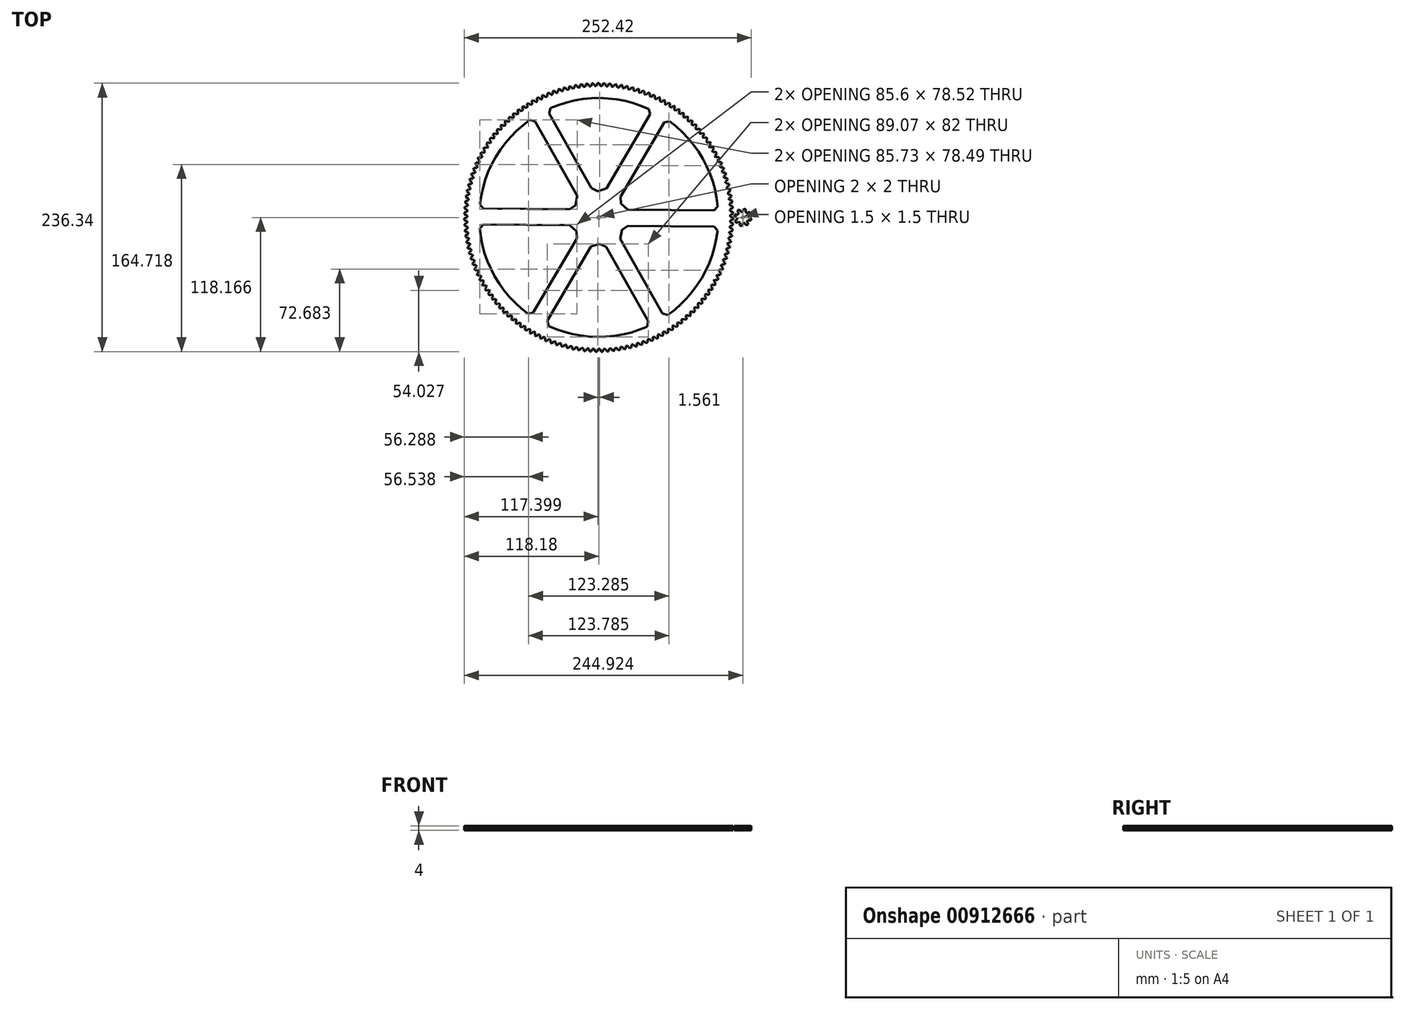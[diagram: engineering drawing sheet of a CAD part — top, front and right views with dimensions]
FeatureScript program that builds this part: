
annotation { "Feature Type Name" : "Feature", "Feature Type Description" : "" }
export const myFeature = defineFeature(function(context is Context, id is Id, definition is map)
    precondition{}
    {
        {
            var Q0;
            Q0=qCreatedBy(makeId("Top.planeOp"),FACE);
            var sketch = newSketch(context, id + "F0", { "sketchPlane" : qUnion([Q0])});
            skLineSegment(sketch, "E0", {"start": v(107.75, 0.66) * mm, "end": v(108.35, 0.46) * mm});
            skLineSegment(sketch, "E1", {"start": v(108.35, 0.46) * mm, "end": v(109.55, 0.02) * mm});
            skLineSegment(sketch, "E2", {"start": v(109.55, 0.02) * mm, "end": v(110.15, -0.2) * mm});
            skLineSegment(sketch, "E3", {"start": v(110.15, -0.2) * mm, "end": v(110.13, -1.82) * mm});
            skLineSegment(sketch, "E4", {"start": v(110.13, -1.82) * mm, "end": v(109.53, -2.04) * mm});
            skLineSegment(sketch, "E5", {"start": v(109.53, -2.04) * mm, "end": v(108.32, -2.46) * mm});
            skLineSegment(sketch, "E6", {"start": v(108.32, -2.46) * mm, "end": v(107.72, -2.65) * mm});
            skLineSegment(sketch, "E7", {"start": v(107.72, -2.65) * mm, "end": v(107.67, -4.29) * mm});
            skLineSegment(sketch, "E8", {"start": v(107.67, -4.29) * mm, "end": v(108.26, -4.52) * mm});
            skLineSegment(sketch, "E9", {"start": v(108.26, -4.52) * mm, "end": v(109.44, -5) * mm});
            skLineSegment(sketch, "E10", {"start": v(109.44, -5) * mm, "end": v(110.03, -5.26) * mm});
            skLineSegment(sketch, "E11", {"start": v(110.03, -5.26) * mm, "end": v(109.95, -6.87) * mm});
            skLineSegment(sketch, "E12", {"start": v(109.95, -6.87) * mm, "end": v(109.34, -7.06) * mm});
            skLineSegment(sketch, "E13", {"start": v(109.34, -7.06) * mm, "end": v(108.11, -7.42) * mm});
            skLineSegment(sketch, "E14", {"start": v(108.11, -7.42) * mm, "end": v(107.5, -7.59) * mm});
            skLineSegment(sketch, "E15", {"start": v(107.5, -7.59) * mm, "end": v(107.38, -9.23) * mm});
            skLineSegment(sketch, "E16", {"start": v(107.38, -9.23) * mm, "end": v(107.96, -9.48) * mm});
            skLineSegment(sketch, "E17", {"start": v(107.96, -9.48) * mm, "end": v(109.12, -10.02) * mm});
            skLineSegment(sketch, "E18", {"start": v(109.12, -10.02) * mm, "end": v(109.7, -10.3) * mm});
            skLineSegment(sketch, "E19", {"start": v(109.7, -10.3) * mm, "end": v(109.55, -11.9) * mm});
            skLineSegment(sketch, "E20", {"start": v(109.55, -11.9) * mm, "end": v(108.93, -12.07) * mm});
            skLineSegment(sketch, "E21", {"start": v(108.93, -12.07) * mm, "end": v(107.69, -12.38) * mm});
            skLineSegment(sketch, "E22", {"start": v(107.69, -12.38) * mm, "end": v(107.07, -12.52) * mm});
            skLineSegment(sketch, "E23", {"start": v(107.07, -12.52) * mm, "end": v(106.88, -14.15) * mm});
            skLineSegment(sketch, "E24", {"start": v(106.88, -14.15) * mm, "end": v(107.45, -14.43) * mm});
            skLineSegment(sketch, "E25", {"start": v(107.45, -14.43) * mm, "end": v(108.59, -15.01) * mm});
            skLineSegment(sketch, "E26", {"start": v(108.59, -15.01) * mm, "end": v(109.15, -15.32) * mm});
            skLineSegment(sketch, "E27", {"start": v(109.15, -15.32) * mm, "end": v(108.93, -16.91) * mm});
            skLineSegment(sketch, "E28", {"start": v(108.93, -16.91) * mm, "end": v(108.3, -17.06) * mm});
            skLineSegment(sketch, "E29", {"start": v(108.3, -17.06) * mm, "end": v(107.05, -17.31) * mm});
            skLineSegment(sketch, "E30", {"start": v(107.05, -17.31) * mm, "end": v(106.43, -17.43) * mm});
            skLineSegment(sketch, "E31", {"start": v(106.43, -17.43) * mm, "end": v(106.17, -19.05) * mm});
            skLineSegment(sketch, "E32", {"start": v(106.17, -19.05) * mm, "end": v(106.73, -19.35) * mm});
            skLineSegment(sketch, "E33", {"start": v(106.73, -19.35) * mm, "end": v(107.84, -19.98) * mm});
            skLineSegment(sketch, "E34", {"start": v(107.84, -19.98) * mm, "end": v(108.4, -20.31) * mm});
            skLineSegment(sketch, "E35", {"start": v(108.4, -20.31) * mm, "end": v(108.1, -21.9) * mm});
            skLineSegment(sketch, "E36", {"start": v(108.1, -21.9) * mm, "end": v(107.47, -22.01) * mm});
            skLineSegment(sketch, "E37", {"start": v(107.47, -22.01) * mm, "end": v(106.2, -22.22) * mm});
            skLineSegment(sketch, "E38", {"start": v(106.2, -22.22) * mm, "end": v(105.58, -22.3) * mm});
            skLineSegment(sketch, "E39", {"start": v(105.58, -22.3) * mm, "end": v(105.25, -23.91) * mm});
            skLineSegment(sketch, "E40", {"start": v(105.25, -23.91) * mm, "end": v(105.8, -24.24) * mm});
            skLineSegment(sketch, "E41", {"start": v(105.8, -24.24) * mm, "end": v(106.88, -24.91) * mm});
            skLineSegment(sketch, "E42", {"start": v(106.88, -24.91) * mm, "end": v(107.42, -25.27) * mm});
            skLineSegment(sketch, "E43", {"start": v(107.42, -25.27) * mm, "end": v(107.06, -26.84) * mm});
            skLineSegment(sketch, "E44", {"start": v(107.06, -26.84) * mm, "end": v(106.42, -26.93) * mm});
            skLineSegment(sketch, "E45", {"start": v(106.42, -26.93) * mm, "end": v(105.16, -27.08) * mm});
            skLineSegment(sketch, "E46", {"start": v(105.16, -27.08) * mm, "end": v(104.53, -27.13) * mm});
            skLineSegment(sketch, "E47", {"start": v(104.53, -27.13) * mm, "end": v(104.13, -28.73) * mm});
            skLineSegment(sketch, "E48", {"start": v(104.13, -28.73) * mm, "end": v(104.66, -29.08) * mm});
            skLineSegment(sketch, "E49", {"start": v(104.66, -29.08) * mm, "end": v(105.71, -29.8) * mm});
            skLineSegment(sketch, "E50", {"start": v(105.71, -29.8) * mm, "end": v(106.23, -30.18) * mm});
            skLineSegment(sketch, "E51", {"start": v(106.23, -30.18) * mm, "end": v(105.8, -31.73) * mm});
            skLineSegment(sketch, "E52", {"start": v(105.8, -31.73) * mm, "end": v(105.17, -31.8) * mm});
            skLineSegment(sketch, "E53", {"start": v(105.17, -31.8) * mm, "end": v(103.9, -31.89) * mm});
            skLineSegment(sketch, "E54", {"start": v(103.9, -31.89) * mm, "end": v(103.26, -31.92) * mm});
            skLineSegment(sketch, "E55", {"start": v(103.26, -31.92) * mm, "end": v(102.8, -33.5) * mm});
            skLineSegment(sketch, "E56", {"start": v(102.8, -33.5) * mm, "end": v(103.31, -33.87) * mm});
            skLineSegment(sketch, "E57", {"start": v(103.31, -33.87) * mm, "end": v(104.33, -34.63) * mm});
            skLineSegment(sketch, "E58", {"start": v(104.33, -34.63) * mm, "end": v(104.84, -35.03) * mm});
            skLineSegment(sketch, "E59", {"start": v(104.84, -35.03) * mm, "end": v(104.35, -36.57) * mm});
            skLineSegment(sketch, "E60", {"start": v(104.35, -36.57) * mm, "end": v(103.7, -36.6) * mm});
            skLineSegment(sketch, "E61", {"start": v(103.7, -36.6) * mm, "end": v(102.43, -36.64) * mm});
            skLineSegment(sketch, "E62", {"start": v(102.43, -36.64) * mm, "end": v(101.8, -36.65) * mm});
            skLineSegment(sketch, "E63", {"start": v(101.8, -36.65) * mm, "end": v(101.27, -38.2) * mm});
            skLineSegment(sketch, "E64", {"start": v(101.27, -38.2) * mm, "end": v(101.77, -38.6) * mm});
            skLineSegment(sketch, "E65", {"start": v(101.77, -38.6) * mm, "end": v(102.75, -39.4) * mm});
            skLineSegment(sketch, "E66", {"start": v(102.75, -39.4) * mm, "end": v(103.24, -39.82) * mm});
            skLineSegment(sketch, "E67", {"start": v(103.24, -39.82) * mm, "end": v(102.68, -41.34) * mm});
            skLineSegment(sketch, "E68", {"start": v(102.68, -41.34) * mm, "end": v(102.04, -41.34) * mm});
            skLineSegment(sketch, "E69", {"start": v(102.04, -41.34) * mm, "end": v(100.77, -41.33) * mm});
            skLineSegment(sketch, "E70", {"start": v(100.77, -41.33) * mm, "end": v(100.13, -41.3) * mm});
            skLineSegment(sketch, "E71", {"start": v(100.13, -41.3) * mm, "end": v(99.53, -42.84) * mm});
            skLineSegment(sketch, "E72", {"start": v(99.53, -42.84) * mm, "end": v(100.02, -43.25) * mm});
            skLineSegment(sketch, "E73", {"start": v(100.02, -43.25) * mm, "end": v(100.97, -44.1) * mm});
            skLineSegment(sketch, "E74", {"start": v(100.97, -44.1) * mm, "end": v(101.43, -44.54) * mm});
            skLineSegment(sketch, "E75", {"start": v(101.43, -44.54) * mm, "end": v(100.82, -46.03) * mm});
            skLineSegment(sketch, "E76", {"start": v(100.82, -46.03) * mm, "end": v(100.17, -46) * mm});
            skLineSegment(sketch, "E77", {"start": v(100.17, -46) * mm, "end": v(98.9, -45.94) * mm});
            skLineSegment(sketch, "E78", {"start": v(98.9, -45.94) * mm, "end": v(98.27, -45.89) * mm});
            skLineSegment(sketch, "E79", {"start": v(98.27, -45.89) * mm, "end": v(97.6, -47.4) * mm});
            skLineSegment(sketch, "E80", {"start": v(97.6, -47.4) * mm, "end": v(98.07, -47.83) * mm});
            skLineSegment(sketch, "E81", {"start": v(98.07, -47.83) * mm, "end": v(98.98, -48.72) * mm});
            skLineSegment(sketch, "E82", {"start": v(98.98, -48.72) * mm, "end": v(99.43, -49.18) * mm});
            skLineSegment(sketch, "E83", {"start": v(99.43, -49.18) * mm, "end": v(98.75, -50.64) * mm});
            skLineSegment(sketch, "E84", {"start": v(98.75, -50.64) * mm, "end": v(98.1, -50.6) * mm});
            skLineSegment(sketch, "E85", {"start": v(98.1, -50.6) * mm, "end": v(96.84, -50.47) * mm});
            skLineSegment(sketch, "E86", {"start": v(96.84, -50.47) * mm, "end": v(96.21, -50.39) * mm});
            skLineSegment(sketch, "E87", {"start": v(96.21, -50.39) * mm, "end": v(95.48, -51.87) * mm});
            skLineSegment(sketch, "E88", {"start": v(95.48, -51.87) * mm, "end": v(95.93, -52.32) * mm});
            skLineSegment(sketch, "E89", {"start": v(95.93, -52.32) * mm, "end": v(96.8, -53.25) * mm});
            skLineSegment(sketch, "E90", {"start": v(96.8, -53.25) * mm, "end": v(97.23, -53.73) * mm});
            skLineSegment(sketch, "E91", {"start": v(97.23, -53.73) * mm, "end": v(96.5, -55.16) * mm});
            skLineSegment(sketch, "E92", {"start": v(96.5, -55.16) * mm, "end": v(95.85, -55.08) * mm});
            skLineSegment(sketch, "E93", {"start": v(95.85, -55.08) * mm, "end": v(94.59, -54.9) * mm});
            skLineSegment(sketch, "E94", {"start": v(94.59, -54.9) * mm, "end": v(93.96, -54.8) * mm});
            skLineSegment(sketch, "E95", {"start": v(93.96, -54.8) * mm, "end": v(93.17, -56.24) * mm});
            skLineSegment(sketch, "E96", {"start": v(93.17, -56.24) * mm, "end": v(93.6, -56.71) * mm});
            skLineSegment(sketch, "E97", {"start": v(93.6, -56.71) * mm, "end": v(94.43, -57.68) * mm});
            skLineSegment(sketch, "E98", {"start": v(94.43, -57.68) * mm, "end": v(94.84, -58.17) * mm});
            skLineSegment(sketch, "E99", {"start": v(94.84, -58.17) * mm, "end": v(94.04, -59.57) * mm});
            skLineSegment(sketch, "E100", {"start": v(94.04, -59.57) * mm, "end": v(93.4, -59.47) * mm});
            skLineSegment(sketch, "E101", {"start": v(93.4, -59.47) * mm, "end": v(92.15, -59.24) * mm});
            skLineSegment(sketch, "E102", {"start": v(92.15, -59.24) * mm, "end": v(91.53, -59.1) * mm});
            skLineSegment(sketch, "E103", {"start": v(91.53, -59.1) * mm, "end": v(90.68, -60.51) * mm});
            skLineSegment(sketch, "E104", {"start": v(90.68, -60.51) * mm, "end": v(91.08, -61) * mm});
            skLineSegment(sketch, "E105", {"start": v(91.08, -61) * mm, "end": v(91.87, -62) * mm});
            skLineSegment(sketch, "E106", {"start": v(91.87, -62) * mm, "end": v(92.26, -62.52) * mm});
            skLineSegment(sketch, "E107", {"start": v(92.26, -62.52) * mm, "end": v(91.4, -63.88) * mm});
            skLineSegment(sketch, "E108", {"start": v(91.4, -63.88) * mm, "end": v(90.77, -63.75) * mm});
            skLineSegment(sketch, "E109", {"start": v(90.77, -63.75) * mm, "end": v(89.53, -63.46) * mm});
            skLineSegment(sketch, "E110", {"start": v(89.53, -63.46) * mm, "end": v(88.91, -63.3) * mm});
            skLineSegment(sketch, "E111", {"start": v(88.91, -63.3) * mm, "end": v(88, -64.68) * mm});
            skLineSegment(sketch, "E112", {"start": v(88, -64.68) * mm, "end": v(88.39, -65.18) * mm});
            skLineSegment(sketch, "E113", {"start": v(88.39, -65.18) * mm, "end": v(89.13, -66.22) * mm});
            skLineSegment(sketch, "E114", {"start": v(89.13, -66.22) * mm, "end": v(89.5, -66.75) * mm});
            skLineSegment(sketch, "E115", {"start": v(89.5, -66.75) * mm, "end": v(88.58, -68.07) * mm});
            skLineSegment(sketch, "E116", {"start": v(88.58, -68.07) * mm, "end": v(87.96, -67.91) * mm});
            skLineSegment(sketch, "E117", {"start": v(87.96, -67.91) * mm, "end": v(86.72, -67.57) * mm});
            skLineSegment(sketch, "E118", {"start": v(86.72, -67.57) * mm, "end": v(86.12, -67.4) * mm});
            skLineSegment(sketch, "E119", {"start": v(86.12, -67.4) * mm, "end": v(85.15, -68.72) * mm});
            skLineSegment(sketch, "E120", {"start": v(85.15, -68.72) * mm, "end": v(85.51, -69.24) * mm});
            skLineSegment(sketch, "E121", {"start": v(85.51, -69.24) * mm, "end": v(86.22, -70.3) * mm});
            skLineSegment(sketch, "E122", {"start": v(86.22, -70.3) * mm, "end": v(86.56, -70.85) * mm});
            skLineSegment(sketch, "E123", {"start": v(86.56, -70.85) * mm, "end": v(85.58, -72.13) * mm});
            skLineSegment(sketch, "E124", {"start": v(85.58, -72.13) * mm, "end": v(84.97, -71.95) * mm});
            skLineSegment(sketch, "E125", {"start": v(84.97, -71.95) * mm, "end": v(83.75, -71.56) * mm});
            skLineSegment(sketch, "E126", {"start": v(83.75, -71.56) * mm, "end": v(83.15, -71.35) * mm});
            skLineSegment(sketch, "E127", {"start": v(83.15, -71.35) * mm, "end": v(82.13, -72.64) * mm});
            skLineSegment(sketch, "E128", {"start": v(82.13, -72.64) * mm, "end": v(82.47, -73.17) * mm});
            skLineSegment(sketch, "E129", {"start": v(82.47, -73.17) * mm, "end": v(83.13, -74.27) * mm});
            skLineSegment(sketch, "E130", {"start": v(83.13, -74.27) * mm, "end": v(83.44, -74.83) * mm});
            skLineSegment(sketch, "E131", {"start": v(83.44, -74.83) * mm, "end": v(82.42, -76.07) * mm});
            skLineSegment(sketch, "E132", {"start": v(82.42, -76.07) * mm, "end": v(81.8, -75.86) * mm});
            skLineSegment(sketch, "E133", {"start": v(81.8, -75.86) * mm, "end": v(80.6, -75.42) * mm});
            skLineSegment(sketch, "E134", {"start": v(80.6, -75.42) * mm, "end": v(80.02, -75.18) * mm});
            skLineSegment(sketch, "E135", {"start": v(80.02, -75.18) * mm, "end": v(78.94, -76.43) * mm});
            skLineSegment(sketch, "E136", {"start": v(78.94, -76.43) * mm, "end": v(79.26, -76.98) * mm});
            skLineSegment(sketch, "E137", {"start": v(79.26, -76.98) * mm, "end": v(79.87, -78.1) * mm});
            skLineSegment(sketch, "E138", {"start": v(79.87, -78.1) * mm, "end": v(80.16, -78.67) * mm});
            skLineSegment(sketch, "E139", {"start": v(80.16, -78.67) * mm, "end": v(79.08, -79.86) * mm});
            skLineSegment(sketch, "E140", {"start": v(79.08, -79.86) * mm, "end": v(78.48, -79.63) * mm});
            skLineSegment(sketch, "E141", {"start": v(78.48, -79.63) * mm, "end": v(77.3, -79.14) * mm});
            skLineSegment(sketch, "E142", {"start": v(77.3, -79.14) * mm, "end": v(76.73, -78.88) * mm});
            skLineSegment(sketch, "E143", {"start": v(76.73, -78.88) * mm, "end": v(75.6, -80.07) * mm});
            skLineSegment(sketch, "E144", {"start": v(75.6, -80.07) * mm, "end": v(75.9, -80.63) * mm});
            skLineSegment(sketch, "E145", {"start": v(75.9, -80.63) * mm, "end": v(76.45, -81.78) * mm});
            skLineSegment(sketch, "E146", {"start": v(76.45, -81.78) * mm, "end": v(76.72, -82.37) * mm});
            skLineSegment(sketch, "E147", {"start": v(76.72, -82.37) * mm, "end": v(75.6, -83.51) * mm});
            skLineSegment(sketch, "E148", {"start": v(75.6, -83.51) * mm, "end": v(75, -83.25) * mm});
            skLineSegment(sketch, "E149", {"start": v(75, -83.25) * mm, "end": v(73.85, -82.7) * mm});
            skLineSegment(sketch, "E150", {"start": v(73.85, -82.7) * mm, "end": v(73.28, -82.43) * mm});
            skLineSegment(sketch, "E151", {"start": v(73.28, -82.43) * mm, "end": v(72.1, -83.57) * mm});
            skLineSegment(sketch, "E152", {"start": v(72.1, -83.57) * mm, "end": v(72.37, -84.15) * mm});
            skLineSegment(sketch, "E153", {"start": v(72.37, -84.15) * mm, "end": v(72.88, -85.32) * mm});
            skLineSegment(sketch, "E154", {"start": v(72.88, -85.32) * mm, "end": v(73.12, -85.91) * mm});
            skLineSegment(sketch, "E155", {"start": v(73.12, -85.91) * mm, "end": v(71.95, -87) * mm});
            skLineSegment(sketch, "E156", {"start": v(71.95, -87) * mm, "end": v(71.37, -86.72) * mm});
            skLineSegment(sketch, "E157", {"start": v(71.37, -86.72) * mm, "end": v(70.24, -86.13) * mm});
            skLineSegment(sketch, "E158", {"start": v(70.24, -86.13) * mm, "end": v(69.68, -85.83) * mm});
            skLineSegment(sketch, "E159", {"start": v(69.68, -85.83) * mm, "end": v(68.46, -86.92) * mm});
            skLineSegment(sketch, "E160", {"start": v(68.46, -86.92) * mm, "end": v(68.7, -87.5) * mm});
            skLineSegment(sketch, "E161", {"start": v(68.7, -87.5) * mm, "end": v(69.16, -88.7) * mm});
            skLineSegment(sketch, "E162", {"start": v(69.16, -88.7) * mm, "end": v(69.38, -89.3) * mm});
            skLineSegment(sketch, "E163", {"start": v(69.38, -89.3) * mm, "end": v(68.16, -90.35) * mm});
            skLineSegment(sketch, "E164", {"start": v(68.16, -90.35) * mm, "end": v(67.6, -90.04) * mm});
            skLineSegment(sketch, "E165", {"start": v(67.6, -90.04) * mm, "end": v(66.49, -89.4) * mm});
            skLineSegment(sketch, "E166", {"start": v(66.49, -89.4) * mm, "end": v(65.95, -89.07) * mm});
            skLineSegment(sketch, "E167", {"start": v(65.95, -89.07) * mm, "end": v(64.67, -90.1) * mm});
            skLineSegment(sketch, "E168", {"start": v(64.67, -90.1) * mm, "end": v(64.9, -90.7) * mm});
            skLineSegment(sketch, "E169", {"start": v(64.9, -90.7) * mm, "end": v(65.3, -91.91) * mm});
            skLineSegment(sketch, "E170", {"start": v(65.3, -91.91) * mm, "end": v(65.5, -92.53) * mm});
            skLineSegment(sketch, "E171", {"start": v(65.5, -92.53) * mm, "end": v(64.23, -93.52) * mm});
            skLineSegment(sketch, "E172", {"start": v(64.23, -93.52) * mm, "end": v(63.67, -93.19) * mm});
            skLineSegment(sketch, "E173", {"start": v(63.67, -93.19) * mm, "end": v(62.6, -92.5) * mm});
            skLineSegment(sketch, "E174", {"start": v(62.6, -92.5) * mm, "end": v(62.07, -92.15) * mm});
            skLineSegment(sketch, "E175", {"start": v(62.07, -92.15) * mm, "end": v(60.76, -93.13) * mm});
            skLineSegment(sketch, "E176", {"start": v(60.76, -93.13) * mm, "end": v(60.95, -93.74) * mm});
            skLineSegment(sketch, "E177", {"start": v(60.95, -93.74) * mm, "end": v(61.3, -94.96) * mm});
            skLineSegment(sketch, "E178", {"start": v(61.3, -94.96) * mm, "end": v(61.47, -95.58) * mm});
            skLineSegment(sketch, "E179", {"start": v(61.47, -95.58) * mm, "end": v(60.16, -96.52) * mm});
            skLineSegment(sketch, "E180", {"start": v(60.16, -96.52) * mm, "end": v(59.63, -96.17) * mm});
            skLineSegment(sketch, "E181", {"start": v(59.63, -96.17) * mm, "end": v(58.58, -95.43) * mm});
            skLineSegment(sketch, "E182", {"start": v(58.58, -95.43) * mm, "end": v(58.07, -95.06) * mm});
            skLineSegment(sketch, "E183", {"start": v(58.07, -95.06) * mm, "end": v(56.72, -95.99) * mm});
            skLineSegment(sketch, "E184", {"start": v(56.72, -95.99) * mm, "end": v(56.88, -96.6) * mm});
            skLineSegment(sketch, "E185", {"start": v(56.88, -96.6) * mm, "end": v(57.19, -97.84) * mm});
            skLineSegment(sketch, "E186", {"start": v(57.19, -97.84) * mm, "end": v(57.32, -98.47) * mm});
            skLineSegment(sketch, "E187", {"start": v(57.32, -98.47) * mm, "end": v(55.98, -99.35) * mm});
            skLineSegment(sketch, "E188", {"start": v(55.98, -99.35) * mm, "end": v(55.46, -98.97) * mm});
            skLineSegment(sketch, "E189", {"start": v(55.46, -98.97) * mm, "end": v(54.44, -98.2) * mm});
            skLineSegment(sketch, "E190", {"start": v(54.44, -98.2) * mm, "end": v(53.95, -97.8) * mm});
            skLineSegment(sketch, "E191", {"start": v(53.95, -97.8) * mm, "end": v(52.55, -98.67) * mm});
            skLineSegment(sketch, "E192", {"start": v(52.55, -98.67) * mm, "end": v(52.7, -99.28) * mm});
            skLineSegment(sketch, "E193", {"start": v(52.7, -99.28) * mm, "end": v(52.95, -100.54) * mm});
            skLineSegment(sketch, "E194", {"start": v(52.95, -100.54) * mm, "end": v(53.06, -101.17) * mm});
            skLineSegment(sketch, "E195", {"start": v(53.06, -101.17) * mm, "end": v(51.67, -102) * mm});
            skLineSegment(sketch, "E196", {"start": v(51.67, -102) * mm, "end": v(51.17, -101.6) * mm});
            skLineSegment(sketch, "E197", {"start": v(51.17, -101.6) * mm, "end": v(50.2, -100.77) * mm});
            skLineSegment(sketch, "E198", {"start": v(50.2, -100.77) * mm, "end": v(49.71, -100.36) * mm});
            skLineSegment(sketch, "E199", {"start": v(49.71, -100.36) * mm, "end": v(48.28, -101.17) * mm});
            skLineSegment(sketch, "E200", {"start": v(48.28, -101.17) * mm, "end": v(48.4, -101.79) * mm});
            skLineSegment(sketch, "E201", {"start": v(48.4, -101.79) * mm, "end": v(48.6, -103.05) * mm});
            skLineSegment(sketch, "E202", {"start": v(48.6, -103.05) * mm, "end": v(48.68, -103.69) * mm});
            skLineSegment(sketch, "E203", {"start": v(48.68, -103.69) * mm, "end": v(47.26, -104.45) * mm});
            skLineSegment(sketch, "E204", {"start": v(47.26, -104.45) * mm, "end": v(46.78, -104.03) * mm});
            skLineSegment(sketch, "E205", {"start": v(46.78, -104.03) * mm, "end": v(45.83, -103.17) * mm});
            skLineSegment(sketch, "E206", {"start": v(45.83, -103.17) * mm, "end": v(45.37, -102.73) * mm});
            skLineSegment(sketch, "E207", {"start": v(45.37, -102.73) * mm, "end": v(43.9, -103.48) * mm});
            skLineSegment(sketch, "E208", {"start": v(43.9, -103.48) * mm, "end": v(44, -104.1) * mm});
            skLineSegment(sketch, "E209", {"start": v(44, -104.1) * mm, "end": v(44.14, -105.38) * mm});
            skLineSegment(sketch, "E210", {"start": v(44.14, -105.38) * mm, "end": v(44.2, -106.02) * mm});
            skLineSegment(sketch, "E211", {"start": v(44.2, -106.02) * mm, "end": v(42.75, -106.72) * mm});
            skLineSegment(sketch, "E212", {"start": v(42.75, -106.72) * mm, "end": v(42.28, -106.28) * mm});
            skLineSegment(sketch, "E213", {"start": v(42.28, -106.28) * mm, "end": v(41.37, -105.38) * mm});
            skLineSegment(sketch, "E214", {"start": v(41.37, -105.38) * mm, "end": v(40.94, -104.92) * mm});
            skLineSegment(sketch, "E215", {"start": v(40.94, -104.92) * mm, "end": v(39.44, -105.6) * mm});
            skLineSegment(sketch, "E216", {"start": v(39.44, -105.6) * mm, "end": v(39.5, -106.23) * mm});
            skLineSegment(sketch, "E217", {"start": v(39.5, -106.23) * mm, "end": v(39.59, -107.5) * mm});
            skLineSegment(sketch, "E218", {"start": v(39.59, -107.5) * mm, "end": v(39.62, -108.15) * mm});
            skLineSegment(sketch, "E219", {"start": v(39.62, -108.15) * mm, "end": v(38.14, -108.79) * mm});
            skLineSegment(sketch, "E220", {"start": v(38.14, -108.79) * mm, "end": v(37.7, -108.33) * mm});
            skLineSegment(sketch, "E221", {"start": v(37.7, -108.33) * mm, "end": v(36.83, -107.4) * mm});
            skLineSegment(sketch, "E222", {"start": v(36.83, -107.4) * mm, "end": v(36.4, -106.92) * mm});
            skLineSegment(sketch, "E223", {"start": v(36.4, -106.92) * mm, "end": v(34.88, -107.54) * mm});
            skLineSegment(sketch, "E224", {"start": v(34.88, -107.54) * mm, "end": v(34.92, -108.17) * mm});
            skLineSegment(sketch, "E225", {"start": v(34.92, -108.17) * mm, "end": v(34.95, -109.44) * mm});
            skLineSegment(sketch, "E226", {"start": v(34.95, -109.44) * mm, "end": v(34.95, -110.09) * mm});
            skLineSegment(sketch, "E227", {"start": v(34.95, -110.09) * mm, "end": v(33.45, -110.66) * mm});
            skLineSegment(sketch, "E228", {"start": v(33.45, -110.66) * mm, "end": v(33.02, -110.18) * mm});
            skLineSegment(sketch, "E229", {"start": v(33.02, -110.18) * mm, "end": v(32.2, -109.2) * mm});
            skLineSegment(sketch, "E230", {"start": v(32.2, -109.2) * mm, "end": v(31.8, -108.72) * mm});
            skLineSegment(sketch, "E231", {"start": v(31.8, -108.72) * mm, "end": v(30.25, -109.27) * mm});
            skLineSegment(sketch, "E232", {"start": v(30.25, -109.27) * mm, "end": v(30.26, -109.9) * mm});
            skLineSegment(sketch, "E233", {"start": v(30.26, -109.9) * mm, "end": v(30.24, -111.18) * mm});
            skLineSegment(sketch, "E234", {"start": v(30.24, -111.18) * mm, "end": v(30.21, -111.82) * mm});
            skLineSegment(sketch, "E235", {"start": v(30.21, -111.82) * mm, "end": v(28.68, -112.33) * mm});
            skLineSegment(sketch, "E236", {"start": v(28.68, -112.33) * mm, "end": v(28.28, -111.84) * mm});
            skLineSegment(sketch, "E237", {"start": v(28.28, -111.84) * mm, "end": v(27.5, -110.83) * mm});
            skLineSegment(sketch, "E238", {"start": v(27.5, -110.83) * mm, "end": v(27.12, -110.32) * mm});
            skLineSegment(sketch, "E239", {"start": v(27.12, -110.32) * mm, "end": v(25.55, -110.8) * mm});
            skLineSegment(sketch, "E240", {"start": v(25.55, -110.8) * mm, "end": v(25.53, -111.44) * mm});
            skLineSegment(sketch, "E241", {"start": v(25.53, -111.44) * mm, "end": v(25.45, -112.71) * mm});
            skLineSegment(sketch, "E242", {"start": v(25.45, -112.71) * mm, "end": v(25.4, -113.36) * mm});
            skLineSegment(sketch, "E243", {"start": v(25.4, -113.36) * mm, "end": v(23.85, -113.8) * mm});
            skLineSegment(sketch, "E244", {"start": v(23.85, -113.8) * mm, "end": v(23.47, -113.29) * mm});
            skLineSegment(sketch, "E245", {"start": v(23.47, -113.29) * mm, "end": v(22.73, -112.25) * mm});
            skLineSegment(sketch, "E246", {"start": v(22.73, -112.25) * mm, "end": v(22.37, -111.72) * mm});
            skLineSegment(sketch, "E247", {"start": v(22.37, -111.72) * mm, "end": v(20.78, -112.14) * mm});
            skLineSegment(sketch, "E248", {"start": v(20.78, -112.14) * mm, "end": v(20.73, -112.77) * mm});
            skLineSegment(sketch, "E249", {"start": v(20.73, -112.77) * mm, "end": v(20.6, -114.04) * mm});
            skLineSegment(sketch, "E250", {"start": v(20.6, -114.04) * mm, "end": v(20.52, -114.68) * mm});
            skLineSegment(sketch, "E251", {"start": v(20.52, -114.68) * mm, "end": v(18.96, -115.06) * mm});
            skLineSegment(sketch, "E252", {"start": v(18.96, -115.06) * mm, "end": v(18.6, -114.53) * mm});
            skLineSegment(sketch, "E253", {"start": v(18.6, -114.53) * mm, "end": v(17.9, -113.46) * mm});
            skLineSegment(sketch, "E254", {"start": v(17.9, -113.46) * mm, "end": v(17.57, -112.92) * mm});
            skLineSegment(sketch, "E255", {"start": v(17.57, -112.92) * mm, "end": v(15.96, -113.27) * mm});
            skLineSegment(sketch, "E256", {"start": v(15.96, -113.27) * mm, "end": v(15.89, -113.9) * mm});
            skLineSegment(sketch, "E257", {"start": v(15.89, -113.9) * mm, "end": v(15.7, -115.16) * mm});
            skLineSegment(sketch, "E258", {"start": v(15.7, -115.16) * mm, "end": v(15.6, -115.8) * mm});
            skLineSegment(sketch, "E259", {"start": v(15.6, -115.8) * mm, "end": v(14.02, -116.1) * mm});
            skLineSegment(sketch, "E260", {"start": v(14.02, -116.1) * mm, "end": v(13.68, -115.56) * mm});
            skLineSegment(sketch, "E261", {"start": v(13.68, -115.56) * mm, "end": v(13.03, -114.46) * mm});
            skLineSegment(sketch, "E262", {"start": v(13.03, -114.46) * mm, "end": v(12.72, -113.9) * mm});
            skLineSegment(sketch, "E263", {"start": v(12.72, -113.9) * mm, "end": v(11.1, -114.2) * mm});
            skLineSegment(sketch, "E264", {"start": v(11.1, -114.2) * mm, "end": v(11, -114.82) * mm});
            skLineSegment(sketch, "E265", {"start": v(11, -114.82) * mm, "end": v(10.76, -116.07) * mm});
            skLineSegment(sketch, "E266", {"start": v(10.76, -116.07) * mm, "end": v(10.63, -116.7) * mm});
            skLineSegment(sketch, "E267", {"start": v(10.63, -116.7) * mm, "end": v(9.04, -116.94) * mm});
            skLineSegment(sketch, "E268", {"start": v(9.04, -116.94) * mm, "end": v(8.72, -116.38) * mm});
            skLineSegment(sketch, "E269", {"start": v(8.72, -116.38) * mm, "end": v(8.12, -115.26) * mm});
            skLineSegment(sketch, "E270", {"start": v(8.12, -115.26) * mm, "end": v(7.84, -114.7) * mm});
            skLineSegment(sketch, "E271", {"start": v(7.84, -114.7) * mm, "end": v(6.2, -114.9) * mm});
            skLineSegment(sketch, "E272", {"start": v(6.2, -114.9) * mm, "end": v(6.08, -115.52) * mm});
            skLineSegment(sketch, "E273", {"start": v(6.08, -115.52) * mm, "end": v(5.79, -116.77) * mm});
            skLineSegment(sketch, "E274", {"start": v(5.79, -116.77) * mm, "end": v(5.63, -117.4) * mm});
            skLineSegment(sketch, "E275", {"start": v(5.63, -117.4) * mm, "end": v(4.02, -117.57) * mm});
            skLineSegment(sketch, "E276", {"start": v(4.02, -117.57) * mm, "end": v(3.73, -117) * mm});
            skLineSegment(sketch, "E277", {"start": v(3.73, -117) * mm, "end": v(3.18, -115.84) * mm});
            skLineSegment(sketch, "E278", {"start": v(3.18, -115.84) * mm, "end": v(2.92, -115.26) * mm});
            skLineSegment(sketch, "E279", {"start": v(2.92, -115.26) * mm, "end": v(1.28, -115.4) * mm});
            skLineSegment(sketch, "E280", {"start": v(1.28, -115.4) * mm, "end": v(1.13, -116.02) * mm});
            skLineSegment(sketch, "E281", {"start": v(1.13, -116.02) * mm, "end": v(0.78, -117.25) * mm});
            skLineSegment(sketch, "E282", {"start": v(0.78, -117.25) * mm, "end": v(0.6, -117.87) * mm});
            skLineSegment(sketch, "E283", {"start": v(0.6, -117.87) * mm, "end": v(-1, -117.97) * mm});
            skLineSegment(sketch, "E284", {"start": v(-1, -117.97) * mm, "end": v(-1.28, -117.39) * mm});
            skLineSegment(sketch, "E285", {"start": v(-1.28, -117.39) * mm, "end": v(-1.78, -116.22) * mm});
            skLineSegment(sketch, "E286", {"start": v(-1.78, -116.22) * mm, "end": v(-2.01, -115.63) * mm});
            skLineSegment(sketch, "E287", {"start": v(-2.01, -115.63) * mm, "end": v(-3.66, -115.7) * mm});
            skLineSegment(sketch, "E288", {"start": v(-3.66, -115.7) * mm, "end": v(-3.84, -116.3) * mm});
            skLineSegment(sketch, "E289", {"start": v(-3.84, -116.3) * mm, "end": v(-4.23, -117.52) * mm});
            skLineSegment(sketch, "E290", {"start": v(-4.23, -117.52) * mm, "end": v(-4.45, -118.13) * mm});
            skLineSegment(sketch, "E291", {"start": v(-4.45, -118.13) * mm, "end": v(-6.06, -118.17) * mm});
            skLineSegment(sketch, "E292", {"start": v(-6.06, -118.17) * mm, "end": v(-6.3, -117.57) * mm});
            skLineSegment(sketch, "E293", {"start": v(-6.3, -117.57) * mm, "end": v(-6.75, -116.38) * mm});
            skLineSegment(sketch, "E294", {"start": v(-6.75, -116.38) * mm, "end": v(-6.96, -115.78) * mm});
            skLineSegment(sketch, "E295", {"start": v(-6.96, -115.78) * mm, "end": v(-8.6, -115.78) * mm});
            skLineSegment(sketch, "E296", {"start": v(-8.6, -115.78) * mm, "end": v(-8.81, -116.38) * mm});
            skLineSegment(sketch, "E297", {"start": v(-8.81, -116.38) * mm, "end": v(-9.26, -117.58) * mm});
            skLineSegment(sketch, "E298", {"start": v(-9.26, -117.58) * mm, "end": v(-9.5, -118.17) * mm});
            skLineSegment(sketch, "E299", {"start": v(-9.5, -118.17) * mm, "end": v(-11.1, -118.14) * mm});
            skLineSegment(sketch, "E300", {"start": v(-11.1, -118.14) * mm, "end": v(-11.32, -117.54) * mm});
            skLineSegment(sketch, "E301", {"start": v(-11.32, -117.54) * mm, "end": v(-11.72, -116.32) * mm});
            skLineSegment(sketch, "E302", {"start": v(-11.72, -116.32) * mm, "end": v(-11.9, -115.72) * mm});
            skLineSegment(sketch, "E303", {"start": v(-11.9, -115.72) * mm, "end": v(-13.55, -115.65) * mm});
            skLineSegment(sketch, "E304", {"start": v(-13.55, -115.65) * mm, "end": v(-13.78, -116.24) * mm});
            skLineSegment(sketch, "E305", {"start": v(-13.78, -116.24) * mm, "end": v(-14.28, -117.42) * mm});
            skLineSegment(sketch, "E306", {"start": v(-14.28, -117.42) * mm, "end": v(-14.55, -118) * mm});
            skLineSegment(sketch, "E307", {"start": v(-14.55, -118) * mm, "end": v(-16.15, -117.9) * mm});
            skLineSegment(sketch, "E308", {"start": v(-16.15, -117.9) * mm, "end": v(-16.34, -117.29) * mm});
            skLineSegment(sketch, "E309", {"start": v(-16.34, -117.29) * mm, "end": v(-16.7, -116.06) * mm});
            skLineSegment(sketch, "E310", {"start": v(-16.7, -116.06) * mm, "end": v(-16.85, -115.45) * mm});
            skLineSegment(sketch, "E311", {"start": v(-16.85, -115.45) * mm, "end": v(-18.49, -115.3) * mm});
            skLineSegment(sketch, "E312", {"start": v(-18.49, -115.3) * mm, "end": v(-18.75, -115.89) * mm});
            skLineSegment(sketch, "E313", {"start": v(-18.75, -115.89) * mm, "end": v(-19.3, -117.04) * mm});
            skLineSegment(sketch, "E314", {"start": v(-19.3, -117.04) * mm, "end": v(-19.58, -117.62) * mm});
            skLineSegment(sketch, "E315", {"start": v(-19.58, -117.62) * mm, "end": v(-21.18, -117.45) * mm});
            skLineSegment(sketch, "E316", {"start": v(-21.18, -117.45) * mm, "end": v(-21.35, -116.83) * mm});
            skLineSegment(sketch, "E317", {"start": v(-21.35, -116.83) * mm, "end": v(-21.64, -115.58) * mm});
            skLineSegment(sketch, "E318", {"start": v(-21.64, -115.58) * mm, "end": v(-21.77, -114.96) * mm});
            skLineSegment(sketch, "E319", {"start": v(-21.77, -114.96) * mm, "end": v(-23.4, -114.76) * mm});
            skLineSegment(sketch, "E320", {"start": v(-23.4, -114.76) * mm, "end": v(-23.69, -115.32) * mm});
            skLineSegment(sketch, "E321", {"start": v(-23.69, -115.32) * mm, "end": v(-24.28, -116.45) * mm});
            skLineSegment(sketch, "E322", {"start": v(-24.28, -116.45) * mm, "end": v(-24.6, -117.02) * mm});
            skLineSegment(sketch, "E323", {"start": v(-24.6, -117.02) * mm, "end": v(-26.19, -116.78) * mm});
            skLineSegment(sketch, "E324", {"start": v(-26.19, -116.78) * mm, "end": v(-26.33, -116.15) * mm});
            skLineSegment(sketch, "E325", {"start": v(-26.33, -116.15) * mm, "end": v(-26.57, -114.9) * mm});
            skLineSegment(sketch, "E326", {"start": v(-26.57, -114.9) * mm, "end": v(-26.67, -114.27) * mm});
            skLineSegment(sketch, "E327", {"start": v(-26.67, -114.27) * mm, "end": v(-28.3, -114) * mm});
            skLineSegment(sketch, "E328", {"start": v(-28.3, -114) * mm, "end": v(-28.6, -114.55) * mm});
            skLineSegment(sketch, "E329", {"start": v(-28.6, -114.55) * mm, "end": v(-29.24, -115.65) * mm});
            skLineSegment(sketch, "E330", {"start": v(-29.24, -115.65) * mm, "end": v(-29.58, -116.2) * mm});
            skLineSegment(sketch, "E331", {"start": v(-29.58, -116.2) * mm, "end": v(-31.16, -115.9) * mm});
            skLineSegment(sketch, "E332", {"start": v(-31.16, -115.9) * mm, "end": v(-31.27, -115.26) * mm});
            skLineSegment(sketch, "E333", {"start": v(-31.27, -115.26) * mm, "end": v(-31.46, -114) * mm});
            skLineSegment(sketch, "E334", {"start": v(-31.46, -114) * mm, "end": v(-31.54, -113.37) * mm});
            skLineSegment(sketch, "E335", {"start": v(-31.54, -113.37) * mm, "end": v(-33.15, -113.03) * mm});
            skLineSegment(sketch, "E336", {"start": v(-33.15, -113.03) * mm, "end": v(-33.48, -113.57) * mm});
            skLineSegment(sketch, "E337", {"start": v(-33.48, -113.57) * mm, "end": v(-34.17, -114.64) * mm});
            skLineSegment(sketch, "E338", {"start": v(-34.17, -114.64) * mm, "end": v(-34.53, -115.17) * mm});
            skLineSegment(sketch, "E339", {"start": v(-34.53, -115.17) * mm, "end": v(-36.1, -114.8) * mm});
            skLineSegment(sketch, "E340", {"start": v(-36.1, -114.8) * mm, "end": v(-36.18, -114.16) * mm});
            skLineSegment(sketch, "E341", {"start": v(-36.18, -114.16) * mm, "end": v(-36.31, -112.9) * mm});
            skLineSegment(sketch, "E342", {"start": v(-36.31, -112.9) * mm, "end": v(-36.36, -112.26) * mm});
            skLineSegment(sketch, "E343", {"start": v(-36.36, -112.26) * mm, "end": v(-37.95, -111.85) * mm});
            skLineSegment(sketch, "E344", {"start": v(-37.95, -111.85) * mm, "end": v(-38.3, -112.38) * mm});
            skLineSegment(sketch, "E345", {"start": v(-38.3, -112.38) * mm, "end": v(-39.04, -113.42) * mm});
            skLineSegment(sketch, "E346", {"start": v(-39.04, -113.42) * mm, "end": v(-39.42, -113.94) * mm});
            skLineSegment(sketch, "E347", {"start": v(-39.42, -113.94) * mm, "end": v(-40.97, -113.5) * mm});
            skLineSegment(sketch, "E348", {"start": v(-40.97, -113.5) * mm, "end": v(-41.03, -112.86) * mm});
            skLineSegment(sketch, "E349", {"start": v(-41.03, -112.86) * mm, "end": v(-41.1, -111.58) * mm});
            skLineSegment(sketch, "E350", {"start": v(-41.1, -111.58) * mm, "end": v(-41.13, -110.95) * mm});
            skLineSegment(sketch, "E351", {"start": v(-41.13, -110.95) * mm, "end": v(-42.7, -110.47) * mm});
            skLineSegment(sketch, "E352", {"start": v(-42.7, -110.47) * mm, "end": v(-43.08, -110.98) * mm});
            skLineSegment(sketch, "E353", {"start": v(-43.08, -110.98) * mm, "end": v(-43.86, -112) * mm});
            skLineSegment(sketch, "E354", {"start": v(-43.86, -112) * mm, "end": v(-44.26, -112.5) * mm});
            skLineSegment(sketch, "E355", {"start": v(-44.26, -112.5) * mm, "end": v(-45.8, -111.99) * mm});
            skLineSegment(sketch, "E356", {"start": v(-45.8, -111.99) * mm, "end": v(-45.82, -111.34) * mm});
            skLineSegment(sketch, "E357", {"start": v(-45.82, -111.34) * mm, "end": v(-45.85, -110.07) * mm});
            skLineSegment(sketch, "E358", {"start": v(-45.85, -110.07) * mm, "end": v(-45.84, -109.43) * mm});
            skLineSegment(sketch, "E359", {"start": v(-45.84, -109.43) * mm, "end": v(-47.4, -108.89) * mm});
            skLineSegment(sketch, "E360", {"start": v(-47.4, -108.89) * mm, "end": v(-47.79, -109.38) * mm});
            skLineSegment(sketch, "E361", {"start": v(-47.79, -109.38) * mm, "end": v(-48.61, -110.36) * mm});
            skLineSegment(sketch, "E362", {"start": v(-48.61, -110.36) * mm, "end": v(-49.04, -110.84) * mm});
            skLineSegment(sketch, "E363", {"start": v(-49.04, -110.84) * mm, "end": v(-50.54, -110.27) * mm});
            skLineSegment(sketch, "E364", {"start": v(-50.54, -110.27) * mm, "end": v(-50.54, -109.63) * mm});
            skLineSegment(sketch, "E365", {"start": v(-50.54, -109.63) * mm, "end": v(-50.51, -108.35) * mm});
            skLineSegment(sketch, "E366", {"start": v(-50.51, -108.35) * mm, "end": v(-50.48, -107.72) * mm});
            skLineSegment(sketch, "E367", {"start": v(-50.48, -107.72) * mm, "end": v(-52.01, -107.1) * mm});
            skLineSegment(sketch, "E368", {"start": v(-52.01, -107.1) * mm, "end": v(-52.43, -107.58) * mm});
            skLineSegment(sketch, "E369", {"start": v(-52.43, -107.58) * mm, "end": v(-53.29, -108.52) * mm});
            skLineSegment(sketch, "E370", {"start": v(-53.29, -108.52) * mm, "end": v(-53.74, -108.99) * mm});
            skLineSegment(sketch, "E371", {"start": v(-53.74, -108.99) * mm, "end": v(-55.22, -108.35) * mm});
            skLineSegment(sketch, "E372", {"start": v(-55.22, -108.35) * mm, "end": v(-55.19, -107.71) * mm});
            skLineSegment(sketch, "E373", {"start": v(-55.19, -107.71) * mm, "end": v(-55.1, -106.44) * mm});
            skLineSegment(sketch, "E374", {"start": v(-55.1, -106.44) * mm, "end": v(-55.05, -105.8) * mm});
            skLineSegment(sketch, "E375", {"start": v(-55.05, -105.8) * mm, "end": v(-56.55, -105.13) * mm});
            skLineSegment(sketch, "E376", {"start": v(-56.55, -105.13) * mm, "end": v(-56.98, -105.59) * mm});
            skLineSegment(sketch, "E377", {"start": v(-56.98, -105.59) * mm, "end": v(-57.89, -106.49) * mm});
            skLineSegment(sketch, "E378", {"start": v(-57.89, -106.49) * mm, "end": v(-58.35, -106.93) * mm});
            skLineSegment(sketch, "E379", {"start": v(-58.35, -106.93) * mm, "end": v(-59.8, -106.24) * mm});
            skLineSegment(sketch, "E380", {"start": v(-59.8, -106.24) * mm, "end": v(-59.75, -105.6) * mm});
            skLineSegment(sketch, "E381", {"start": v(-59.75, -105.6) * mm, "end": v(-59.61, -104.33) * mm});
            skLineSegment(sketch, "E382", {"start": v(-59.61, -104.33) * mm, "end": v(-59.53, -103.7) * mm});
            skLineSegment(sketch, "E383", {"start": v(-59.53, -103.7) * mm, "end": v(-61, -102.96) * mm});
            skLineSegment(sketch, "E384", {"start": v(-61, -102.96) * mm, "end": v(-61.45, -103.4) * mm});
            skLineSegment(sketch, "E385", {"start": v(-61.45, -103.4) * mm, "end": v(-62.39, -104.26) * mm});
            skLineSegment(sketch, "E386", {"start": v(-62.39, -104.26) * mm, "end": v(-62.87, -104.69) * mm});
            skLineSegment(sketch, "E387", {"start": v(-62.87, -104.69) * mm, "end": v(-64.3, -103.93) * mm});
            skLineSegment(sketch, "E388", {"start": v(-64.3, -103.93) * mm, "end": v(-64.21, -103.3) * mm});
            skLineSegment(sketch, "E389", {"start": v(-64.21, -103.3) * mm, "end": v(-64.02, -102.03) * mm});
            skLineSegment(sketch, "E390", {"start": v(-64.02, -102.03) * mm, "end": v(-63.91, -101.4) * mm});
            skLineSegment(sketch, "E391", {"start": v(-63.91, -101.4) * mm, "end": v(-65.35, -100.6) * mm});
            skLineSegment(sketch, "E392", {"start": v(-65.35, -100.6) * mm, "end": v(-65.82, -101.02) * mm});
            skLineSegment(sketch, "E393", {"start": v(-65.82, -101.02) * mm, "end": v(-66.8, -101.84) * mm});
            skLineSegment(sketch, "E394", {"start": v(-66.8, -101.84) * mm, "end": v(-67.3, -102.25) * mm});
            skLineSegment(sketch, "E395", {"start": v(-67.3, -102.25) * mm, "end": v(-68.68, -101.43) * mm});
            skLineSegment(sketch, "E396", {"start": v(-68.68, -101.43) * mm, "end": v(-68.58, -100.8) * mm});
            skLineSegment(sketch, "E397", {"start": v(-68.58, -100.8) * mm, "end": v(-68.33, -99.54) * mm});
            skLineSegment(sketch, "E398", {"start": v(-68.33, -99.54) * mm, "end": v(-68.2, -98.92) * mm});
            skLineSegment(sketch, "E399", {"start": v(-68.2, -98.92) * mm, "end": v(-69.6, -98.06) * mm});
            skLineSegment(sketch, "E400", {"start": v(-69.6, -98.06) * mm, "end": v(-70.08, -98.46) * mm});
            skLineSegment(sketch, "E401", {"start": v(-70.08, -98.46) * mm, "end": v(-71.1, -99.24) * mm});
            skLineSegment(sketch, "E402", {"start": v(-71.1, -99.24) * mm, "end": v(-71.61, -99.62) * mm});
            skLineSegment(sketch, "E403", {"start": v(-71.61, -99.62) * mm, "end": v(-72.96, -98.75) * mm});
            skLineSegment(sketch, "E404", {"start": v(-72.96, -98.75) * mm, "end": v(-72.83, -98.12) * mm});
            skLineSegment(sketch, "E405", {"start": v(-72.83, -98.12) * mm, "end": v(-72.53, -96.88) * mm});
            skLineSegment(sketch, "E406", {"start": v(-72.53, -96.88) * mm, "end": v(-72.36, -96.26) * mm});
            skLineSegment(sketch, "E407", {"start": v(-72.36, -96.26) * mm, "end": v(-73.73, -95.34) * mm});
            skLineSegment(sketch, "E408", {"start": v(-73.73, -95.34) * mm, "end": v(-74.23, -95.72) * mm});
            skLineSegment(sketch, "E409", {"start": v(-74.23, -95.72) * mm, "end": v(-75.28, -96.45) * mm});
            skLineSegment(sketch, "E410", {"start": v(-75.28, -96.45) * mm, "end": v(-75.8, -96.81) * mm});
            skLineSegment(sketch, "E411", {"start": v(-75.8, -96.81) * mm, "end": v(-77.12, -95.88) * mm});
            skLineSegment(sketch, "E412", {"start": v(-77.12, -95.88) * mm, "end": v(-76.96, -95.26) * mm});
            skLineSegment(sketch, "E413", {"start": v(-76.96, -95.26) * mm, "end": v(-76.6, -94.03) * mm});
            skLineSegment(sketch, "E414", {"start": v(-76.6, -94.03) * mm, "end": v(-76.42, -93.43) * mm});
            skLineSegment(sketch, "E415", {"start": v(-76.42, -93.43) * mm, "end": v(-77.74, -92.45) * mm});
            skLineSegment(sketch, "E416", {"start": v(-77.74, -92.45) * mm, "end": v(-78.26, -92.8) * mm});
            skLineSegment(sketch, "E417", {"start": v(-78.26, -92.8) * mm, "end": v(-79.34, -93.5) * mm});
            skLineSegment(sketch, "E418", {"start": v(-79.34, -93.5) * mm, "end": v(-79.88, -93.83) * mm});
            skLineSegment(sketch, "E419", {"start": v(-79.88, -93.83) * mm, "end": v(-81.16, -92.84) * mm});
            skLineSegment(sketch, "E420", {"start": v(-81.16, -92.84) * mm, "end": v(-80.97, -92.23) * mm});
            skLineSegment(sketch, "E421", {"start": v(-80.97, -92.23) * mm, "end": v(-80.56, -91.02) * mm});
            skLineSegment(sketch, "E422", {"start": v(-80.56, -91.02) * mm, "end": v(-80.35, -90.42) * mm});
            skLineSegment(sketch, "E423", {"start": v(-80.35, -90.42) * mm, "end": v(-81.63, -89.38) * mm});
            skLineSegment(sketch, "E424", {"start": v(-81.63, -89.38) * mm, "end": v(-82.16, -89.72) * mm});
            skLineSegment(sketch, "E425", {"start": v(-82.16, -89.72) * mm, "end": v(-83.27, -90.36) * mm});
            skLineSegment(sketch, "E426", {"start": v(-83.27, -90.36) * mm, "end": v(-83.83, -90.67) * mm});
            skLineSegment(sketch, "E427", {"start": v(-83.83, -90.67) * mm, "end": v(-85.06, -89.63) * mm});
            skLineSegment(sketch, "E428", {"start": v(-85.06, -89.63) * mm, "end": v(-84.84, -89.03) * mm});
            skLineSegment(sketch, "E429", {"start": v(-84.84, -89.03) * mm, "end": v(-84.39, -87.83) * mm});
            skLineSegment(sketch, "E430", {"start": v(-84.39, -87.83) * mm, "end": v(-84.15, -87.25) * mm});
            skLineSegment(sketch, "E431", {"start": v(-84.15, -87.25) * mm, "end": v(-85.38, -86.16) * mm});
            skLineSegment(sketch, "E432", {"start": v(-85.38, -86.16) * mm, "end": v(-85.93, -86.47) * mm});
            skLineSegment(sketch, "E433", {"start": v(-85.93, -86.47) * mm, "end": v(-87.06, -87.06) * mm});
            skLineSegment(sketch, "E434", {"start": v(-87.06, -87.06) * mm, "end": v(-87.63, -87.35) * mm});
            skLineSegment(sketch, "E435", {"start": v(-87.63, -87.35) * mm, "end": v(-88.82, -86.26) * mm});
            skLineSegment(sketch, "E436", {"start": v(-88.82, -86.26) * mm, "end": v(-88.57, -85.66) * mm});
            skLineSegment(sketch, "E437", {"start": v(-88.57, -85.66) * mm, "end": v(-88.07, -84.49) * mm});
            skLineSegment(sketch, "E438", {"start": v(-88.07, -84.49) * mm, "end": v(-87.8, -83.91) * mm});
            skLineSegment(sketch, "E439", {"start": v(-87.8, -83.91) * mm, "end": v(-88.99, -82.77) * mm});
            skLineSegment(sketch, "E440", {"start": v(-88.99, -82.77) * mm, "end": v(-89.55, -83.06) * mm});
            skLineSegment(sketch, "E441", {"start": v(-89.55, -83.06) * mm, "end": v(-90.7, -83.6) * mm});
            skLineSegment(sketch, "E442", {"start": v(-90.7, -83.6) * mm, "end": v(-91.3, -83.87) * mm});
            skLineSegment(sketch, "E443", {"start": v(-91.3, -83.87) * mm, "end": v(-92.43, -82.73) * mm});
            skLineSegment(sketch, "E444", {"start": v(-92.43, -82.73) * mm, "end": v(-92.16, -82.14) * mm});
            skLineSegment(sketch, "E445", {"start": v(-92.16, -82.14) * mm, "end": v(-91.6, -81) * mm});
            skLineSegment(sketch, "E446", {"start": v(-91.6, -81) * mm, "end": v(-91.32, -80.43) * mm});
            skLineSegment(sketch, "E447", {"start": v(-91.32, -80.43) * mm, "end": v(-92.45, -79.24) * mm});
            skLineSegment(sketch, "E448", {"start": v(-92.45, -79.24) * mm, "end": v(-93.03, -79.5) * mm});
            skLineSegment(sketch, "E449", {"start": v(-93.03, -79.5) * mm, "end": v(-94.2, -80) * mm});
            skLineSegment(sketch, "E450", {"start": v(-94.2, -80) * mm, "end": v(-94.8, -80.24) * mm});
            skLineSegment(sketch, "E451", {"start": v(-94.8, -80.24) * mm, "end": v(-95.89, -79.05) * mm});
            skLineSegment(sketch, "E452", {"start": v(-95.89, -79.05) * mm, "end": v(-95.6, -78.47) * mm});
            skLineSegment(sketch, "E453", {"start": v(-95.6, -78.47) * mm, "end": v(-95, -77.35) * mm});
            skLineSegment(sketch, "E454", {"start": v(-95, -77.35) * mm, "end": v(-94.68, -76.8) * mm});
            skLineSegment(sketch, "E455", {"start": v(-94.68, -76.8) * mm, "end": v(-95.76, -75.56) * mm});
            skLineSegment(sketch, "E456", {"start": v(-95.76, -75.56) * mm, "end": v(-96.35, -75.8) * mm});
            skLineSegment(sketch, "E457", {"start": v(-96.35, -75.8) * mm, "end": v(-97.54, -76.24) * mm});
            skLineSegment(sketch, "E458", {"start": v(-97.54, -76.24) * mm, "end": v(-98.15, -76.45) * mm});
            skLineSegment(sketch, "E459", {"start": v(-98.15, -76.45) * mm, "end": v(-99.18, -75.22) * mm});
            skLineSegment(sketch, "E460", {"start": v(-99.18, -75.22) * mm, "end": v(-98.87, -74.66) * mm});
            skLineSegment(sketch, "E461", {"start": v(-98.87, -74.66) * mm, "end": v(-98.22, -73.56) * mm});
            skLineSegment(sketch, "E462", {"start": v(-98.22, -73.56) * mm, "end": v(-97.88, -73.02) * mm});
            skLineSegment(sketch, "E463", {"start": v(-97.88, -73.02) * mm, "end": v(-98.9, -71.74) * mm});
            skLineSegment(sketch, "E464", {"start": v(-98.9, -71.74) * mm, "end": v(-99.5, -71.95) * mm});
            skLineSegment(sketch, "E465", {"start": v(-99.5, -71.95) * mm, "end": v(-100.72, -72.35) * mm});
            skLineSegment(sketch, "E466", {"start": v(-100.72, -72.35) * mm, "end": v(-101.33, -72.53) * mm});
            skLineSegment(sketch, "E467", {"start": v(-101.33, -72.53) * mm, "end": v(-102.31, -71.26) * mm});
            skLineSegment(sketch, "E468", {"start": v(-102.31, -71.26) * mm, "end": v(-101.97, -70.7) * mm});
            skLineSegment(sketch, "E469", {"start": v(-101.97, -70.7) * mm, "end": v(-101.28, -69.64) * mm});
            skLineSegment(sketch, "E470", {"start": v(-101.28, -69.64) * mm, "end": v(-100.92, -69.12) * mm});
            skLineSegment(sketch, "E471", {"start": v(-100.92, -69.12) * mm, "end": v(-101.89, -67.8) * mm});
            skLineSegment(sketch, "E472", {"start": v(-101.89, -67.8) * mm, "end": v(-102.5, -67.98) * mm});
            skLineSegment(sketch, "E473", {"start": v(-102.5, -67.98) * mm, "end": v(-103.72, -68.32) * mm});
            skLineSegment(sketch, "E474", {"start": v(-103.72, -68.32) * mm, "end": v(-104.35, -68.48) * mm});
            skLineSegment(sketch, "E475", {"start": v(-104.35, -68.48) * mm, "end": v(-105.27, -67.16) * mm});
            skLineSegment(sketch, "E476", {"start": v(-105.27, -67.16) * mm, "end": v(-104.9, -66.63) * mm});
            skLineSegment(sketch, "E477", {"start": v(-104.9, -66.63) * mm, "end": v(-104.17, -65.6) * mm});
            skLineSegment(sketch, "E478", {"start": v(-104.17, -65.6) * mm, "end": v(-103.79, -65.09) * mm});
            skLineSegment(sketch, "E479", {"start": v(-103.79, -65.09) * mm, "end": v(-104.7, -63.72) * mm});
            skLineSegment(sketch, "E480", {"start": v(-104.7, -63.72) * mm, "end": v(-105.31, -63.88) * mm});
            skLineSegment(sketch, "E481", {"start": v(-105.31, -63.88) * mm, "end": v(-106.56, -64.17) * mm});
            skLineSegment(sketch, "E482", {"start": v(-106.56, -64.17) * mm, "end": v(-107.19, -64.3) * mm});
            skLineSegment(sketch, "E483", {"start": v(-107.19, -64.3) * mm, "end": v(-108.05, -62.95) * mm});
            skLineSegment(sketch, "E484", {"start": v(-108.05, -62.95) * mm, "end": v(-107.67, -62.43) * mm});
            skLineSegment(sketch, "E485", {"start": v(-107.67, -62.43) * mm, "end": v(-106.88, -61.42) * mm});
            skLineSegment(sketch, "E486", {"start": v(-106.88, -61.42) * mm, "end": v(-106.48, -60.94) * mm});
            skLineSegment(sketch, "E487", {"start": v(-106.48, -60.94) * mm, "end": v(-107.33, -59.53) * mm});
            skLineSegment(sketch, "E488", {"start": v(-107.33, -59.53) * mm, "end": v(-107.95, -59.66) * mm});
            skLineSegment(sketch, "E489", {"start": v(-107.95, -59.66) * mm, "end": v(-109.2, -59.9) * mm});
            skLineSegment(sketch, "E490", {"start": v(-109.2, -59.9) * mm, "end": v(-109.84, -60) * mm});
            skLineSegment(sketch, "E491", {"start": v(-109.84, -60) * mm, "end": v(-110.65, -58.61) * mm});
            skLineSegment(sketch, "E492", {"start": v(-110.65, -58.61) * mm, "end": v(-110.24, -58.12) * mm});
            skLineSegment(sketch, "E493", {"start": v(-110.24, -58.12) * mm, "end": v(-109.42, -57.14) * mm});
            skLineSegment(sketch, "E494", {"start": v(-109.42, -57.14) * mm, "end": v(-109, -56.67) * mm});
            skLineSegment(sketch, "E495", {"start": v(-109, -56.67) * mm, "end": v(-109.79, -55.23) * mm});
            skLineSegment(sketch, "E496", {"start": v(-109.79, -55.23) * mm, "end": v(-110.41, -55.34) * mm});
            skLineSegment(sketch, "E497", {"start": v(-110.41, -55.34) * mm, "end": v(-111.67, -55.52) * mm});
            skLineSegment(sketch, "E498", {"start": v(-111.67, -55.52) * mm, "end": v(-112.31, -55.6) * mm});
            skLineSegment(sketch, "E499", {"start": v(-112.31, -55.6) * mm, "end": v(-113.06, -54.18) * mm});
            skLineSegment(sketch, "E500", {"start": v(-113.06, -54.18) * mm, "end": v(-112.63, -53.7) * mm});
            skLineSegment(sketch, "E501", {"start": v(-112.63, -53.7) * mm, "end": v(-111.76, -52.76) * mm});
            skLineSegment(sketch, "E502", {"start": v(-111.76, -52.76) * mm, "end": v(-111.32, -52.3) * mm});
            skLineSegment(sketch, "E503", {"start": v(-111.32, -52.3) * mm, "end": v(-112.05, -50.83) * mm});
            skLineSegment(sketch, "E504", {"start": v(-112.05, -50.83) * mm, "end": v(-112.68, -50.91) * mm});
            skLineSegment(sketch, "E505", {"start": v(-112.68, -50.91) * mm, "end": v(-113.95, -51.04) * mm});
            skLineSegment(sketch, "E506", {"start": v(-113.95, -51.04) * mm, "end": v(-114.6, -51.1) * mm});
            skLineSegment(sketch, "E507", {"start": v(-114.6, -51.1) * mm, "end": v(-115.28, -49.64) * mm});
            skLineSegment(sketch, "E508", {"start": v(-115.28, -49.64) * mm, "end": v(-114.83, -49.18) * mm});
            skLineSegment(sketch, "E509", {"start": v(-114.83, -49.18) * mm, "end": v(-113.92, -48.28) * mm});
            skLineSegment(sketch, "E510", {"start": v(-113.92, -48.28) * mm, "end": v(-113.46, -47.85) * mm});
            skLineSegment(sketch, "E511", {"start": v(-113.46, -47.85) * mm, "end": v(-114.13, -46.34) * mm});
            skLineSegment(sketch, "E512", {"start": v(-114.13, -46.34) * mm, "end": v(-114.76, -46.4) * mm});
            skLineSegment(sketch, "E513", {"start": v(-114.76, -46.4) * mm, "end": v(-116.04, -46.47) * mm});
            skLineSegment(sketch, "E514", {"start": v(-116.04, -46.47) * mm, "end": v(-116.68, -46.5) * mm});
            skLineSegment(sketch, "E515", {"start": v(-116.68, -46.5) * mm, "end": v(-117.3, -45) * mm});
            skLineSegment(sketch, "E516", {"start": v(-117.3, -45) * mm, "end": v(-116.84, -44.57) * mm});
            skLineSegment(sketch, "E517", {"start": v(-116.84, -44.57) * mm, "end": v(-115.9, -43.71) * mm});
            skLineSegment(sketch, "E518", {"start": v(-115.9, -43.71) * mm, "end": v(-115.41, -43.3) * mm});
            skLineSegment(sketch, "E519", {"start": v(-115.41, -43.3) * mm, "end": v(-116.01, -41.77) * mm});
            skLineSegment(sketch, "E520", {"start": v(-116.01, -41.77) * mm, "end": v(-116.65, -41.8) * mm});
            skLineSegment(sketch, "E521", {"start": v(-116.65, -41.8) * mm, "end": v(-117.92, -41.81) * mm});
            skLineSegment(sketch, "E522", {"start": v(-117.92, -41.81) * mm, "end": v(-118.57, -41.8) * mm});
            skLineSegment(sketch, "E523", {"start": v(-118.57, -41.8) * mm, "end": v(-119.13, -40.3) * mm});
            skLineSegment(sketch, "E524", {"start": v(-119.13, -40.3) * mm, "end": v(-118.64, -39.88) * mm});
            skLineSegment(sketch, "E525", {"start": v(-118.64, -39.88) * mm, "end": v(-117.66, -39.06) * mm});
            skLineSegment(sketch, "E526", {"start": v(-117.66, -39.06) * mm, "end": v(-117.16, -38.67) * mm});
            skLineSegment(sketch, "E527", {"start": v(-117.16, -38.67) * mm, "end": v(-117.7, -37.11) * mm});
            skLineSegment(sketch, "E528", {"start": v(-117.7, -37.11) * mm, "end": v(-118.33, -37.11) * mm});
            skLineSegment(sketch, "E529", {"start": v(-118.33, -37.11) * mm, "end": v(-119.6, -37.08) * mm});
            skLineSegment(sketch, "E530", {"start": v(-119.6, -37.08) * mm, "end": v(-120.25, -37.05) * mm});
            skLineSegment(sketch, "E531", {"start": v(-120.25, -37.05) * mm, "end": v(-120.75, -35.52) * mm});
            skLineSegment(sketch, "E532", {"start": v(-120.75, -35.52) * mm, "end": v(-120.24, -35.11) * mm});
            skLineSegment(sketch, "E533", {"start": v(-120.24, -35.11) * mm, "end": v(-119.23, -34.34) * mm});
            skLineSegment(sketch, "E534", {"start": v(-119.23, -34.34) * mm, "end": v(-118.71, -33.97) * mm});
            skLineSegment(sketch, "E535", {"start": v(-118.71, -33.97) * mm, "end": v(-119.19, -32.4) * mm});
            skLineSegment(sketch, "E536", {"start": v(-119.19, -32.4) * mm, "end": v(-119.82, -32.37) * mm});
            skLineSegment(sketch, "E537", {"start": v(-119.82, -32.37) * mm, "end": v(-121.1, -32.28) * mm});
            skLineSegment(sketch, "E538", {"start": v(-121.1, -32.28) * mm, "end": v(-121.73, -32.22) * mm});
            skLineSegment(sketch, "E539", {"start": v(-121.73, -32.22) * mm, "end": v(-122.16, -30.67) * mm});
            skLineSegment(sketch, "E540", {"start": v(-122.16, -30.67) * mm, "end": v(-121.64, -30.29) * mm});
            skLineSegment(sketch, "E541", {"start": v(-121.64, -30.29) * mm, "end": v(-120.6, -29.56) * mm});
            skLineSegment(sketch, "E542", {"start": v(-120.6, -29.56) * mm, "end": v(-120.06, -29.21) * mm});
            skLineSegment(sketch, "E543", {"start": v(-120.06, -29.21) * mm, "end": v(-120.47, -27.62) * mm});
            skLineSegment(sketch, "E544", {"start": v(-120.47, -27.62) * mm, "end": v(-121.1, -27.56) * mm});
            skLineSegment(sketch, "E545", {"start": v(-121.1, -27.56) * mm, "end": v(-122.37, -27.42) * mm});
            skLineSegment(sketch, "E546", {"start": v(-122.37, -27.42) * mm, "end": v(-123, -27.33) * mm});
            skLineSegment(sketch, "E547", {"start": v(-123, -27.33) * mm, "end": v(-123.37, -25.76) * mm});
            skLineSegment(sketch, "E548", {"start": v(-123.37, -25.76) * mm, "end": v(-122.83, -25.4) * mm});
            skLineSegment(sketch, "E549", {"start": v(-122.83, -25.4) * mm, "end": v(-121.75, -24.72) * mm});
            skLineSegment(sketch, "E550", {"start": v(-121.75, -24.72) * mm, "end": v(-121.21, -24.4) * mm});
            skLineSegment(sketch, "E551", {"start": v(-121.21, -24.4) * mm, "end": v(-121.55, -22.79) * mm});
            skLineSegment(sketch, "E552", {"start": v(-121.55, -22.79) * mm, "end": v(-122.17, -22.7) * mm});
            skLineSegment(sketch, "E553", {"start": v(-122.17, -22.7) * mm, "end": v(-123.43, -22.5) * mm});
            skLineSegment(sketch, "E554", {"start": v(-123.43, -22.5) * mm, "end": v(-124.07, -22.4) * mm});
            skLineSegment(sketch, "E555", {"start": v(-124.07, -22.4) * mm, "end": v(-124.36, -20.81) * mm});
            skLineSegment(sketch, "E556", {"start": v(-124.36, -20.81) * mm, "end": v(-123.81, -20.48) * mm});
            skLineSegment(sketch, "E557", {"start": v(-123.81, -20.48) * mm, "end": v(-122.7, -19.84) * mm});
            skLineSegment(sketch, "E558", {"start": v(-122.7, -19.84) * mm, "end": v(-122.15, -19.54) * mm});
            skLineSegment(sketch, "E559", {"start": v(-122.15, -19.54) * mm, "end": v(-122.42, -17.91) * mm});
            skLineSegment(sketch, "E560", {"start": v(-122.42, -17.91) * mm, "end": v(-123.04, -17.8) * mm});
            skLineSegment(sketch, "E561", {"start": v(-123.04, -17.8) * mm, "end": v(-124.3, -17.56) * mm});
            skLineSegment(sketch, "E562", {"start": v(-124.3, -17.56) * mm, "end": v(-124.92, -17.41) * mm});
            skLineSegment(sketch, "E563", {"start": v(-124.92, -17.41) * mm, "end": v(-125.15, -15.82) * mm});
            skLineSegment(sketch, "E564", {"start": v(-125.15, -15.82) * mm, "end": v(-124.58, -15.51) * mm});
            skLineSegment(sketch, "E565", {"start": v(-124.58, -15.51) * mm, "end": v(-123.45, -14.92) * mm});
            skLineSegment(sketch, "E566", {"start": v(-123.45, -14.92) * mm, "end": v(-122.88, -14.64) * mm});
            skLineSegment(sketch, "E567", {"start": v(-122.88, -14.64) * mm, "end": v(-123.08, -13.01) * mm});
            skLineSegment(sketch, "E568", {"start": v(-123.08, -13.01) * mm, "end": v(-123.7, -12.88) * mm});
            skLineSegment(sketch, "E569", {"start": v(-123.7, -12.88) * mm, "end": v(-124.93, -12.57) * mm});
            skLineSegment(sketch, "E570", {"start": v(-124.93, -12.57) * mm, "end": v(-125.56, -12.4) * mm});
            skLineSegment(sketch, "E571", {"start": v(-125.56, -12.4) * mm, "end": v(-125.71, -10.8) * mm});
            skLineSegment(sketch, "E572", {"start": v(-125.71, -10.8) * mm, "end": v(-125.14, -10.52) * mm});
            skLineSegment(sketch, "E573", {"start": v(-125.14, -10.52) * mm, "end": v(-123.98, -9.98) * mm});
            skLineSegment(sketch, "E574", {"start": v(-123.98, -9.98) * mm, "end": v(-123.4, -9.72) * mm});
            skLineSegment(sketch, "E575", {"start": v(-123.4, -9.72) * mm, "end": v(-123.53, -8.08) * mm});
            skLineSegment(sketch, "E576", {"start": v(-123.53, -8.08) * mm, "end": v(-124.14, -7.92) * mm});
            skLineSegment(sketch, "E577", {"start": v(-124.14, -7.92) * mm, "end": v(-125.37, -7.56) * mm});
            skLineSegment(sketch, "E578", {"start": v(-125.37, -7.56) * mm, "end": v(-125.98, -7.37) * mm});
            skLineSegment(sketch, "E579", {"start": v(-125.98, -7.37) * mm, "end": v(-126.07, -5.76) * mm});
            skLineSegment(sketch, "E580", {"start": v(-126.07, -5.76) * mm, "end": v(-125.48, -5.5) * mm});
            skLineSegment(sketch, "E581", {"start": v(-125.48, -5.5) * mm, "end": v(-124.3, -5.01) * mm});
            skLineSegment(sketch, "E582", {"start": v(-124.3, -5.01) * mm, "end": v(-123.71, -4.78) * mm});
            skLineSegment(sketch, "E583", {"start": v(-123.71, -4.78) * mm, "end": v(-123.77, -3.14) * mm});
            skLineSegment(sketch, "E584", {"start": v(-123.77, -3.14) * mm, "end": v(-124.37, -2.95) * mm});
            skLineSegment(sketch, "E585", {"start": v(-124.37, -2.95) * mm, "end": v(-125.58, -2.54) * mm});
            skLineSegment(sketch, "E586", {"start": v(-125.58, -2.54) * mm, "end": v(-126.19, -2.32) * mm});
            skLineSegment(sketch, "E587", {"start": v(-126.19, -2.32) * mm, "end": v(-126.2, -0.71) * mm});
            skLineSegment(sketch, "E588", {"start": v(-126.2, -0.71) * mm, "end": v(-125.6, -0.48) * mm});
            skLineSegment(sketch, "E589", {"start": v(-125.6, -0.48) * mm, "end": v(-124.4, -0.04) * mm});
            skLineSegment(sketch, "E590", {"start": v(-124.4, -0.04) * mm, "end": v(-123.8, 0.16) * mm});
            skLineSegment(sketch, "E591", {"start": v(-123.8, 0.16) * mm, "end": v(-123.8, 1.8) * mm});
            skLineSegment(sketch, "E592", {"start": v(-123.8, 1.8) * mm, "end": v(-124.4, 2.02) * mm});
            skLineSegment(sketch, "E593", {"start": v(-124.4, 2.02) * mm, "end": v(-125.58, 2.48) * mm});
            skLineSegment(sketch, "E594", {"start": v(-125.58, 2.48) * mm, "end": v(-126.18, 2.73) * mm});
            skLineSegment(sketch, "E595", {"start": v(-126.18, 2.73) * mm, "end": v(-126.13, 4.34) * mm});
            skLineSegment(sketch, "E596", {"start": v(-126.13, 4.34) * mm, "end": v(-125.52, 4.55) * mm});
            skLineSegment(sketch, "E597", {"start": v(-125.52, 4.55) * mm, "end": v(-124.3, 4.93) * mm});
            skLineSegment(sketch, "E598", {"start": v(-124.3, 4.93) * mm, "end": v(-123.7, 5.11) * mm});
            skLineSegment(sketch, "E599", {"start": v(-123.7, 5.11) * mm, "end": v(-123.61, 6.75) * mm});
            skLineSegment(sketch, "E600", {"start": v(-123.61, 6.75) * mm, "end": v(-124.2, 7) * mm});
            skLineSegment(sketch, "E601", {"start": v(-124.2, 7) * mm, "end": v(-125.37, 7.5) * mm});
            skLineSegment(sketch, "E602", {"start": v(-125.37, 7.5) * mm, "end": v(-125.95, 7.77) * mm});
            skLineSegment(sketch, "E603", {"start": v(-125.95, 7.77) * mm, "end": v(-125.84, 9.38) * mm});
            skLineSegment(sketch, "E604", {"start": v(-125.84, 9.38) * mm, "end": v(-125.22, 9.56) * mm});
            skLineSegment(sketch, "E605", {"start": v(-125.22, 9.56) * mm, "end": v(-123.99, 9.9) * mm});
            skLineSegment(sketch, "E606", {"start": v(-123.99, 9.9) * mm, "end": v(-123.37, 10.05) * mm});
            skLineSegment(sketch, "E607", {"start": v(-123.37, 10.05) * mm, "end": v(-123.22, 11.69) * mm});
            skLineSegment(sketch, "E608", {"start": v(-123.22, 11.69) * mm, "end": v(-123.8, 11.95) * mm});
            skLineSegment(sketch, "E609", {"start": v(-123.8, 11.95) * mm, "end": v(-124.94, 12.5) * mm});
            skLineSegment(sketch, "E610", {"start": v(-124.94, 12.5) * mm, "end": v(-125.51, 12.8) * mm});
            skLineSegment(sketch, "E611", {"start": v(-125.51, 12.8) * mm, "end": v(-125.33, 14.4) * mm});
            skLineSegment(sketch, "E612", {"start": v(-125.33, 14.4) * mm, "end": v(-124.7, 14.56) * mm});
            skLineSegment(sketch, "E613", {"start": v(-124.7, 14.56) * mm, "end": v(-123.46, 14.84) * mm});
            skLineSegment(sketch, "E614", {"start": v(-123.46, 14.84) * mm, "end": v(-122.84, 14.97) * mm});
            skLineSegment(sketch, "E615", {"start": v(-122.84, 14.97) * mm, "end": v(-122.61, 16.6) * mm});
            skLineSegment(sketch, "E616", {"start": v(-122.61, 16.6) * mm, "end": v(-123.18, 16.88) * mm});
            skLineSegment(sketch, "E617", {"start": v(-123.18, 16.88) * mm, "end": v(-124.3, 17.5) * mm});
            skLineSegment(sketch, "E618", {"start": v(-124.3, 17.5) * mm, "end": v(-124.86, 17.81) * mm});
            skLineSegment(sketch, "E619", {"start": v(-124.86, 17.81) * mm, "end": v(-124.6, 19.4) * mm});
            skLineSegment(sketch, "E620", {"start": v(-124.6, 19.4) * mm, "end": v(-123.97, 19.53) * mm});
            skLineSegment(sketch, "E621", {"start": v(-123.97, 19.53) * mm, "end": v(-122.72, 19.76) * mm});
            skLineSegment(sketch, "E622", {"start": v(-122.72, 19.76) * mm, "end": v(-122.1, 19.86) * mm});
            skLineSegment(sketch, "E623", {"start": v(-122.1, 19.86) * mm, "end": v(-121.8, 21.48) * mm});
            skLineSegment(sketch, "E624", {"start": v(-121.8, 21.48) * mm, "end": v(-122.35, 21.79) * mm});
            skLineSegment(sketch, "E625", {"start": v(-122.35, 21.79) * mm, "end": v(-123.45, 22.45) * mm});
            skLineSegment(sketch, "E626", {"start": v(-123.45, 22.45) * mm, "end": v(-123.99, 22.79) * mm});
            skLineSegment(sketch, "E627", {"start": v(-123.99, 22.79) * mm, "end": v(-123.67, 24.37) * mm});
            skLineSegment(sketch, "E628", {"start": v(-123.67, 24.37) * mm, "end": v(-123.03, 24.47) * mm});
            skLineSegment(sketch, "E629", {"start": v(-123.03, 24.47) * mm, "end": v(-121.77, 24.64) * mm});
            skLineSegment(sketch, "E630", {"start": v(-121.77, 24.64) * mm, "end": v(-121.14, 24.72) * mm});
            skLineSegment(sketch, "E631", {"start": v(-121.14, 24.72) * mm, "end": v(-120.78, 26.32) * mm});
            skLineSegment(sketch, "E632", {"start": v(-120.78, 26.32) * mm, "end": v(-121.31, 26.65) * mm});
            skLineSegment(sketch, "E633", {"start": v(-121.31, 26.65) * mm, "end": v(-122.38, 27.36) * mm});
            skLineSegment(sketch, "E634", {"start": v(-122.38, 27.36) * mm, "end": v(-122.9, 27.72) * mm});
            skLineSegment(sketch, "E635", {"start": v(-122.9, 27.72) * mm, "end": v(-122.52, 29.29) * mm});
            skLineSegment(sketch, "E636", {"start": v(-122.52, 29.29) * mm, "end": v(-121.88, 29.36) * mm});
            skLineSegment(sketch, "E637", {"start": v(-121.88, 29.36) * mm, "end": v(-120.61, 29.48) * mm});
            skLineSegment(sketch, "E638", {"start": v(-120.61, 29.48) * mm, "end": v(-119.98, 29.53) * mm});
            skLineSegment(sketch, "E639", {"start": v(-119.98, 29.53) * mm, "end": v(-119.55, 31.11) * mm});
            skLineSegment(sketch, "E640", {"start": v(-119.55, 31.11) * mm, "end": v(-120.07, 31.47) * mm});
            skLineSegment(sketch, "E641", {"start": v(-120.07, 31.47) * mm, "end": v(-121.1, 32.22) * mm});
            skLineSegment(sketch, "E642", {"start": v(-121.1, 32.22) * mm, "end": v(-121.62, 32.6) * mm});
            skLineSegment(sketch, "E643", {"start": v(-121.62, 32.6) * mm, "end": v(-121.17, 34.15) * mm});
            skLineSegment(sketch, "E644", {"start": v(-121.17, 34.15) * mm, "end": v(-120.52, 34.2) * mm});
            skLineSegment(sketch, "E645", {"start": v(-120.52, 34.2) * mm, "end": v(-119.25, 34.27) * mm});
            skLineSegment(sketch, "E646", {"start": v(-119.25, 34.27) * mm, "end": v(-118.62, 34.28) * mm});
            skLineSegment(sketch, "E647", {"start": v(-118.62, 34.28) * mm, "end": v(-118.12, 35.85) * mm});
            skLineSegment(sketch, "E648", {"start": v(-118.12, 35.85) * mm, "end": v(-118.62, 36.23) * mm});
            skLineSegment(sketch, "E649", {"start": v(-118.62, 36.23) * mm, "end": v(-119.63, 37.02) * mm});
            skLineSegment(sketch, "E650", {"start": v(-119.63, 37.02) * mm, "end": v(-120.12, 37.43) * mm});
            skLineSegment(sketch, "E651", {"start": v(-120.12, 37.43) * mm, "end": v(-119.6, 38.95) * mm});
            skLineSegment(sketch, "E652", {"start": v(-119.6, 38.95) * mm, "end": v(-118.96, 38.97) * mm});
            skLineSegment(sketch, "E653", {"start": v(-118.96, 38.97) * mm, "end": v(-117.68, 38.99) * mm});
            skLineSegment(sketch, "E654", {"start": v(-117.68, 38.99) * mm, "end": v(-117.05, 38.98) * mm});
            skLineSegment(sketch, "E655", {"start": v(-117.05, 38.98) * mm, "end": v(-116.49, 40.52) * mm});
            skLineSegment(sketch, "E656", {"start": v(-116.49, 40.52) * mm, "end": v(-116.98, 40.92) * mm});
            skLineSegment(sketch, "E657", {"start": v(-116.98, 40.92) * mm, "end": v(-117.94, 41.75) * mm});
            skLineSegment(sketch, "E658", {"start": v(-117.94, 41.75) * mm, "end": v(-118.42, 42.19) * mm});
            skLineSegment(sketch, "E659", {"start": v(-118.42, 42.19) * mm, "end": v(-117.84, 43.69) * mm});
            skLineSegment(sketch, "E660", {"start": v(-117.84, 43.69) * mm, "end": v(-117.2, 43.68) * mm});
            skLineSegment(sketch, "E661", {"start": v(-117.2, 43.68) * mm, "end": v(-115.92, 43.64) * mm});
            skLineSegment(sketch, "E662", {"start": v(-115.92, 43.64) * mm, "end": v(-115.28, 43.6) * mm});
            skLineSegment(sketch, "E663", {"start": v(-115.28, 43.6) * mm, "end": v(-114.65, 45.12) * mm});
            skLineSegment(sketch, "E664", {"start": v(-114.65, 45.12) * mm, "end": v(-115.13, 45.54) * mm});
            skLineSegment(sketch, "E665", {"start": v(-115.13, 45.54) * mm, "end": v(-116.06, 46.41) * mm});
            skLineSegment(sketch, "E666", {"start": v(-116.06, 46.41) * mm, "end": v(-116.52, 46.86) * mm});
            skLineSegment(sketch, "E667", {"start": v(-116.52, 46.86) * mm, "end": v(-115.87, 48.34) * mm});
            skLineSegment(sketch, "E668", {"start": v(-115.87, 48.34) * mm, "end": v(-115.23, 48.3) * mm});
            skLineSegment(sketch, "E669", {"start": v(-115.23, 48.3) * mm, "end": v(-113.95, 48.2) * mm});
            skLineSegment(sketch, "E670", {"start": v(-113.95, 48.2) * mm, "end": v(-113.32, 48.14) * mm});
            skLineSegment(sketch, "E671", {"start": v(-113.32, 48.14) * mm, "end": v(-112.63, 49.63) * mm});
            skLineSegment(sketch, "E672", {"start": v(-112.63, 49.63) * mm, "end": v(-113.08, 50.07) * mm});
            skLineSegment(sketch, "E673", {"start": v(-113.08, 50.07) * mm, "end": v(-113.98, 50.99) * mm});
            skLineSegment(sketch, "E674", {"start": v(-113.98, 50.99) * mm, "end": v(-114.42, 51.46) * mm});
            skLineSegment(sketch, "E675", {"start": v(-114.42, 51.46) * mm, "end": v(-113.7, 52.9) * mm});
            skLineSegment(sketch, "E676", {"start": v(-113.7, 52.9) * mm, "end": v(-113.06, 52.84) * mm});
            skLineSegment(sketch, "E677", {"start": v(-113.06, 52.84) * mm, "end": v(-111.8, 52.69) * mm});
            skLineSegment(sketch, "E678", {"start": v(-111.8, 52.69) * mm, "end": v(-111.17, 52.6) * mm});
            skLineSegment(sketch, "E679", {"start": v(-111.17, 52.6) * mm, "end": v(-110.41, 54.06) * mm});
            skLineSegment(sketch, "E680", {"start": v(-110.41, 54.06) * mm, "end": v(-110.85, 54.52) * mm});
            skLineSegment(sketch, "E681", {"start": v(-110.85, 54.52) * mm, "end": v(-111.7, 55.47) * mm});
            skLineSegment(sketch, "E682", {"start": v(-111.7, 55.47) * mm, "end": v(-112.12, 55.96) * mm});
            skLineSegment(sketch, "E683", {"start": v(-112.12, 55.96) * mm, "end": v(-111.35, 57.37) * mm});
            skLineSegment(sketch, "E684", {"start": v(-111.35, 57.37) * mm, "end": v(-110.71, 57.28) * mm});
            skLineSegment(sketch, "E685", {"start": v(-110.71, 57.28) * mm, "end": v(-109.45, 57.07) * mm});
            skLineSegment(sketch, "E686", {"start": v(-109.45, 57.07) * mm, "end": v(-108.83, 56.96) * mm});
            skLineSegment(sketch, "E687", {"start": v(-108.83, 56.96) * mm, "end": v(-108, 58.38) * mm});
            skLineSegment(sketch, "E688", {"start": v(-108, 58.38) * mm, "end": v(-108.42, 58.86) * mm});
            skLineSegment(sketch, "E689", {"start": v(-108.42, 58.86) * mm, "end": v(-109.24, 59.85) * mm});
            skLineSegment(sketch, "E690", {"start": v(-109.24, 59.85) * mm, "end": v(-109.63, 60.35) * mm});
            skLineSegment(sketch, "E691", {"start": v(-109.63, 60.35) * mm, "end": v(-108.8, 61.73) * mm});
            skLineSegment(sketch, "E692", {"start": v(-108.8, 61.73) * mm, "end": v(-108.17, 61.61) * mm});
            skLineSegment(sketch, "E693", {"start": v(-108.17, 61.61) * mm, "end": v(-106.92, 61.36) * mm});
            skLineSegment(sketch, "E694", {"start": v(-106.92, 61.36) * mm, "end": v(-106.3, 61.21) * mm});
            skLineSegment(sketch, "E695", {"start": v(-106.3, 61.21) * mm, "end": v(-105.42, 62.6) * mm});
            skLineSegment(sketch, "E696", {"start": v(-105.42, 62.6) * mm, "end": v(-105.82, 63.1) * mm});
            skLineSegment(sketch, "E697", {"start": v(-105.82, 63.1) * mm, "end": v(-106.59, 64.12) * mm});
            skLineSegment(sketch, "E698", {"start": v(-106.59, 64.12) * mm, "end": v(-106.96, 64.64) * mm});
            skLineSegment(sketch, "E699", {"start": v(-106.96, 64.64) * mm, "end": v(-106.07, 65.98) * mm});
            skLineSegment(sketch, "E700", {"start": v(-106.07, 65.98) * mm, "end": v(-105.44, 65.84) * mm});
            skLineSegment(sketch, "E701", {"start": v(-105.44, 65.84) * mm, "end": v(-104.2, 65.53) * mm});
            skLineSegment(sketch, "E702", {"start": v(-104.2, 65.53) * mm, "end": v(-103.6, 65.36) * mm});
            skLineSegment(sketch, "E703", {"start": v(-103.6, 65.36) * mm, "end": v(-102.66, 66.7) * mm});
            skLineSegment(sketch, "E704", {"start": v(-102.66, 66.7) * mm, "end": v(-103.03, 67.22) * mm});
            skLineSegment(sketch, "E705", {"start": v(-103.03, 67.22) * mm, "end": v(-103.76, 68.27) * mm});
            skLineSegment(sketch, "E706", {"start": v(-103.76, 68.27) * mm, "end": v(-104.1, 68.8) * mm});
            skLineSegment(sketch, "E707", {"start": v(-104.1, 68.8) * mm, "end": v(-103.16, 70.1) * mm});
            skLineSegment(sketch, "E708", {"start": v(-103.16, 70.1) * mm, "end": v(-102.54, 69.94) * mm});
            skLineSegment(sketch, "E709", {"start": v(-102.54, 69.94) * mm, "end": v(-101.32, 69.57) * mm});
            skLineSegment(sketch, "E710", {"start": v(-101.32, 69.57) * mm, "end": v(-100.72, 69.38) * mm});
            skLineSegment(sketch, "E711", {"start": v(-100.72, 69.38) * mm, "end": v(-99.72, 70.69) * mm});
            skLineSegment(sketch, "E712", {"start": v(-99.72, 70.69) * mm, "end": v(-100.07, 71.22) * mm});
            skLineSegment(sketch, "E713", {"start": v(-100.07, 71.22) * mm, "end": v(-100.75, 72.3) * mm});
            skLineSegment(sketch, "E714", {"start": v(-100.75, 72.3) * mm, "end": v(-101.08, 72.85) * mm});
            skLineSegment(sketch, "E715", {"start": v(-101.08, 72.85) * mm, "end": v(-100.08, 74.11) * mm});
            skLineSegment(sketch, "E716", {"start": v(-100.08, 74.11) * mm, "end": v(-99.47, 73.91) * mm});
            skLineSegment(sketch, "E717", {"start": v(-99.47, 73.91) * mm, "end": v(-98.26, 73.5) * mm});
            skLineSegment(sketch, "E718", {"start": v(-98.26, 73.5) * mm, "end": v(-97.67, 73.28) * mm});
            skLineSegment(sketch, "E719", {"start": v(-97.67, 73.28) * mm, "end": v(-96.62, 74.54) * mm});
            skLineSegment(sketch, "E720", {"start": v(-96.62, 74.54) * mm, "end": v(-96.94, 75.08) * mm});
            skLineSegment(sketch, "E721", {"start": v(-96.94, 75.08) * mm, "end": v(-97.58, 76.2) * mm});
            skLineSegment(sketch, "E722", {"start": v(-97.58, 76.2) * mm, "end": v(-97.88, 76.76) * mm});
            skLineSegment(sketch, "E723", {"start": v(-97.88, 76.76) * mm, "end": v(-96.83, 77.98) * mm});
            skLineSegment(sketch, "E724", {"start": v(-96.83, 77.98) * mm, "end": v(-96.23, 77.75) * mm});
            skLineSegment(sketch, "E725", {"start": v(-96.23, 77.75) * mm, "end": v(-95.04, 77.29) * mm});
            skLineSegment(sketch, "E726", {"start": v(-95.04, 77.29) * mm, "end": v(-94.45, 77.04) * mm});
            skLineSegment(sketch, "E727", {"start": v(-94.45, 77.04) * mm, "end": v(-93.35, 78.26) * mm});
            skLineSegment(sketch, "E728", {"start": v(-93.35, 78.26) * mm, "end": v(-93.66, 78.81) * mm});
            skLineSegment(sketch, "E729", {"start": v(-93.66, 78.81) * mm, "end": v(-94.24, 79.95) * mm});
            skLineSegment(sketch, "E730", {"start": v(-94.24, 79.95) * mm, "end": v(-94.52, 80.53) * mm});
            skLineSegment(sketch, "E731", {"start": v(-94.52, 80.53) * mm, "end": v(-93.42, 81.7) * mm});
            skLineSegment(sketch, "E732", {"start": v(-93.42, 81.7) * mm, "end": v(-92.82, 81.45) * mm});
            skLineSegment(sketch, "E733", {"start": v(-92.82, 81.45) * mm, "end": v(-91.66, 80.93) * mm});
            skLineSegment(sketch, "E734", {"start": v(-91.66, 80.93) * mm, "end": v(-91.08, 80.66) * mm});
            skLineSegment(sketch, "E735", {"start": v(-91.08, 80.66) * mm, "end": v(-89.93, 81.83) * mm});
            skLineSegment(sketch, "E736", {"start": v(-89.93, 81.83) * mm, "end": v(-90.2, 82.4) * mm});
            skLineSegment(sketch, "E737", {"start": v(-90.2, 82.4) * mm, "end": v(-90.74, 83.56) * mm});
            skLineSegment(sketch, "E738", {"start": v(-90.74, 83.56) * mm, "end": v(-91, 84.15) * mm});
            skLineSegment(sketch, "E739", {"start": v(-91, 84.15) * mm, "end": v(-89.85, 85.27) * mm});
            skLineSegment(sketch, "E740", {"start": v(-89.85, 85.27) * mm, "end": v(-89.26, 85) * mm});
            skLineSegment(sketch, "E741", {"start": v(-89.26, 85) * mm, "end": v(-88.12, 84.43) * mm});
            skLineSegment(sketch, "E742", {"start": v(-88.12, 84.43) * mm, "end": v(-87.56, 84.14) * mm});
            skLineSegment(sketch, "E743", {"start": v(-87.56, 84.14) * mm, "end": v(-86.36, 85.26) * mm});
            skLineSegment(sketch, "E744", {"start": v(-86.36, 85.26) * mm, "end": v(-86.61, 85.84) * mm});
            skLineSegment(sketch, "E745", {"start": v(-86.61, 85.84) * mm, "end": v(-87.1, 87.02) * mm});
            skLineSegment(sketch, "E746", {"start": v(-87.1, 87.02) * mm, "end": v(-87.33, 87.62) * mm});
            skLineSegment(sketch, "E747", {"start": v(-87.33, 87.62) * mm, "end": v(-86.13, 88.7) * mm});
            skLineSegment(sketch, "E748", {"start": v(-86.13, 88.7) * mm, "end": v(-85.56, 88.4) * mm});
            skLineSegment(sketch, "E749", {"start": v(-85.56, 88.4) * mm, "end": v(-84.44, 87.78) * mm});
            skLineSegment(sketch, "E750", {"start": v(-84.44, 87.78) * mm, "end": v(-83.9, 87.46) * mm});
            skLineSegment(sketch, "E751", {"start": v(-83.9, 87.46) * mm, "end": v(-82.64, 88.53) * mm});
            skLineSegment(sketch, "E752", {"start": v(-82.64, 88.53) * mm, "end": v(-82.87, 89.12) * mm});
            skLineSegment(sketch, "E753", {"start": v(-82.87, 89.12) * mm, "end": v(-83.3, 90.32) * mm});
            skLineSegment(sketch, "E754", {"start": v(-83.3, 90.32) * mm, "end": v(-83.51, 90.93) * mm});
            skLineSegment(sketch, "E755", {"start": v(-83.51, 90.93) * mm, "end": v(-82.27, 91.95) * mm});
            skLineSegment(sketch, "E756", {"start": v(-82.27, 91.95) * mm, "end": v(-81.7, 91.63) * mm});
            skLineSegment(sketch, "E757", {"start": v(-81.7, 91.63) * mm, "end": v(-80.62, 90.96) * mm});
            skLineSegment(sketch, "E758", {"start": v(-80.62, 90.96) * mm, "end": v(-80.09, 90.62) * mm});
            skLineSegment(sketch, "E759", {"start": v(-80.09, 90.62) * mm, "end": v(-78.8, 91.63) * mm});
            skLineSegment(sketch, "E760", {"start": v(-78.8, 91.63) * mm, "end": v(-79, 92.23) * mm});
            skLineSegment(sketch, "E761", {"start": v(-79, 92.23) * mm, "end": v(-79.38, 93.45) * mm});
            skLineSegment(sketch, "E762", {"start": v(-79.38, 93.45) * mm, "end": v(-79.56, 94.07) * mm});
            skLineSegment(sketch, "E763", {"start": v(-79.56, 94.07) * mm, "end": v(-78.27, 95.04) * mm});
            skLineSegment(sketch, "E764", {"start": v(-78.27, 95.04) * mm, "end": v(-77.73, 94.7) * mm});
            skLineSegment(sketch, "E765", {"start": v(-77.73, 94.7) * mm, "end": v(-76.67, 93.98) * mm});
            skLineSegment(sketch, "E766", {"start": v(-76.67, 93.98) * mm, "end": v(-76.15, 93.62) * mm});
            skLineSegment(sketch, "E767", {"start": v(-76.15, 93.62) * mm, "end": v(-74.81, 94.57) * mm});
            skLineSegment(sketch, "E768", {"start": v(-74.81, 94.57) * mm, "end": v(-75, 95.18) * mm});
            skLineSegment(sketch, "E769", {"start": v(-75, 95.18) * mm, "end": v(-75.32, 96.41) * mm});
            skLineSegment(sketch, "E770", {"start": v(-75.32, 96.41) * mm, "end": v(-75.47, 97.04) * mm});
            skLineSegment(sketch, "E771", {"start": v(-75.47, 97.04) * mm, "end": v(-74.14, 97.95) * mm});
            skLineSegment(sketch, "E772", {"start": v(-74.14, 97.95) * mm, "end": v(-73.62, 97.58) * mm});
            skLineSegment(sketch, "E773", {"start": v(-73.62, 97.58) * mm, "end": v(-72.59, 96.83) * mm});
            skLineSegment(sketch, "E774", {"start": v(-72.59, 96.83) * mm, "end": v(-72.09, 96.44) * mm});
            skLineSegment(sketch, "E775", {"start": v(-72.09, 96.44) * mm, "end": v(-70.7, 97.34) * mm});
            skLineSegment(sketch, "E776", {"start": v(-70.7, 97.34) * mm, "end": v(-70.86, 97.96) * mm});
            skLineSegment(sketch, "E777", {"start": v(-70.86, 97.96) * mm, "end": v(-71.14, 99.2) * mm});
            skLineSegment(sketch, "E778", {"start": v(-71.14, 99.2) * mm, "end": v(-71.27, 99.83) * mm});
            skLineSegment(sketch, "E779", {"start": v(-71.27, 99.83) * mm, "end": v(-69.9, 100.69) * mm});
            skLineSegment(sketch, "E780", {"start": v(-69.9, 100.69) * mm, "end": v(-69.39, 100.3) * mm});
            skLineSegment(sketch, "E781", {"start": v(-69.39, 100.3) * mm, "end": v(-68.4, 99.5) * mm});
            skLineSegment(sketch, "E782", {"start": v(-68.4, 99.5) * mm, "end": v(-67.9, 99.1) * mm});
            skLineSegment(sketch, "E783", {"start": v(-67.9, 99.1) * mm, "end": v(-66.5, 99.93) * mm});
            skLineSegment(sketch, "E784", {"start": v(-66.5, 99.93) * mm, "end": v(-66.62, 100.55) * mm});
            skLineSegment(sketch, "E785", {"start": v(-66.62, 100.55) * mm, "end": v(-66.84, 101.8) * mm});
            skLineSegment(sketch, "E786", {"start": v(-66.84, 101.8) * mm, "end": v(-66.94, 102.44) * mm});
            skLineSegment(sketch, "E787", {"start": v(-66.94, 102.44) * mm, "end": v(-65.54, 103.24) * mm});
            skLineSegment(sketch, "E788", {"start": v(-65.54, 103.24) * mm, "end": v(-65.05, 102.83) * mm});
            skLineSegment(sketch, "E789", {"start": v(-65.05, 102.83) * mm, "end": v(-64.08, 101.99) * mm});
            skLineSegment(sketch, "E790", {"start": v(-64.08, 101.99) * mm, "end": v(-63.62, 101.56) * mm});
            skLineSegment(sketch, "E791", {"start": v(-63.62, 101.56) * mm, "end": v(-62.17, 102.34) * mm});
            skLineSegment(sketch, "E792", {"start": v(-62.17, 102.34) * mm, "end": v(-62.27, 102.96) * mm});
            skLineSegment(sketch, "E793", {"start": v(-62.27, 102.96) * mm, "end": v(-62.44, 104.23) * mm});
            skLineSegment(sketch, "E794", {"start": v(-62.44, 104.23) * mm, "end": v(-62.51, 104.87) * mm});
            skLineSegment(sketch, "E795", {"start": v(-62.51, 104.87) * mm, "end": v(-61.08, 105.6) * mm});
            skLineSegment(sketch, "E796", {"start": v(-61.08, 105.6) * mm, "end": v(-60.6, 105.17) * mm});
            skLineSegment(sketch, "E797", {"start": v(-60.6, 105.17) * mm, "end": v(-59.67, 104.29) * mm});
            skLineSegment(sketch, "E798", {"start": v(-59.67, 104.29) * mm, "end": v(-59.23, 103.84) * mm});
            skLineSegment(sketch, "E799", {"start": v(-59.23, 103.84) * mm, "end": v(-57.75, 104.56) * mm});
            skLineSegment(sketch, "E800", {"start": v(-57.75, 104.56) * mm, "end": v(-57.82, 105.19) * mm});
            skLineSegment(sketch, "E801", {"start": v(-57.82, 105.19) * mm, "end": v(-57.94, 106.46) * mm});
            skLineSegment(sketch, "E802", {"start": v(-57.94, 106.46) * mm, "end": v(-57.98, 107.1) * mm});
            skLineSegment(sketch, "E803", {"start": v(-57.98, 107.1) * mm, "end": v(-56.51, 107.77) * mm});
            skLineSegment(sketch, "E804", {"start": v(-56.51, 107.77) * mm, "end": v(-56.06, 107.32) * mm});
            skLineSegment(sketch, "E805", {"start": v(-56.06, 107.32) * mm, "end": v(-55.17, 106.4) * mm});
            skLineSegment(sketch, "E806", {"start": v(-55.17, 106.4) * mm, "end": v(-54.74, 105.93) * mm});
            skLineSegment(sketch, "E807", {"start": v(-54.74, 105.93) * mm, "end": v(-53.23, 106.59) * mm});
            skLineSegment(sketch, "E808", {"start": v(-53.23, 106.59) * mm, "end": v(-53.28, 107.22) * mm});
            skLineSegment(sketch, "E809", {"start": v(-53.28, 107.22) * mm, "end": v(-53.34, 108.5) * mm});
            skLineSegment(sketch, "E810", {"start": v(-53.34, 108.5) * mm, "end": v(-53.36, 109.14) * mm});
            skLineSegment(sketch, "E811", {"start": v(-53.36, 109.14) * mm, "end": v(-51.87, 109.74) * mm});
            skLineSegment(sketch, "E812", {"start": v(-51.87, 109.74) * mm, "end": v(-51.43, 109.27) * mm});
            skLineSegment(sketch, "E813", {"start": v(-51.43, 109.27) * mm, "end": v(-50.58, 108.32) * mm});
            skLineSegment(sketch, "E814", {"start": v(-50.58, 108.32) * mm, "end": v(-50.17, 107.83) * mm});
            skLineSegment(sketch, "E815", {"start": v(-50.17, 107.83) * mm, "end": v(-48.64, 108.42) * mm});
            skLineSegment(sketch, "E816", {"start": v(-48.64, 108.42) * mm, "end": v(-48.66, 109.05) * mm});
            skLineSegment(sketch, "E817", {"start": v(-48.66, 109.05) * mm, "end": v(-48.66, 110.33) * mm});
            skLineSegment(sketch, "E818", {"start": v(-48.66, 110.33) * mm, "end": v(-48.65, 110.97) * mm});
            skLineSegment(sketch, "E819", {"start": v(-48.65, 110.97) * mm, "end": v(-47.14, 111.52) * mm});
            skLineSegment(sketch, "E820", {"start": v(-47.14, 111.52) * mm, "end": v(-46.72, 111.03) * mm});
            skLineSegment(sketch, "E821", {"start": v(-46.72, 111.03) * mm, "end": v(-45.91, 110.04) * mm});
            skLineSegment(sketch, "E822", {"start": v(-45.91, 110.04) * mm, "end": v(-45.53, 109.54) * mm});
            skLineSegment(sketch, "E823", {"start": v(-45.53, 109.54) * mm, "end": v(-43.97, 110.06) * mm});
            skLineSegment(sketch, "E824", {"start": v(-43.97, 110.06) * mm, "end": v(-43.96, 110.7) * mm});
            skLineSegment(sketch, "E825", {"start": v(-43.96, 110.7) * mm, "end": v(-43.91, 111.97) * mm});
            skLineSegment(sketch, "E826", {"start": v(-43.91, 111.97) * mm, "end": v(-43.87, 112.6) * mm});
            skLineSegment(sketch, "E827", {"start": v(-43.87, 112.6) * mm, "end": v(-42.34, 113.09) * mm});
            skLineSegment(sketch, "E828", {"start": v(-42.34, 113.09) * mm, "end": v(-41.94, 112.58) * mm});
            skLineSegment(sketch, "E829", {"start": v(-41.94, 112.58) * mm, "end": v(-41.18, 111.55) * mm});
            skLineSegment(sketch, "E830", {"start": v(-41.18, 111.55) * mm, "end": v(-40.81, 111.04) * mm});
            skLineSegment(sketch, "E831", {"start": v(-40.81, 111.04) * mm, "end": v(-39.23, 111.5) * mm});
            skLineSegment(sketch, "E832", {"start": v(-39.23, 111.5) * mm, "end": v(-39.2, 112.12) * mm});
            skLineSegment(sketch, "E833", {"start": v(-39.2, 112.12) * mm, "end": v(-39.1, 113.4) * mm});
            skLineSegment(sketch, "E834", {"start": v(-39.1, 113.4) * mm, "end": v(-39.03, 114.04) * mm});
            skLineSegment(sketch, "E835", {"start": v(-39.03, 114.04) * mm, "end": v(-37.47, 114.45) * mm});
            skLineSegment(sketch, "E836", {"start": v(-37.47, 114.45) * mm, "end": v(-37.1, 113.93) * mm});
            skLineSegment(sketch, "E837", {"start": v(-37.1, 113.93) * mm, "end": v(-36.38, 112.87) * mm});
            skLineSegment(sketch, "E838", {"start": v(-36.38, 112.87) * mm, "end": v(-36.04, 112.34) * mm});
            skLineSegment(sketch, "E839", {"start": v(-36.04, 112.34) * mm, "end": v(-34.44, 112.72) * mm});
            skLineSegment(sketch, "E840", {"start": v(-34.44, 112.72) * mm, "end": v(-34.38, 113.35) * mm});
            skLineSegment(sketch, "E841", {"start": v(-34.38, 113.35) * mm, "end": v(-34.22, 114.62) * mm});
            skLineSegment(sketch, "E842", {"start": v(-34.22, 114.62) * mm, "end": v(-34.13, 115.26) * mm});
            skLineSegment(sketch, "E843", {"start": v(-34.13, 115.26) * mm, "end": v(-32.55, 115.6) * mm});
            skLineSegment(sketch, "E844", {"start": v(-32.55, 115.6) * mm, "end": v(-32.2, 115.06) * mm});
            skLineSegment(sketch, "E845", {"start": v(-32.2, 115.06) * mm, "end": v(-31.53, 113.98) * mm});
            skLineSegment(sketch, "E846", {"start": v(-31.53, 113.98) * mm, "end": v(-31.21, 113.43) * mm});
            skLineSegment(sketch, "E847", {"start": v(-31.21, 113.43) * mm, "end": v(-29.6, 113.75) * mm});
            skLineSegment(sketch, "E848", {"start": v(-29.6, 113.75) * mm, "end": v(-29.5, 114.38) * mm});
            skLineSegment(sketch, "E849", {"start": v(-29.5, 114.38) * mm, "end": v(-29.3, 115.64) * mm});
            skLineSegment(sketch, "E850", {"start": v(-29.3, 115.64) * mm, "end": v(-29.18, 116.27) * mm});
            skLineSegment(sketch, "E851", {"start": v(-29.18, 116.27) * mm, "end": v(-27.6, 116.54) * mm});
            skLineSegment(sketch, "E852", {"start": v(-27.6, 116.54) * mm, "end": v(-27.26, 116) * mm});
            skLineSegment(sketch, "E853", {"start": v(-27.26, 116) * mm, "end": v(-26.64, 114.88) * mm});
            skLineSegment(sketch, "E854", {"start": v(-26.64, 114.88) * mm, "end": v(-26.34, 114.32) * mm});
            skLineSegment(sketch, "E855", {"start": v(-26.34, 114.32) * mm, "end": v(-24.72, 114.57) * mm});
            skLineSegment(sketch, "E856", {"start": v(-24.72, 114.57) * mm, "end": v(-24.6, 115.19) * mm});
            skLineSegment(sketch, "E857", {"start": v(-24.6, 115.19) * mm, "end": v(-24.34, 116.44) * mm});
            skLineSegment(sketch, "E858", {"start": v(-24.34, 116.44) * mm, "end": v(-24.2, 117.06) * mm});
            skLineSegment(sketch, "E859", {"start": v(-24.2, 117.06) * mm, "end": v(-22.6, 117.27) * mm});
            skLineSegment(sketch, "E860", {"start": v(-22.6, 117.27) * mm, "end": v(-22.3, 116.7) * mm});
            skLineSegment(sketch, "E861", {"start": v(-22.3, 116.7) * mm, "end": v(-21.71, 115.57) * mm});
            skLineSegment(sketch, "E862", {"start": v(-21.71, 115.57) * mm, "end": v(-21.44, 115) * mm});
            skLineSegment(sketch, "E863", {"start": v(-21.44, 115) * mm, "end": v(-19.8, 115.17) * mm});
            skLineSegment(sketch, "E864", {"start": v(-19.8, 115.17) * mm, "end": v(-19.66, 115.8) * mm});
            skLineSegment(sketch, "E865", {"start": v(-19.66, 115.8) * mm, "end": v(-19.35, 117.03) * mm});
            skLineSegment(sketch, "E866", {"start": v(-19.35, 117.03) * mm, "end": v(-19.17, 117.65) * mm});
            skLineSegment(sketch, "E867", {"start": v(-19.17, 117.65) * mm, "end": v(-17.57, 117.79) * mm});
            skLineSegment(sketch, "E868", {"start": v(-17.57, 117.79) * mm, "end": v(-17.29, 117.2) * mm});
            skLineSegment(sketch, "E869", {"start": v(-17.29, 117.2) * mm, "end": v(-16.76, 116.05) * mm});
            skLineSegment(sketch, "E870", {"start": v(-16.76, 116.05) * mm, "end": v(-16.52, 115.46) * mm});
            skLineSegment(sketch, "E871", {"start": v(-16.52, 115.46) * mm, "end": v(-14.87, 115.57) * mm});
            skLineSegment(sketch, "E872", {"start": v(-14.87, 115.57) * mm, "end": v(-14.7, 116.18) * mm});
            skLineSegment(sketch, "E873", {"start": v(-14.7, 116.18) * mm, "end": v(-14.34, 117.4) * mm});
            skLineSegment(sketch, "E874", {"start": v(-14.34, 117.4) * mm, "end": v(-14.14, 118.02) * mm});
            skLineSegment(sketch, "E875", {"start": v(-14.14, 118.02) * mm, "end": v(-12.53, 118.09) * mm});
            skLineSegment(sketch, "E876", {"start": v(-12.53, 118.09) * mm, "end": v(-12.27, 117.5) * mm});
            skLineSegment(sketch, "E877", {"start": v(-12.27, 117.5) * mm, "end": v(-11.8, 116.31) * mm});
            skLineSegment(sketch, "E878", {"start": v(-11.8, 116.31) * mm, "end": v(-11.57, 115.72) * mm});
            skLineSegment(sketch, "E879", {"start": v(-11.57, 115.72) * mm, "end": v(-9.93, 115.76) * mm});
            skLineSegment(sketch, "E880", {"start": v(-9.93, 115.76) * mm, "end": v(-9.74, 116.36) * mm});
            skLineSegment(sketch, "E881", {"start": v(-9.74, 116.36) * mm, "end": v(-9.31, 117.57) * mm});
            skLineSegment(sketch, "E882", {"start": v(-9.31, 117.57) * mm, "end": v(-9.09, 118.17) * mm});
            skLineSegment(sketch, "E883", {"start": v(-9.09, 118.17) * mm, "end": v(-7.48, 118.17) * mm});
            skLineSegment(sketch, "E884", {"start": v(-7.48, 118.17) * mm, "end": v(-7.25, 117.57) * mm});
            skLineSegment(sketch, "E885", {"start": v(-7.25, 117.57) * mm, "end": v(-6.82, 116.37) * mm});
            skLineSegment(sketch, "E886", {"start": v(-6.82, 116.37) * mm, "end": v(-6.63, 115.77) * mm});
            skLineSegment(sketch, "E887", {"start": v(-6.63, 115.77) * mm, "end": v(-4.98, 115.74) * mm});
            skLineSegment(sketch, "E888", {"start": v(-4.98, 115.74) * mm, "end": v(-4.76, 116.33) * mm});
            skLineSegment(sketch, "E889", {"start": v(-4.76, 116.33) * mm, "end": v(-4.29, 117.52) * mm});
            skLineSegment(sketch, "E890", {"start": v(-4.29, 117.52) * mm, "end": v(-4.04, 118.1) * mm});
            skLineSegment(sketch, "E891", {"start": v(-4.04, 118.1) * mm, "end": v(-2.43, 118.04) * mm});
            skLineSegment(sketch, "E892", {"start": v(-2.43, 118.04) * mm, "end": v(-2.23, 117.43) * mm});
            skLineSegment(sketch, "E893", {"start": v(-2.23, 117.43) * mm, "end": v(-1.85, 116.21) * mm});
            skLineSegment(sketch, "E894", {"start": v(-1.85, 116.21) * mm, "end": v(-1.68, 115.6) * mm});
            skLineSegment(sketch, "E895", {"start": v(-1.68, 115.6) * mm, "end": v(-0.04, 115.5) * mm});
            skLineSegment(sketch, "E896", {"start": v(-0.04, 115.5) * mm, "end": v(0.2, 116.08) * mm});
            skLineSegment(sketch, "E897", {"start": v(0.2, 116.08) * mm, "end": v(0.73, 117.25) * mm});
            skLineSegment(sketch, "E898", {"start": v(0.73, 117.25) * mm, "end": v(1, 117.83) * mm});
            skLineSegment(sketch, "E899", {"start": v(1, 117.83) * mm, "end": v(2.61, 117.7) * mm});
            skLineSegment(sketch, "E900", {"start": v(2.61, 117.7) * mm, "end": v(2.79, 117.08) * mm});
            skLineSegment(sketch, "E901", {"start": v(2.79, 117.08) * mm, "end": v(3.1, 115.84) * mm});
            skLineSegment(sketch, "E902", {"start": v(3.1, 115.84) * mm, "end": v(3.25, 115.22) * mm});
            skLineSegment(sketch, "E903", {"start": v(3.25, 115.22) * mm, "end": v(4.89, 115.05) * mm});
            skLineSegment(sketch, "E904", {"start": v(4.89, 115.05) * mm, "end": v(5.16, 115.63) * mm});
            skLineSegment(sketch, "E905", {"start": v(5.16, 115.63) * mm, "end": v(5.73, 116.77) * mm});
            skLineSegment(sketch, "E906", {"start": v(5.73, 116.77) * mm, "end": v(6.03, 117.33) * mm});
            skLineSegment(sketch, "E907", {"start": v(6.03, 117.33) * mm, "end": v(7.63, 117.13) * mm});
            skLineSegment(sketch, "E908", {"start": v(7.63, 117.13) * mm, "end": v(7.78, 116.5) * mm});
            skLineSegment(sketch, "E909", {"start": v(7.78, 116.5) * mm, "end": v(8.05, 115.26) * mm});
            skLineSegment(sketch, "E910", {"start": v(8.05, 115.26) * mm, "end": v(8.17, 114.64) * mm});
            skLineSegment(sketch, "E911", {"start": v(8.17, 114.64) * mm, "end": v(9.8, 114.4) * mm});
            skLineSegment(sketch, "E912", {"start": v(9.8, 114.4) * mm, "end": v(10.09, 114.96) * mm});
            skLineSegment(sketch, "E913", {"start": v(10.09, 114.96) * mm, "end": v(10.7, 116.07) * mm});
            skLineSegment(sketch, "E914", {"start": v(10.7, 116.07) * mm, "end": v(11.03, 116.63) * mm});
            skLineSegment(sketch, "E915", {"start": v(11.03, 116.63) * mm, "end": v(12.62, 116.36) * mm});
            skLineSegment(sketch, "E916", {"start": v(12.62, 116.36) * mm, "end": v(12.74, 115.72) * mm});
            skLineSegment(sketch, "E917", {"start": v(12.74, 115.72) * mm, "end": v(12.96, 114.47) * mm});
            skLineSegment(sketch, "E918", {"start": v(12.96, 114.47) * mm, "end": v(13.05, 113.84) * mm});
            skLineSegment(sketch, "E919", {"start": v(13.05, 113.84) * mm, "end": v(14.67, 113.53) * mm});
            skLineSegment(sketch, "E920", {"start": v(14.67, 113.53) * mm, "end": v(14.98, 114.08) * mm});
            skLineSegment(sketch, "E921", {"start": v(14.98, 114.08) * mm, "end": v(15.65, 115.17) * mm});
            skLineSegment(sketch, "E922", {"start": v(15.65, 115.17) * mm, "end": v(16, 115.7) * mm});
            skLineSegment(sketch, "E923", {"start": v(16, 115.7) * mm, "end": v(17.57, 115.37) * mm});
            skLineSegment(sketch, "E924", {"start": v(17.57, 115.37) * mm, "end": v(17.67, 114.73) * mm});
            skLineSegment(sketch, "E925", {"start": v(17.67, 114.73) * mm, "end": v(17.83, 113.47) * mm});
            skLineSegment(sketch, "E926", {"start": v(17.83, 113.47) * mm, "end": v(17.9, 112.84) * mm});
            skLineSegment(sketch, "E927", {"start": v(17.9, 112.84) * mm, "end": v(19.5, 112.46) * mm});
            skLineSegment(sketch, "E928", {"start": v(19.5, 112.46) * mm, "end": v(19.84, 112.99) * mm});
            skLineSegment(sketch, "E929", {"start": v(19.84, 112.99) * mm, "end": v(20.55, 114.05) * mm});
            skLineSegment(sketch, "E930", {"start": v(20.55, 114.05) * mm, "end": v(20.92, 114.57) * mm});
            skLineSegment(sketch, "E931", {"start": v(20.92, 114.57) * mm, "end": v(22.48, 114.17) * mm});
            skLineSegment(sketch, "E932", {"start": v(22.48, 114.17) * mm, "end": v(22.55, 113.53) * mm});
            skLineSegment(sketch, "E933", {"start": v(22.55, 113.53) * mm, "end": v(22.66, 112.26) * mm});
            skLineSegment(sketch, "E934", {"start": v(22.66, 112.26) * mm, "end": v(22.7, 111.62) * mm});
            skLineSegment(sketch, "E935", {"start": v(22.7, 111.62) * mm, "end": v(24.28, 111.18) * mm});
            skLineSegment(sketch, "E936", {"start": v(24.28, 111.18) * mm, "end": v(24.64, 111.7) * mm});
            skLineSegment(sketch, "E937", {"start": v(24.64, 111.7) * mm, "end": v(25.4, 112.72) * mm});
            skLineSegment(sketch, "E938", {"start": v(25.4, 112.72) * mm, "end": v(25.8, 113.23) * mm});
            skLineSegment(sketch, "E939", {"start": v(25.8, 113.23) * mm, "end": v(27.33, 112.76) * mm});
            skLineSegment(sketch, "E940", {"start": v(27.33, 112.76) * mm, "end": v(27.37, 112.12) * mm});
            skLineSegment(sketch, "E941", {"start": v(27.37, 112.12) * mm, "end": v(27.43, 110.84) * mm});
            skLineSegment(sketch, "E942", {"start": v(27.43, 110.84) * mm, "end": v(27.44, 110.2) * mm});
            skLineSegment(sketch, "E943", {"start": v(27.44, 110.2) * mm, "end": v(29, 109.7) * mm});
            skLineSegment(sketch, "E944", {"start": v(29, 109.7) * mm, "end": v(29.38, 110.2) * mm});
            skLineSegment(sketch, "E945", {"start": v(29.38, 110.2) * mm, "end": v(30.18, 111.2) * mm});
            skLineSegment(sketch, "E946", {"start": v(30.18, 111.2) * mm, "end": v(30.6, 111.68) * mm});
            skLineSegment(sketch, "E947", {"start": v(30.6, 111.68) * mm, "end": v(32.12, 111.15) * mm});
            skLineSegment(sketch, "E948", {"start": v(32.12, 111.15) * mm, "end": v(32.13, 110.5) * mm});
            skLineSegment(sketch, "E949", {"start": v(32.13, 110.5) * mm, "end": v(32.13, 109.23) * mm});
            skLineSegment(sketch, "E950", {"start": v(32.13, 109.23) * mm, "end": v(32.11, 108.6) * mm});
            skLineSegment(sketch, "E951", {"start": v(32.11, 108.6) * mm, "end": v(33.65, 108.01) * mm});
            skLineSegment(sketch, "E952", {"start": v(33.65, 108.01) * mm, "end": v(34.06, 108.5) * mm});
            skLineSegment(sketch, "E953", {"start": v(34.06, 108.5) * mm, "end": v(34.9, 109.46) * mm});
            skLineSegment(sketch, "E954", {"start": v(34.9, 109.46) * mm, "end": v(35.34, 109.93) * mm});
            skLineSegment(sketch, "E955", {"start": v(35.34, 109.93) * mm, "end": v(36.83, 109.33) * mm});
            skLineSegment(sketch, "E956", {"start": v(36.83, 109.33) * mm, "end": v(36.82, 108.69) * mm});
            skLineSegment(sketch, "E957", {"start": v(36.82, 108.69) * mm, "end": v(36.76, 107.41) * mm});
            skLineSegment(sketch, "E958", {"start": v(36.76, 107.41) * mm, "end": v(36.72, 106.78) * mm});
            skLineSegment(sketch, "E959", {"start": v(36.72, 106.78) * mm, "end": v(38.23, 106.13) * mm});
            skLineSegment(sketch, "E960", {"start": v(38.23, 106.13) * mm, "end": v(38.66, 106.6) * mm});
            skLineSegment(sketch, "E961", {"start": v(38.66, 106.6) * mm, "end": v(39.54, 107.52) * mm});
            skLineSegment(sketch, "E962", {"start": v(39.54, 107.52) * mm, "end": v(40, 107.98) * mm});
            skLineSegment(sketch, "E963", {"start": v(40, 107.98) * mm, "end": v(41.46, 107.31) * mm});
            skLineSegment(sketch, "E964", {"start": v(41.46, 107.31) * mm, "end": v(41.42, 106.67) * mm});
            skLineSegment(sketch, "E965", {"start": v(41.42, 106.67) * mm, "end": v(41.3, 105.4) * mm});
            skLineSegment(sketch, "E966", {"start": v(41.3, 105.4) * mm, "end": v(41.24, 104.77) * mm});
            skLineSegment(sketch, "E967", {"start": v(41.24, 104.77) * mm, "end": v(42.72, 104.06) * mm});
            skLineSegment(sketch, "E968", {"start": v(42.72, 104.06) * mm, "end": v(43.17, 104.5) * mm});
            skLineSegment(sketch, "E969", {"start": v(43.17, 104.5) * mm, "end": v(44.09, 105.4) * mm});
            skLineSegment(sketch, "E970", {"start": v(44.09, 105.4) * mm, "end": v(44.56, 105.83) * mm});
            skLineSegment(sketch, "E971", {"start": v(44.56, 105.83) * mm, "end": v(46, 105.1) * mm});
            skLineSegment(sketch, "E972", {"start": v(46, 105.1) * mm, "end": v(45.93, 104.46) * mm});
            skLineSegment(sketch, "E973", {"start": v(45.93, 104.46) * mm, "end": v(45.77, 103.2) * mm});
            skLineSegment(sketch, "E974", {"start": v(45.77, 103.2) * mm, "end": v(45.67, 102.57) * mm});
            skLineSegment(sketch, "E975", {"start": v(45.67, 102.57) * mm, "end": v(47.12, 101.8) * mm});
            skLineSegment(sketch, "E976", {"start": v(47.12, 101.8) * mm, "end": v(47.59, 102.23) * mm});
            skLineSegment(sketch, "E977", {"start": v(47.59, 102.23) * mm, "end": v(48.55, 103.07) * mm});
            skLineSegment(sketch, "E978", {"start": v(48.55, 103.07) * mm, "end": v(49.04, 103.48) * mm});
            skLineSegment(sketch, "E979", {"start": v(49.04, 103.48) * mm, "end": v(50.44, 102.7) * mm});
            skLineSegment(sketch, "E980", {"start": v(50.44, 102.7) * mm, "end": v(50.35, 102.06) * mm});
            skLineSegment(sketch, "E981", {"start": v(50.35, 102.06) * mm, "end": v(50.13, 100.8) * mm});
            skLineSegment(sketch, "E982", {"start": v(50.13, 100.8) * mm, "end": v(50, 100.18) * mm});
            skLineSegment(sketch, "E983", {"start": v(50, 100.18) * mm, "end": v(51.42, 99.35) * mm});
            skLineSegment(sketch, "E984", {"start": v(51.42, 99.35) * mm, "end": v(51.9, 99.76) * mm});
            skLineSegment(sketch, "E985", {"start": v(51.9, 99.76) * mm, "end": v(52.9, 100.56) * mm});
            skLineSegment(sketch, "E986", {"start": v(52.9, 100.56) * mm, "end": v(53.4, 100.95) * mm});
            skLineSegment(sketch, "E987", {"start": v(53.4, 100.95) * mm, "end": v(54.78, 100.1) * mm});
            skLineSegment(sketch, "E988", {"start": v(54.78, 100.1) * mm, "end": v(54.66, 99.47) * mm});
            skLineSegment(sketch, "E989", {"start": v(54.66, 99.47) * mm, "end": v(54.38, 98.22) * mm});
            skLineSegment(sketch, "E990", {"start": v(54.38, 98.22) * mm, "end": v(54.23, 97.6) * mm});
            skLineSegment(sketch, "E991", {"start": v(54.23, 97.6) * mm, "end": v(55.61, 96.71) * mm});
            skLineSegment(sketch, "E992", {"start": v(55.61, 96.71) * mm, "end": v(56.11, 97.1) * mm});
            skLineSegment(sketch, "E993", {"start": v(56.11, 97.1) * mm, "end": v(57.14, 97.86) * mm});
            skLineSegment(sketch, "E994", {"start": v(57.14, 97.86) * mm, "end": v(57.67, 98.23) * mm});
            skLineSegment(sketch, "E995", {"start": v(57.67, 98.23) * mm, "end": v(59, 97.33) * mm});
            skLineSegment(sketch, "E996", {"start": v(59, 97.33) * mm, "end": v(58.85, 96.7) * mm});
            skLineSegment(sketch, "E997", {"start": v(58.85, 96.7) * mm, "end": v(58.52, 95.47) * mm});
            skLineSegment(sketch, "E998", {"start": v(58.52, 95.47) * mm, "end": v(58.35, 94.86) * mm});
            skLineSegment(sketch, "E999", {"start": v(58.35, 94.86) * mm, "end": v(59.69, 93.9) * mm});
            skLineSegment(sketch, "E1000", {"start": v(59.69, 93.9) * mm, "end": v(60.2, 94.27) * mm});
            skLineSegment(sketch, "E1001", {"start": v(60.2, 94.27) * mm, "end": v(61.26, 94.99) * mm});
            skLineSegment(sketch, "E1002", {"start": v(61.26, 94.99) * mm, "end": v(61.8, 95.33) * mm});
            skLineSegment(sketch, "E1003", {"start": v(61.8, 95.33) * mm, "end": v(63.1, 94.37) * mm});
            skLineSegment(sketch, "E1004", {"start": v(63.1, 94.37) * mm, "end": v(62.92, 93.76) * mm});
            skLineSegment(sketch, "E1005", {"start": v(62.92, 93.76) * mm, "end": v(62.54, 92.54) * mm});
            skLineSegment(sketch, "E1006", {"start": v(62.54, 92.54) * mm, "end": v(62.34, 91.94) * mm});
            skLineSegment(sketch, "E1007", {"start": v(62.34, 91.94) * mm, "end": v(63.64, 90.93) * mm});
            skLineSegment(sketch, "E1008", {"start": v(63.64, 90.93) * mm, "end": v(64.17, 91.27) * mm});
            skLineSegment(sketch, "E1009", {"start": v(64.17, 91.27) * mm, "end": v(65.26, 91.94) * mm});
            skLineSegment(sketch, "E1010", {"start": v(65.26, 91.94) * mm, "end": v(65.81, 92.26) * mm});
            skLineSegment(sketch, "E1011", {"start": v(65.81, 92.26) * mm, "end": v(67.06, 91.25) * mm});
            skLineSegment(sketch, "E1012", {"start": v(67.06, 91.25) * mm, "end": v(66.86, 90.64) * mm});
            skLineSegment(sketch, "E1013", {"start": v(66.86, 90.64) * mm, "end": v(66.43, 89.44) * mm});
            skLineSegment(sketch, "E1014", {"start": v(66.43, 89.44) * mm, "end": v(66.2, 88.85) * mm});
            skLineSegment(sketch, "E1015", {"start": v(66.2, 88.85) * mm, "end": v(67.46, 87.78) * mm});
            skLineSegment(sketch, "E1016", {"start": v(67.46, 87.78) * mm, "end": v(68, 88.1) * mm});
            skLineSegment(sketch, "E1017", {"start": v(68, 88.1) * mm, "end": v(69.12, 88.72) * mm});
            skLineSegment(sketch, "E1018", {"start": v(69.12, 88.72) * mm, "end": v(69.69, 89.02) * mm});
            skLineSegment(sketch, "E1019", {"start": v(69.69, 89.02) * mm, "end": v(70.9, 87.96) * mm});
            skLineSegment(sketch, "E1020", {"start": v(70.9, 87.96) * mm, "end": v(70.67, 87.36) * mm});
            skLineSegment(sketch, "E1021", {"start": v(70.67, 87.36) * mm, "end": v(70.19, 86.17) * mm});
            skLineSegment(sketch, "E1022", {"start": v(70.19, 86.17) * mm, "end": v(69.93, 85.6) * mm});
            skLineSegment(sketch, "E1023", {"start": v(69.93, 85.6) * mm, "end": v(71.14, 84.48) * mm});
            skLineSegment(sketch, "E1024", {"start": v(71.14, 84.48) * mm, "end": v(71.7, 84.77) * mm});
            skLineSegment(sketch, "E1025", {"start": v(71.7, 84.77) * mm, "end": v(72.84, 85.35) * mm});
            skLineSegment(sketch, "E1026", {"start": v(72.84, 85.35) * mm, "end": v(73.42, 85.62) * mm});
            skLineSegment(sketch, "E1027", {"start": v(73.42, 85.62) * mm, "end": v(74.58, 84.5) * mm});
            skLineSegment(sketch, "E1028", {"start": v(74.58, 84.5) * mm, "end": v(74.33, 83.91) * mm});
            skLineSegment(sketch, "E1029", {"start": v(74.33, 83.91) * mm, "end": v(73.8, 82.75) * mm});
            skLineSegment(sketch, "E1030", {"start": v(73.8, 82.75) * mm, "end": v(73.52, 82.18) * mm});
            skLineSegment(sketch, "E1031", {"start": v(73.52, 82.18) * mm, "end": v(74.68, 81.02) * mm});
            skLineSegment(sketch, "E1032", {"start": v(74.68, 81.02) * mm, "end": v(75.25, 81.29) * mm});
            skLineSegment(sketch, "E1033", {"start": v(75.25, 81.29) * mm, "end": v(76.41, 81.81) * mm});
            skLineSegment(sketch, "E1034", {"start": v(76.41, 81.81) * mm, "end": v(77, 82.06) * mm});
            skLineSegment(sketch, "E1035", {"start": v(77, 82.06) * mm, "end": v(78.12, 80.9) * mm});
            skLineSegment(sketch, "E1036", {"start": v(78.12, 80.9) * mm, "end": v(77.84, 80.32) * mm});
            skLineSegment(sketch, "E1037", {"start": v(77.84, 80.32) * mm, "end": v(77.26, 79.18) * mm});
            skLineSegment(sketch, "E1038", {"start": v(77.26, 79.18) * mm, "end": v(76.96, 78.62) * mm});
            skLineSegment(sketch, "E1039", {"start": v(76.96, 78.62) * mm, "end": v(78.06, 77.4) * mm});
            skLineSegment(sketch, "E1040", {"start": v(78.06, 77.4) * mm, "end": v(78.65, 77.66) * mm});
            skLineSegment(sketch, "E1041", {"start": v(78.65, 77.66) * mm, "end": v(79.83, 78.13) * mm});
            skLineSegment(sketch, "E1042", {"start": v(79.83, 78.13) * mm, "end": v(80.44, 78.35) * mm});
            skLineSegment(sketch, "E1043", {"start": v(80.44, 78.35) * mm, "end": v(81.5, 77.14) * mm});
            skLineSegment(sketch, "E1044", {"start": v(81.5, 77.14) * mm, "end": v(81.2, 76.57) * mm});
            skLineSegment(sketch, "E1045", {"start": v(81.2, 76.57) * mm, "end": v(80.56, 75.46) * mm});
            skLineSegment(sketch, "E1046", {"start": v(80.56, 75.46) * mm, "end": v(80.24, 74.92) * mm});
            skLineSegment(sketch, "E1047", {"start": v(80.24, 74.92) * mm, "end": v(81.3, 73.66) * mm});
            skLineSegment(sketch, "E1048", {"start": v(81.3, 73.66) * mm, "end": v(81.89, 73.88) * mm});
            skLineSegment(sketch, "E1049", {"start": v(81.89, 73.88) * mm, "end": v(83.1, 74.3) * mm});
            skLineSegment(sketch, "E1050", {"start": v(83.1, 74.3) * mm, "end": v(83.7, 74.5) * mm});
            skLineSegment(sketch, "E1051", {"start": v(83.7, 74.5) * mm, "end": v(84.7, 73.25) * mm});
            skLineSegment(sketch, "E1052", {"start": v(84.7, 73.25) * mm, "end": v(84.38, 72.7) * mm});
            skLineSegment(sketch, "E1053", {"start": v(84.38, 72.7) * mm, "end": v(83.7, 71.6) * mm});
            skLineSegment(sketch, "E1054", {"start": v(83.7, 71.6) * mm, "end": v(83.36, 71.08) * mm});
            skLineSegment(sketch, "E1055", {"start": v(83.36, 71.08) * mm, "end": v(84.36, 69.77) * mm});
            skLineSegment(sketch, "E1056", {"start": v(84.36, 69.77) * mm, "end": v(84.96, 69.97) * mm});
            skLineSegment(sketch, "E1057", {"start": v(84.96, 69.97) * mm, "end": v(86.18, 70.34) * mm});
            skLineSegment(sketch, "E1058", {"start": v(86.18, 70.34) * mm, "end": v(86.8, 70.52) * mm});
            skLineSegment(sketch, "E1059", {"start": v(86.8, 70.52) * mm, "end": v(87.75, 69.22) * mm});
            skLineSegment(sketch, "E1060", {"start": v(87.75, 69.22) * mm, "end": v(87.4, 68.68) * mm});
            skLineSegment(sketch, "E1061", {"start": v(87.4, 68.68) * mm, "end": v(86.68, 67.62) * mm});
            skLineSegment(sketch, "E1062", {"start": v(86.68, 67.62) * mm, "end": v(86.31, 67.11) * mm});
            skLineSegment(sketch, "E1063", {"start": v(86.31, 67.11) * mm, "end": v(87.26, 65.76) * mm});
            skLineSegment(sketch, "E1064", {"start": v(87.26, 65.76) * mm, "end": v(87.87, 65.94) * mm});
            skLineSegment(sketch, "E1065", {"start": v(87.87, 65.94) * mm, "end": v(89.1, 66.25) * mm});
            skLineSegment(sketch, "E1066", {"start": v(89.1, 66.25) * mm, "end": v(89.73, 66.4) * mm});
            skLineSegment(sketch, "E1067", {"start": v(89.73, 66.4) * mm, "end": v(90.62, 65.06) * mm});
            skLineSegment(sketch, "E1068", {"start": v(90.62, 65.06) * mm, "end": v(90.25, 64.54) * mm});
            skLineSegment(sketch, "E1069", {"start": v(90.25, 64.54) * mm, "end": v(89.49, 63.51) * mm});
            skLineSegment(sketch, "E1070", {"start": v(89.49, 63.51) * mm, "end": v(89.1, 63.02) * mm});
            skLineSegment(sketch, "E1071", {"start": v(89.1, 63.02) * mm, "end": v(89.98, 61.63) * mm});
            skLineSegment(sketch, "E1072", {"start": v(89.98, 61.63) * mm, "end": v(90.6, 61.78) * mm});
            skLineSegment(sketch, "E1073", {"start": v(90.6, 61.78) * mm, "end": v(91.84, 62.04) * mm});
            skLineSegment(sketch, "E1074", {"start": v(91.84, 62.04) * mm, "end": v(92.48, 62.16) * mm});
            skLineSegment(sketch, "E1075", {"start": v(92.48, 62.16) * mm, "end": v(93.31, 60.79) * mm});
            skLineSegment(sketch, "E1076", {"start": v(93.31, 60.79) * mm, "end": v(92.92, 60.28) * mm});
            skLineSegment(sketch, "E1077", {"start": v(92.92, 60.28) * mm, "end": v(92.11, 59.3) * mm});
            skLineSegment(sketch, "E1078", {"start": v(92.11, 59.3) * mm, "end": v(91.7, 58.8) * mm});
            skLineSegment(sketch, "E1079", {"start": v(91.7, 58.8) * mm, "end": v(92.52, 57.39) * mm});
            skLineSegment(sketch, "E1080", {"start": v(92.52, 57.39) * mm, "end": v(93.15, 57.5) * mm});
            skLineSegment(sketch, "E1081", {"start": v(93.15, 57.5) * mm, "end": v(94.4, 57.72) * mm});
            skLineSegment(sketch, "E1082", {"start": v(94.4, 57.72) * mm, "end": v(95.04, 57.8) * mm});
            skLineSegment(sketch, "E1083", {"start": v(95.04, 57.8) * mm, "end": v(95.82, 56.4) * mm});
            skLineSegment(sketch, "E1084", {"start": v(95.82, 56.4) * mm, "end": v(95.4, 55.9) * mm});
            skLineSegment(sketch, "E1085", {"start": v(95.4, 55.9) * mm, "end": v(94.55, 54.96) * mm});
            skLineSegment(sketch, "E1086", {"start": v(94.55, 54.96) * mm, "end": v(94.12, 54.5) * mm});
            skLineSegment(sketch, "E1087", {"start": v(94.12, 54.5) * mm, "end": v(94.88, 53.04) * mm});
            skLineSegment(sketch, "E1088", {"start": v(94.88, 53.04) * mm, "end": v(95.51, 53.13) * mm});
            skLineSegment(sketch, "E1089", {"start": v(95.51, 53.13) * mm, "end": v(96.78, 53.29) * mm});
            skLineSegment(sketch, "E1090", {"start": v(96.78, 53.29) * mm, "end": v(97.42, 53.35) * mm});
            skLineSegment(sketch, "E1091", {"start": v(97.42, 53.35) * mm, "end": v(98.14, 51.91) * mm});
            skLineSegment(sketch, "E1092", {"start": v(98.14, 51.91) * mm, "end": v(97.7, 51.44) * mm});
            skLineSegment(sketch, "E1093", {"start": v(97.7, 51.44) * mm, "end": v(96.8, 50.52) * mm});
            skLineSegment(sketch, "E1094", {"start": v(96.8, 50.52) * mm, "end": v(96.36, 50.08) * mm});
            skLineSegment(sketch, "E1095", {"start": v(96.36, 50.08) * mm, "end": v(97.06, 48.6) * mm});
            skLineSegment(sketch, "E1096", {"start": v(97.06, 48.6) * mm, "end": v(97.69, 48.66) * mm});
            skLineSegment(sketch, "E1097", {"start": v(97.69, 48.66) * mm, "end": v(98.96, 48.76) * mm});
            skLineSegment(sketch, "E1098", {"start": v(98.96, 48.76) * mm, "end": v(99.6, 48.8) * mm});
            skLineSegment(sketch, "E1099", {"start": v(99.6, 48.8) * mm, "end": v(100.26, 47.33) * mm});
            skLineSegment(sketch, "E1100", {"start": v(100.26, 47.33) * mm, "end": v(99.8, 46.87) * mm});
            skLineSegment(sketch, "E1101", {"start": v(99.8, 46.87) * mm, "end": v(98.87, 46) * mm});
            skLineSegment(sketch, "E1102", {"start": v(98.87, 46) * mm, "end": v(98.4, 45.57) * mm});
            skLineSegment(sketch, "E1103", {"start": v(98.4, 45.57) * mm, "end": v(99.04, 44.06) * mm});
            skLineSegment(sketch, "E1104", {"start": v(99.04, 44.06) * mm, "end": v(99.67, 44.1) * mm});
            skLineSegment(sketch, "E1105", {"start": v(99.67, 44.1) * mm, "end": v(100.95, 44.15) * mm});
            skLineSegment(sketch, "E1106", {"start": v(100.95, 44.15) * mm, "end": v(101.59, 44.15) * mm});
            skLineSegment(sketch, "E1107", {"start": v(101.59, 44.15) * mm, "end": v(102.18, 42.66) * mm});
            skLineSegment(sketch, "E1108", {"start": v(102.18, 42.66) * mm, "end": v(101.7, 42.22) * mm});
            skLineSegment(sketch, "E1109", {"start": v(101.7, 42.22) * mm, "end": v(100.74, 41.39) * mm});
            skLineSegment(sketch, "E1110", {"start": v(100.74, 41.39) * mm, "end": v(100.25, 40.98) * mm});
            skLineSegment(sketch, "E1111", {"start": v(100.25, 40.98) * mm, "end": v(100.82, 39.44) * mm});
            skLineSegment(sketch, "E1112", {"start": v(100.82, 39.44) * mm, "end": v(101.46, 39.45) * mm});
            skLineSegment(sketch, "E1113", {"start": v(101.46, 39.45) * mm, "end": v(102.73, 39.45) * mm});
            skLineSegment(sketch, "E1114", {"start": v(102.73, 39.45) * mm, "end": v(103.38, 39.43) * mm});
            skLineSegment(sketch, "E1115", {"start": v(103.38, 39.43) * mm, "end": v(103.9, 37.9) * mm});
            skLineSegment(sketch, "E1116", {"start": v(103.9, 37.9) * mm, "end": v(103.4, 37.5) * mm});
            skLineSegment(sketch, "E1117", {"start": v(103.4, 37.5) * mm, "end": v(102.4, 36.7) * mm});
            skLineSegment(sketch, "E1118", {"start": v(102.4, 36.7) * mm, "end": v(101.9, 36.32) * mm});
            skLineSegment(sketch, "E1119", {"start": v(101.9, 36.32) * mm, "end": v(102.4, 34.75) * mm});
            skLineSegment(sketch, "E1120", {"start": v(102.4, 34.75) * mm, "end": v(103.04, 34.74) * mm});
            skLineSegment(sketch, "E1121", {"start": v(103.04, 34.74) * mm, "end": v(104.32, 34.68) * mm});
            skLineSegment(sketch, "E1122", {"start": v(104.32, 34.68) * mm, "end": v(104.96, 34.63) * mm});
            skLineSegment(sketch, "E1123", {"start": v(104.96, 34.63) * mm, "end": v(105.42, 33.1) * mm});
            skLineSegment(sketch, "E1124", {"start": v(105.42, 33.1) * mm, "end": v(104.9, 32.7) * mm});
            skLineSegment(sketch, "E1125", {"start": v(104.9, 32.7) * mm, "end": v(103.88, 31.95) * mm});
            skLineSegment(sketch, "E1126", {"start": v(103.88, 31.95) * mm, "end": v(103.36, 31.59) * mm});
            skLineSegment(sketch, "E1127", {"start": v(103.36, 31.59) * mm, "end": v(103.8, 30) * mm});
            skLineSegment(sketch, "E1128", {"start": v(103.8, 30) * mm, "end": v(104.43, 29.96) * mm});
            skLineSegment(sketch, "E1129", {"start": v(104.43, 29.96) * mm, "end": v(105.7, 29.85) * mm});
            skLineSegment(sketch, "E1130", {"start": v(105.7, 29.85) * mm, "end": v(106.34, 29.77) * mm});
            skLineSegment(sketch, "E1131", {"start": v(106.34, 29.77) * mm, "end": v(106.73, 28.21) * mm});
            skLineSegment(sketch, "E1132", {"start": v(106.73, 28.21) * mm, "end": v(106.2, 27.84) * mm});
            skLineSegment(sketch, "E1133", {"start": v(106.2, 27.84) * mm, "end": v(105.14, 27.14) * mm});
            skLineSegment(sketch, "E1134", {"start": v(105.14, 27.14) * mm, "end": v(104.6, 26.8) * mm});
            skLineSegment(sketch, "E1135", {"start": v(104.6, 26.8) * mm, "end": v(104.97, 25.2) * mm});
            skLineSegment(sketch, "E1136", {"start": v(104.97, 25.2) * mm, "end": v(105.6, 25.13) * mm});
            skLineSegment(sketch, "E1137", {"start": v(105.6, 25.13) * mm, "end": v(106.87, 24.96) * mm});
            skLineSegment(sketch, "E1138", {"start": v(106.87, 24.96) * mm, "end": v(107.5, 24.86) * mm});
            skLineSegment(sketch, "E1139", {"start": v(107.5, 24.86) * mm, "end": v(107.83, 23.28) * mm});
            skLineSegment(sketch, "E1140", {"start": v(107.83, 23.28) * mm, "end": v(107.29, 22.94) * mm});
            skLineSegment(sketch, "E1141", {"start": v(107.29, 22.94) * mm, "end": v(106.2, 22.28) * mm});
            skLineSegment(sketch, "E1142", {"start": v(106.2, 22.28) * mm, "end": v(105.65, 21.96) * mm});
            skLineSegment(sketch, "E1143", {"start": v(105.65, 21.96) * mm, "end": v(105.95, 20.35) * mm});
            skLineSegment(sketch, "E1144", {"start": v(105.95, 20.35) * mm, "end": v(106.57, 20.25) * mm});
            skLineSegment(sketch, "E1145", {"start": v(106.57, 20.25) * mm, "end": v(107.83, 20.03) * mm});
            skLineSegment(sketch, "E1146", {"start": v(107.83, 20.03) * mm, "end": v(108.46, 19.9) * mm});
            skLineSegment(sketch, "E1147", {"start": v(108.46, 19.9) * mm, "end": v(108.72, 18.31) * mm});
            skLineSegment(sketch, "E1148", {"start": v(108.72, 18.31) * mm, "end": v(108.16, 17.99) * mm});
            skLineSegment(sketch, "E1149", {"start": v(108.16, 17.99) * mm, "end": v(107.04, 17.38) * mm});
            skLineSegment(sketch, "E1150", {"start": v(107.04, 17.38) * mm, "end": v(106.48, 17.09) * mm});
            skLineSegment(sketch, "E1151", {"start": v(106.48, 17.09) * mm, "end": v(106.71, 15.46) * mm});
            skLineSegment(sketch, "E1152", {"start": v(106.71, 15.46) * mm, "end": v(107.33, 15.34) * mm});
            skLineSegment(sketch, "E1153", {"start": v(107.33, 15.34) * mm, "end": v(108.58, 15.06) * mm});
            skLineSegment(sketch, "E1154", {"start": v(108.58, 15.06) * mm, "end": v(109.2, 14.9) * mm});
            skLineSegment(sketch, "E1155", {"start": v(109.2, 14.9) * mm, "end": v(109.4, 13.3) * mm});
            skLineSegment(sketch, "E1156", {"start": v(109.4, 13.3) * mm, "end": v(108.83, 13) * mm});
            skLineSegment(sketch, "E1157", {"start": v(108.83, 13) * mm, "end": v(107.68, 12.44) * mm});
            skLineSegment(sketch, "E1158", {"start": v(107.68, 12.44) * mm, "end": v(107.1, 12.18) * mm});
            skLineSegment(sketch, "E1159", {"start": v(107.1, 12.18) * mm, "end": v(107.27, 10.54) * mm});
            skLineSegment(sketch, "E1160", {"start": v(107.27, 10.54) * mm, "end": v(107.88, 10.4) * mm});
            skLineSegment(sketch, "E1161", {"start": v(107.88, 10.4) * mm, "end": v(109.12, 10.06) * mm});
            skLineSegment(sketch, "E1162", {"start": v(109.12, 10.06) * mm, "end": v(109.73, 9.88) * mm});
            skLineSegment(sketch, "E1163", {"start": v(109.73, 9.88) * mm, "end": v(109.86, 8.28) * mm});
            skLineSegment(sketch, "E1164", {"start": v(109.86, 8.28) * mm, "end": v(109.28, 8) * mm});
            skLineSegment(sketch, "E1165", {"start": v(109.28, 8) * mm, "end": v(108.1, 7.49) * mm});
            skLineSegment(sketch, "E1166", {"start": v(108.1, 7.49) * mm, "end": v(107.52, 7.25) * mm});
            skLineSegment(sketch, "E1167", {"start": v(107.52, 7.25) * mm, "end": v(107.61, 5.6) * mm});
            skLineSegment(sketch, "E1168", {"start": v(107.61, 5.6) * mm, "end": v(108.22, 5.43) * mm});
            skLineSegment(sketch, "E1169", {"start": v(108.22, 5.43) * mm, "end": v(109.44, 5.05) * mm});
            skLineSegment(sketch, "E1170", {"start": v(109.44, 5.05) * mm, "end": v(110.05, 4.84) * mm});
            skLineSegment(sketch, "E1171", {"start": v(110.05, 4.84) * mm, "end": v(110.1, 3.23) * mm});
            skLineSegment(sketch, "E1172", {"start": v(110.1, 3.23) * mm, "end": v(109.51, 2.98) * mm});
            skLineSegment(sketch, "E1173", {"start": v(109.51, 2.98) * mm, "end": v(108.32, 2.52) * mm});
            skLineSegment(sketch, "E1174", {"start": v(108.32, 2.52) * mm, "end": v(107.73, 2.3) * mm});
            skLineSegment(sketch, "E1175", {"start": v(107.73, 2.3) * mm, "end": v(107.75, 0.66) * mm});
            skLineSegment(sketch, "E1176", {"start": v(17.62, 6.87) * mm, "end": v(93.39, 6.22) * mm});
            skLineSegment(sketch, "E1177", {"start": v(93.39, 6.22) * mm, "end": v(96.66, 9.74) * mm});
            skLineSegment(sketch, "E1178", {"start": v(96.66, 9.74) * mm, "end": v(95.72, 17.08) * mm});
            skLineSegment(sketch, "E1179", {"start": v(95.72, 17.08) * mm, "end": v(94.26, 24.33) * mm});
            skLineSegment(sketch, "E1180", {"start": v(94.26, 24.33) * mm, "end": v(92.3, 31.46) * mm});
            skLineSegment(sketch, "E1181", {"start": v(92.3, 31.46) * mm, "end": v(89.83, 38.44) * mm});
            skLineSegment(sketch, "E1182", {"start": v(89.83, 38.44) * mm, "end": v(86.89, 45.22) * mm});
            skLineSegment(sketch, "E1183", {"start": v(86.89, 45.22) * mm, "end": v(83.47, 51.79) * mm});
            skLineSegment(sketch, "E1184", {"start": v(83.47, 51.79) * mm, "end": v(79.6, 58.1) * mm});
            skLineSegment(sketch, "E1185", {"start": v(79.6, 58.1) * mm, "end": v(75.3, 64.11) * mm});
            skLineSegment(sketch, "E1186", {"start": v(75.3, 64.11) * mm, "end": v(70.59, 69.81) * mm});
            skLineSegment(sketch, "E1187", {"start": v(70.59, 69.81) * mm, "end": v(65.48, 75.17) * mm});
            skLineSegment(sketch, "E1188", {"start": v(65.48, 75.17) * mm, "end": v(60.01, 80.15) * mm});
            skLineSegment(sketch, "E1189", {"start": v(60.01, 80.15) * mm, "end": v(54.2, 84.74) * mm});
            skLineSegment(sketch, "E1190", {"start": v(54.2, 84.74) * mm, "end": v(49.5, 83.74) * mm});
            skLineSegment(sketch, "E1191", {"start": v(49.5, 83.74) * mm, "end": v(11.06, 18.45) * mm});
            skLineSegment(sketch, "E1192", {"start": v(11.06, 18.45) * mm, "end": v(11.57, 12.32) * mm});
            skLineSegment(sketch, "E1193", {"start": v(11.57, 12.32) * mm, "end": v(17.62, 6.87) * mm});
            skLineSegment(sketch, "E1194", {"start": v(-1.16, 25.64) * mm, "end": v(37.29, 90.94) * mm});
            skLineSegment(sketch, "E1195", {"start": v(37.29, 90.94) * mm, "end": v(35.88, 95.53) * mm});
            skLineSegment(sketch, "E1196", {"start": v(35.88, 95.53) * mm, "end": v(29.05, 98.38) * mm});
            skLineSegment(sketch, "E1197", {"start": v(29.05, 98.38) * mm, "end": v(22.04, 100.75) * mm});
            skLineSegment(sketch, "E1198", {"start": v(22.04, 100.75) * mm, "end": v(14.88, 102.61) * mm});
            skLineSegment(sketch, "E1199", {"start": v(14.88, 102.61) * mm, "end": v(7.61, 103.97) * mm});
            skLineSegment(sketch, "E1200", {"start": v(7.61, 103.97) * mm, "end": v(0.26, 104.81) * mm});
            skLineSegment(sketch, "E1201", {"start": v(0.26, 104.81) * mm, "end": v(-7.13, 105.14) * mm});
            skLineSegment(sketch, "E1202", {"start": v(-7.13, 105.14) * mm, "end": v(-14.53, 104.94) * mm});
            skLineSegment(sketch, "E1203", {"start": v(-14.53, 104.94) * mm, "end": v(-21.9, 104.22) * mm});
            skLineSegment(sketch, "E1204", {"start": v(-21.9, 104.22) * mm, "end": v(-29.18, 102.99) * mm});
            skLineSegment(sketch, "E1205", {"start": v(-29.18, 102.99) * mm, "end": v(-36.38, 101.25) * mm});
            skLineSegment(sketch, "E1206", {"start": v(-36.38, 101.25) * mm, "end": v(-43.42, 99) * mm});
            skLineSegment(sketch, "E1207", {"start": v(-43.42, 99) * mm, "end": v(-50.3, 96.27) * mm});
            skLineSegment(sketch, "E1208", {"start": v(-50.3, 96.27) * mm, "end": v(-51.79, 91.7) * mm});
            skLineSegment(sketch, "E1209", {"start": v(-51.79, 91.7) * mm, "end": v(-14.46, 25.76) * mm});
            skLineSegment(sketch, "E1210", {"start": v(-14.46, 25.76) * mm, "end": v(-8.9, 23.14) * mm});
            skLineSegment(sketch, "E1211", {"start": v(-8.9, 23.14) * mm, "end": v(-1.16, 25.64) * mm});
            skLineSegment(sketch, "E1212", {"start": v(-26.8, 18.77) * mm, "end": v(-64.13, 84.71) * mm});
            skLineSegment(sketch, "E1213", {"start": v(-64.13, 84.71) * mm, "end": v(-68.81, 85.8) * mm});
            skLineSegment(sketch, "E1214", {"start": v(-68.81, 85.8) * mm, "end": v(-74.7, 81.3) * mm});
            skLineSegment(sketch, "E1215", {"start": v(-74.7, 81.3) * mm, "end": v(-80.25, 76.41) * mm});
            skLineSegment(sketch, "E1216", {"start": v(-80.25, 76.41) * mm, "end": v(-85.44, 71.15) * mm});
            skLineSegment(sketch, "E1217", {"start": v(-85.44, 71.15) * mm, "end": v(-90.25, 65.53) * mm});
            skLineSegment(sketch, "E1218", {"start": v(-90.25, 65.53) * mm, "end": v(-94.66, 59.58) * mm});
            skLineSegment(sketch, "E1219", {"start": v(-94.66, 59.58) * mm, "end": v(-98.63, 53.34) * mm});
            skLineSegment(sketch, "E1220", {"start": v(-98.63, 53.34) * mm, "end": v(-102.16, 46.84) * mm});
            skLineSegment(sketch, "E1221", {"start": v(-102.16, 46.84) * mm, "end": v(-105.22, 40.1) * mm});
            skLineSegment(sketch, "E1222", {"start": v(-105.22, 40.1) * mm, "end": v(-107.8, 33.17) * mm});
            skLineSegment(sketch, "E1223", {"start": v(-107.8, 33.17) * mm, "end": v(-109.89, 26.07) * mm});
            skLineSegment(sketch, "E1224", {"start": v(-109.89, 26.07) * mm, "end": v(-111.47, 18.85) * mm});
            skLineSegment(sketch, "E1225", {"start": v(-111.47, 18.85) * mm, "end": v(-112.54, 11.53) * mm});
            skLineSegment(sketch, "E1226", {"start": v(-112.54, 11.53) * mm, "end": v(-109.32, 7.95) * mm});
            skLineSegment(sketch, "E1227", {"start": v(-109.32, 7.95) * mm, "end": v(-33.56, 7.3) * mm});
            skLineSegment(sketch, "E1228", {"start": v(-33.56, 7.3) * mm, "end": v(-28.5, 10.8) * mm});
            skLineSegment(sketch, "E1229", {"start": v(-28.5, 10.8) * mm, "end": v(-26.8, 18.77) * mm});
            skLineSegment(sketch, "E1230", {"start": v(-33.68, -6.88) * mm, "end": v(-109.45, -6.23) * mm});
            skLineSegment(sketch, "E1231", {"start": v(-109.45, -6.23) * mm, "end": v(-112.72, -9.75) * mm});
            skLineSegment(sketch, "E1232", {"start": v(-112.72, -9.75) * mm, "end": v(-111.78, -17.08) * mm});
            skLineSegment(sketch, "E1233", {"start": v(-111.78, -17.08) * mm, "end": v(-110.32, -24.34) * mm});
            skLineSegment(sketch, "E1234", {"start": v(-110.32, -24.34) * mm, "end": v(-108.35, -31.47) * mm});
            skLineSegment(sketch, "E1235", {"start": v(-108.35, -31.47) * mm, "end": v(-105.9, -38.45) * mm});
            skLineSegment(sketch, "E1236", {"start": v(-105.9, -38.45) * mm, "end": v(-102.95, -45.23) * mm});
            skLineSegment(sketch, "E1237", {"start": v(-102.95, -45.23) * mm, "end": v(-99.53, -51.8) * mm});
            skLineSegment(sketch, "E1238", {"start": v(-99.53, -51.8) * mm, "end": v(-95.66, -58.1) * mm});
            skLineSegment(sketch, "E1239", {"start": v(-95.66, -58.1) * mm, "end": v(-91.36, -64.12) * mm});
            skLineSegment(sketch, "E1240", {"start": v(-91.36, -64.12) * mm, "end": v(-86.65, -69.82) * mm});
            skLineSegment(sketch, "E1241", {"start": v(-86.65, -69.82) * mm, "end": v(-81.54, -75.18) * mm});
            skLineSegment(sketch, "E1242", {"start": v(-81.54, -75.18) * mm, "end": v(-76.07, -80.16) * mm});
            skLineSegment(sketch, "E1243", {"start": v(-76.07, -80.16) * mm, "end": v(-70.27, -84.75) * mm});
            skLineSegment(sketch, "E1244", {"start": v(-70.27, -84.75) * mm, "end": v(-65.57, -83.75) * mm});
            skLineSegment(sketch, "E1245", {"start": v(-65.57, -83.75) * mm, "end": v(-27.12, -18.46) * mm});
            skLineSegment(sketch, "E1246", {"start": v(-27.12, -18.46) * mm, "end": v(-27.63, -12.33) * mm});
            skLineSegment(sketch, "E1247", {"start": v(-27.63, -12.33) * mm, "end": v(-33.68, -6.88) * mm});
            skLineSegment(sketch, "E1248", {"start": v(-14.9, -25.65) * mm, "end": v(-53.35, -90.94) * mm});
            skLineSegment(sketch, "E1249", {"start": v(-53.35, -90.94) * mm, "end": v(-51.94, -95.54) * mm});
            skLineSegment(sketch, "E1250", {"start": v(-51.94, -95.54) * mm, "end": v(-45.11, -98.4) * mm});
            skLineSegment(sketch, "E1251", {"start": v(-45.11, -98.4) * mm, "end": v(-38.1, -100.76) * mm});
            skLineSegment(sketch, "E1252", {"start": v(-38.1, -100.76) * mm, "end": v(-30.94, -102.62) * mm});
            skLineSegment(sketch, "E1253", {"start": v(-30.94, -102.62) * mm, "end": v(-23.67, -103.98) * mm});
            skLineSegment(sketch, "E1254", {"start": v(-23.67, -103.98) * mm, "end": v(-16.32, -104.82) * mm});
            skLineSegment(sketch, "E1255", {"start": v(-16.32, -104.82) * mm, "end": v(-8.93, -105.14) * mm});
            skLineSegment(sketch, "E1256", {"start": v(-8.93, -105.14) * mm, "end": v(-1.53, -104.95) * mm});
            skLineSegment(sketch, "E1257", {"start": v(-1.53, -104.95) * mm, "end": v(5.83, -104.23) * mm});
            skLineSegment(sketch, "E1258", {"start": v(5.83, -104.23) * mm, "end": v(13.13, -103) * mm});
            skLineSegment(sketch, "E1259", {"start": v(13.13, -103) * mm, "end": v(20.32, -101.25) * mm});
            skLineSegment(sketch, "E1260", {"start": v(20.32, -101.25) * mm, "end": v(27.37, -99.01) * mm});
            skLineSegment(sketch, "E1261", {"start": v(27.37, -99.01) * mm, "end": v(34.24, -96.28) * mm});
            skLineSegment(sketch, "E1262", {"start": v(34.24, -96.28) * mm, "end": v(35.73, -91.7) * mm});
            skLineSegment(sketch, "E1263", {"start": v(35.73, -91.7) * mm, "end": v(-1.6, -25.77) * mm});
            skLineSegment(sketch, "E1264", {"start": v(-1.6, -25.77) * mm, "end": v(-7.15, -23.14) * mm});
            skLineSegment(sketch, "E1265", {"start": v(-7.15, -23.14) * mm, "end": v(-14.9, -25.65) * mm});
            skLineSegment(sketch, "E1266", {"start": v(10.75, -18.78) * mm, "end": v(48.07, -84.72) * mm});
            skLineSegment(sketch, "E1267", {"start": v(48.07, -84.72) * mm, "end": v(52.75, -85.8) * mm});
            skLineSegment(sketch, "E1268", {"start": v(52.75, -85.8) * mm, "end": v(58.63, -81.31) * mm});
            skLineSegment(sketch, "E1269", {"start": v(58.63, -81.31) * mm, "end": v(64.19, -76.42) * mm});
            skLineSegment(sketch, "E1270", {"start": v(64.19, -76.42) * mm, "end": v(69.38, -71.16) * mm});
            skLineSegment(sketch, "E1271", {"start": v(69.38, -71.16) * mm, "end": v(74.2, -65.54) * mm});
            skLineSegment(sketch, "E1272", {"start": v(74.2, -65.54) * mm, "end": v(78.6, -59.6) * mm});
            skLineSegment(sketch, "E1273", {"start": v(78.6, -59.6) * mm, "end": v(82.57, -53.35) * mm});
            skLineSegment(sketch, "E1274", {"start": v(82.57, -53.35) * mm, "end": v(86.1, -46.85) * mm});
            skLineSegment(sketch, "E1275", {"start": v(86.1, -46.85) * mm, "end": v(89.16, -40.11) * mm});
            skLineSegment(sketch, "E1276", {"start": v(89.16, -40.11) * mm, "end": v(91.74, -33.18) * mm});
            skLineSegment(sketch, "E1277", {"start": v(91.74, -33.18) * mm, "end": v(93.83, -26.08) * mm});
            skLineSegment(sketch, "E1278", {"start": v(93.83, -26.08) * mm, "end": v(95.4, -18.85) * mm});
            skLineSegment(sketch, "E1279", {"start": v(95.4, -18.85) * mm, "end": v(96.48, -11.53) * mm});
            skLineSegment(sketch, "E1280", {"start": v(96.48, -11.53) * mm, "end": v(93.26, -7.96) * mm});
            skLineSegment(sketch, "E1281", {"start": v(93.26, -7.96) * mm, "end": v(17.5, -7.31) * mm});
            skLineSegment(sketch, "E1282", {"start": v(17.5, -7.31) * mm, "end": v(12.45, -10.82) * mm});
            skLineSegment(sketch, "E1283", {"start": v(12.45, -10.82) * mm, "end": v(10.75, -18.78) * mm});
            skLineSegment(sketch, "E1284", {"start": v(-7.03, 0) * mm, "end": v(-7.06, 0.25) * mm});
            skLineSegment(sketch, "E1285", {"start": v(-7.06, 0.25) * mm, "end": v(-7.16, 0.5) * mm});
            skLineSegment(sketch, "E1286", {"start": v(-7.16, 0.5) * mm, "end": v(-7.32, 0.7) * mm});
            skLineSegment(sketch, "E1287", {"start": v(-7.32, 0.7) * mm, "end": v(-7.53, 0.86) * mm});
            skLineSegment(sketch, "E1288", {"start": v(-7.53, 0.86) * mm, "end": v(-7.77, 0.96) * mm});
            skLineSegment(sketch, "E1289", {"start": v(-7.77, 0.96) * mm, "end": v(-8.03, 1) * mm});
            skLineSegment(sketch, "E1290", {"start": v(-8.03, 1) * mm, "end": v(-8.29, 0.96) * mm});
            skLineSegment(sketch, "E1291", {"start": v(-8.29, 0.96) * mm, "end": v(-8.53, 0.86) * mm});
            skLineSegment(sketch, "E1292", {"start": v(-8.53, 0.86) * mm, "end": v(-8.74, 0.7) * mm});
            skLineSegment(sketch, "E1293", {"start": v(-8.74, 0.7) * mm, "end": v(-8.9, 0.5) * mm});
            skLineSegment(sketch, "E1294", {"start": v(-8.9, 0.5) * mm, "end": v(-9, 0.25) * mm});
            skLineSegment(sketch, "E1295", {"start": v(-9, 0.25) * mm, "end": v(-9.03, 0) * mm});
            skLineSegment(sketch, "E1296", {"start": v(-9.03, 0) * mm, "end": v(-9, -0.26) * mm});
            skLineSegment(sketch, "E1297", {"start": v(-9, -0.26) * mm, "end": v(-8.9, -0.5) * mm});
            skLineSegment(sketch, "E1298", {"start": v(-8.9, -0.5) * mm, "end": v(-8.74, -0.71) * mm});
            skLineSegment(sketch, "E1299", {"start": v(-8.74, -0.71) * mm, "end": v(-8.53, -0.87) * mm});
            skLineSegment(sketch, "E1300", {"start": v(-8.53, -0.87) * mm, "end": v(-8.29, -0.97) * mm});
            skLineSegment(sketch, "E1301", {"start": v(-8.29, -0.97) * mm, "end": v(-8.03, -1) * mm});
            skLineSegment(sketch, "E1302", {"start": v(-8.03, -1) * mm, "end": v(-7.77, -0.97) * mm});
            skLineSegment(sketch, "E1303", {"start": v(-7.77, -0.97) * mm, "end": v(-7.53, -0.87) * mm});
            skLineSegment(sketch, "E1304", {"start": v(-7.53, -0.87) * mm, "end": v(-7.32, -0.71) * mm});
            skLineSegment(sketch, "E1305", {"start": v(-7.32, -0.71) * mm, "end": v(-7.16, -0.5) * mm});
            skLineSegment(sketch, "E1306", {"start": v(-7.16, -0.5) * mm, "end": v(-7.06, -0.26) * mm});
            skLineSegment(sketch, "E1307", {"start": v(-7.06, -0.26) * mm, "end": v(-7.03, 0) * mm});
            skLineSegment(sketch, "E1308", {"start": v(113.55, -0.17) * mm, "end": v(113.47, 0) * mm});
            skLineSegment(sketch, "E1309", {"start": v(113.47, 0) * mm, "end": v(113.39, 0.06) * mm});
            skLineSegment(sketch, "E1310", {"start": v(113.39, 0.06) * mm, "end": v(113.23, 0.12) * mm});
            skLineSegment(sketch, "E1311", {"start": v(113.23, 0.12) * mm, "end": v(113.07, 0.15) * mm});
            skLineSegment(sketch, "E1312", {"start": v(113.07, 0.15) * mm, "end": v(112.75, 0.15) * mm});
            skLineSegment(sketch, "E1313", {"start": v(112.75, 0.15) * mm, "end": v(112.43, 0.22) * mm});
            skLineSegment(sketch, "E1314", {"start": v(112.43, 0.22) * mm, "end": v(112.12, 0.36) * mm});
            skLineSegment(sketch, "E1315", {"start": v(112.12, 0.36) * mm, "end": v(111.81, 0.55) * mm});
            skLineSegment(sketch, "E1316", {"start": v(111.81, 0.55) * mm, "end": v(111.51, 0.78) * mm});
            skLineSegment(sketch, "E1317", {"start": v(111.51, 0.78) * mm, "end": v(111.22, 1.05) * mm});
            skLineSegment(sketch, "E1318", {"start": v(111.22, 1.05) * mm, "end": v(111.36, 1.76) * mm});
            skLineSegment(sketch, "E1319", {"start": v(111.36, 1.76) * mm, "end": v(111.56, 2.46) * mm});
            skLineSegment(sketch, "E1320", {"start": v(111.56, 2.46) * mm, "end": v(111.94, 2.57) * mm});
            skLineSegment(sketch, "E1321", {"start": v(111.94, 2.57) * mm, "end": v(112.31, 2.64) * mm});
            skLineSegment(sketch, "E1322", {"start": v(112.31, 2.64) * mm, "end": v(112.67, 2.67) * mm});
            skLineSegment(sketch, "E1323", {"start": v(112.67, 2.67) * mm, "end": v(113.02, 2.65) * mm});
            skLineSegment(sketch, "E1324", {"start": v(113.02, 2.65) * mm, "end": v(113.33, 2.57) * mm});
            skLineSegment(sketch, "E1325", {"start": v(113.33, 2.57) * mm, "end": v(113.61, 2.42) * mm});
            skLineSegment(sketch, "E1326", {"start": v(113.61, 2.42) * mm, "end": v(113.77, 2.38) * mm});
            skLineSegment(sketch, "E1327", {"start": v(113.77, 2.38) * mm, "end": v(113.94, 2.36) * mm});
            skLineSegment(sketch, "E1328", {"start": v(113.94, 2.36) * mm, "end": v(114.04, 2.38) * mm});
            skLineSegment(sketch, "E1329", {"start": v(114.04, 2.38) * mm, "end": v(114.19, 2.49) * mm});
            skLineSegment(sketch, "E1330", {"start": v(114.19, 2.49) * mm, "end": v(114.53, 3.03) * mm});
            skLineSegment(sketch, "E1331", {"start": v(114.53, 3.03) * mm, "end": v(114.95, 3.53) * mm});
            skLineSegment(sketch, "E1332", {"start": v(114.95, 3.53) * mm, "end": v(115, 3.7) * mm});
            skLineSegment(sketch, "E1333", {"start": v(115, 3.7) * mm, "end": v(115, 3.8) * mm});
            skLineSegment(sketch, "E1334", {"start": v(115, 3.8) * mm, "end": v(114.92, 3.96) * mm});
            skLineSegment(sketch, "E1335", {"start": v(114.92, 3.96) * mm, "end": v(114.83, 4.1) * mm});
            skLineSegment(sketch, "E1336", {"start": v(114.83, 4.1) * mm, "end": v(114.6, 4.32) * mm});
            skLineSegment(sketch, "E1337", {"start": v(114.6, 4.32) * mm, "end": v(114.43, 4.6) * mm});
            skLineSegment(sketch, "E1338", {"start": v(114.43, 4.6) * mm, "end": v(114.3, 4.92) * mm});
            skLineSegment(sketch, "E1339", {"start": v(114.3, 4.92) * mm, "end": v(114.22, 5.27) * mm});
            skLineSegment(sketch, "E1340", {"start": v(114.22, 5.27) * mm, "end": v(114.17, 5.64) * mm});
            skLineSegment(sketch, "E1341", {"start": v(114.17, 5.64) * mm, "end": v(114.16, 6.04) * mm});
            skLineSegment(sketch, "E1342", {"start": v(114.16, 6.04) * mm, "end": v(114.76, 6.45) * mm});
            skLineSegment(sketch, "E1343", {"start": v(114.76, 6.45) * mm, "end": v(115.4, 6.8) * mm});
            skLineSegment(sketch, "E1344", {"start": v(115.4, 6.8) * mm, "end": v(115.74, 6.6) * mm});
            skLineSegment(sketch, "E1345", {"start": v(115.74, 6.6) * mm, "end": v(116.06, 6.4) * mm});
            skLineSegment(sketch, "E1346", {"start": v(116.06, 6.4) * mm, "end": v(116.33, 6.16) * mm});
            skLineSegment(sketch, "E1347", {"start": v(116.33, 6.16) * mm, "end": v(116.56, 5.9) * mm});
            skLineSegment(sketch, "E1348", {"start": v(116.56, 5.9) * mm, "end": v(116.73, 5.62) * mm});
            skLineSegment(sketch, "E1349", {"start": v(116.73, 5.62) * mm, "end": v(116.82, 5.32) * mm});
            skLineSegment(sketch, "E1350", {"start": v(116.82, 5.32) * mm, "end": v(116.9, 5.17) * mm});
            skLineSegment(sketch, "E1351", {"start": v(116.9, 5.17) * mm, "end": v(117.01, 5.04) * mm});
            skLineSegment(sketch, "E1352", {"start": v(117.01, 5.04) * mm, "end": v(117.1, 4.99) * mm});
            skLineSegment(sketch, "E1353", {"start": v(117.1, 4.99) * mm, "end": v(117.28, 4.96) * mm});
            skLineSegment(sketch, "E1354", {"start": v(117.28, 4.96) * mm, "end": v(117.9, 5.1) * mm});
            skLineSegment(sketch, "E1355", {"start": v(117.9, 5.1) * mm, "end": v(118.55, 5.16) * mm});
            skLineSegment(sketch, "E1356", {"start": v(118.55, 5.16) * mm, "end": v(118.72, 5.24) * mm});
            skLineSegment(sketch, "E1357", {"start": v(118.72, 5.24) * mm, "end": v(118.77, 5.32) * mm});
            skLineSegment(sketch, "E1358", {"start": v(118.77, 5.32) * mm, "end": v(118.84, 5.48) * mm});
            skLineSegment(sketch, "E1359", {"start": v(118.84, 5.48) * mm, "end": v(118.87, 5.64) * mm});
            skLineSegment(sketch, "E1360", {"start": v(118.87, 5.64) * mm, "end": v(118.87, 5.96) * mm});
            skLineSegment(sketch, "E1361", {"start": v(118.87, 5.96) * mm, "end": v(118.93, 6.28) * mm});
            skLineSegment(sketch, "E1362", {"start": v(118.93, 6.28) * mm, "end": v(119.08, 6.6) * mm});
            skLineSegment(sketch, "E1363", {"start": v(119.08, 6.6) * mm, "end": v(119.27, 6.9) * mm});
            skLineSegment(sketch, "E1364", {"start": v(119.27, 6.9) * mm, "end": v(119.5, 7.2) * mm});
            skLineSegment(sketch, "E1365", {"start": v(119.5, 7.2) * mm, "end": v(119.77, 7.49) * mm});
            skLineSegment(sketch, "E1366", {"start": v(119.77, 7.49) * mm, "end": v(120.48, 7.35) * mm});
            skLineSegment(sketch, "E1367", {"start": v(120.48, 7.35) * mm, "end": v(121.18, 7.15) * mm});
            skLineSegment(sketch, "E1368", {"start": v(121.18, 7.15) * mm, "end": v(121.29, 6.77) * mm});
            skLineSegment(sketch, "E1369", {"start": v(121.29, 6.77) * mm, "end": v(121.36, 6.4) * mm});
            skLineSegment(sketch, "E1370", {"start": v(121.36, 6.4) * mm, "end": v(121.39, 6.04) * mm});
            skLineSegment(sketch, "E1371", {"start": v(121.39, 6.04) * mm, "end": v(121.37, 5.7) * mm});
            skLineSegment(sketch, "E1372", {"start": v(121.37, 5.7) * mm, "end": v(121.29, 5.38) * mm});
            skLineSegment(sketch, "E1373", {"start": v(121.29, 5.38) * mm, "end": v(121.14, 5.1) * mm});
            skLineSegment(sketch, "E1374", {"start": v(121.14, 5.1) * mm, "end": v(121.1, 4.94) * mm});
            skLineSegment(sketch, "E1375", {"start": v(121.1, 4.94) * mm, "end": v(121.08, 4.77) * mm});
            skLineSegment(sketch, "E1376", {"start": v(121.08, 4.77) * mm, "end": v(121.1, 4.67) * mm});
            skLineSegment(sketch, "E1377", {"start": v(121.1, 4.67) * mm, "end": v(121.2, 4.52) * mm});
            skLineSegment(sketch, "E1378", {"start": v(121.2, 4.52) * mm, "end": v(121.75, 4.18) * mm});
            skLineSegment(sketch, "E1379", {"start": v(121.75, 4.18) * mm, "end": v(122.25, 3.76) * mm});
            skLineSegment(sketch, "E1380", {"start": v(122.25, 3.76) * mm, "end": v(122.43, 3.7) * mm});
            skLineSegment(sketch, "E1381", {"start": v(122.43, 3.7) * mm, "end": v(122.52, 3.72) * mm});
            skLineSegment(sketch, "E1382", {"start": v(122.52, 3.72) * mm, "end": v(122.68, 3.79) * mm});
            skLineSegment(sketch, "E1383", {"start": v(122.68, 3.79) * mm, "end": v(122.81, 3.88) * mm});
            skLineSegment(sketch, "E1384", {"start": v(122.81, 3.88) * mm, "end": v(123.04, 4.1) * mm});
            skLineSegment(sketch, "E1385", {"start": v(123.04, 4.1) * mm, "end": v(123.31, 4.28) * mm});
            skLineSegment(sketch, "E1386", {"start": v(123.31, 4.28) * mm, "end": v(123.63, 4.4) * mm});
            skLineSegment(sketch, "E1387", {"start": v(123.63, 4.4) * mm, "end": v(123.99, 4.49) * mm});
            skLineSegment(sketch, "E1388", {"start": v(123.99, 4.49) * mm, "end": v(124.36, 4.54) * mm});
            skLineSegment(sketch, "E1389", {"start": v(124.36, 4.54) * mm, "end": v(124.76, 4.55) * mm});
            skLineSegment(sketch, "E1390", {"start": v(124.76, 4.55) * mm, "end": v(125.17, 3.95) * mm});
            skLineSegment(sketch, "E1391", {"start": v(125.17, 3.95) * mm, "end": v(125.51, 3.31) * mm});
            skLineSegment(sketch, "E1392", {"start": v(125.51, 3.31) * mm, "end": v(125.32, 2.97) * mm});
            skLineSegment(sketch, "E1393", {"start": v(125.32, 2.97) * mm, "end": v(125.11, 2.65) * mm});
            skLineSegment(sketch, "E1394", {"start": v(125.11, 2.65) * mm, "end": v(124.88, 2.38) * mm});
            skLineSegment(sketch, "E1395", {"start": v(124.88, 2.38) * mm, "end": v(124.62, 2.15) * mm});
            skLineSegment(sketch, "E1396", {"start": v(124.62, 2.15) * mm, "end": v(124.34, 1.98) * mm});
            skLineSegment(sketch, "E1397", {"start": v(124.34, 1.98) * mm, "end": v(124.03, 1.89) * mm});
            skLineSegment(sketch, "E1398", {"start": v(124.03, 1.89) * mm, "end": v(123.9, 1.8) * mm});
            skLineSegment(sketch, "E1399", {"start": v(123.9, 1.8) * mm, "end": v(123.76, 1.7) * mm});
            skLineSegment(sketch, "E1400", {"start": v(123.76, 1.7) * mm, "end": v(123.7, 1.62) * mm});
            skLineSegment(sketch, "E1401", {"start": v(123.7, 1.62) * mm, "end": v(123.68, 1.44) * mm});
            skLineSegment(sketch, "E1402", {"start": v(123.68, 1.44) * mm, "end": v(123.82, 0.8) * mm});
            skLineSegment(sketch, "E1403", {"start": v(123.82, 0.8) * mm, "end": v(123.88, 0.16) * mm});
            skLineSegment(sketch, "E1404", {"start": v(123.88, 0.16) * mm, "end": v(123.96, 0) * mm});
            skLineSegment(sketch, "E1405", {"start": v(123.96, 0) * mm, "end": v(124.04, -0.06) * mm});
            skLineSegment(sketch, "E1406", {"start": v(124.04, -0.06) * mm, "end": v(124.2, -0.13) * mm});
            skLineSegment(sketch, "E1407", {"start": v(124.2, -0.13) * mm, "end": v(124.36, -0.16) * mm});
            skLineSegment(sketch, "E1408", {"start": v(124.36, -0.16) * mm, "end": v(124.68, -0.16) * mm});
            skLineSegment(sketch, "E1409", {"start": v(124.68, -0.16) * mm, "end": v(125, -0.22) * mm});
            skLineSegment(sketch, "E1410", {"start": v(125, -0.22) * mm, "end": v(125.31, -0.37) * mm});
            skLineSegment(sketch, "E1411", {"start": v(125.31, -0.37) * mm, "end": v(125.62, -0.55) * mm});
            skLineSegment(sketch, "E1412", {"start": v(125.62, -0.55) * mm, "end": v(125.92, -0.79) * mm});
            skLineSegment(sketch, "E1413", {"start": v(125.92, -0.79) * mm, "end": v(126.2, -1.06) * mm});
            skLineSegment(sketch, "E1414", {"start": v(126.2, -1.06) * mm, "end": v(126.07, -1.77) * mm});
            skLineSegment(sketch, "E1415", {"start": v(126.07, -1.77) * mm, "end": v(125.87, -2.47) * mm});
            skLineSegment(sketch, "E1416", {"start": v(125.87, -2.47) * mm, "end": v(125.49, -2.58) * mm});
            skLineSegment(sketch, "E1417", {"start": v(125.49, -2.58) * mm, "end": v(125.12, -2.65) * mm});
            skLineSegment(sketch, "E1418", {"start": v(125.12, -2.65) * mm, "end": v(124.76, -2.68) * mm});
            skLineSegment(sketch, "E1419", {"start": v(124.76, -2.68) * mm, "end": v(124.41, -2.66) * mm});
            skLineSegment(sketch, "E1420", {"start": v(124.41, -2.66) * mm, "end": v(124.1, -2.58) * mm});
            skLineSegment(sketch, "E1421", {"start": v(124.1, -2.58) * mm, "end": v(123.81, -2.43) * mm});
            skLineSegment(sketch, "E1422", {"start": v(123.81, -2.43) * mm, "end": v(123.66, -2.38) * mm});
            skLineSegment(sketch, "E1423", {"start": v(123.66, -2.38) * mm, "end": v(123.49, -2.37) * mm});
            skLineSegment(sketch, "E1424", {"start": v(123.49, -2.37) * mm, "end": v(123.39, -2.38) * mm});
            skLineSegment(sketch, "E1425", {"start": v(123.39, -2.38) * mm, "end": v(123.24, -2.5) * mm});
            skLineSegment(sketch, "E1426", {"start": v(123.24, -2.5) * mm, "end": v(122.9, -3.04) * mm});
            skLineSegment(sketch, "E1427", {"start": v(122.9, -3.04) * mm, "end": v(122.48, -3.54) * mm});
            skLineSegment(sketch, "E1428", {"start": v(122.48, -3.54) * mm, "end": v(122.42, -3.72) * mm});
            skLineSegment(sketch, "E1429", {"start": v(122.42, -3.72) * mm, "end": v(122.44, -3.81) * mm});
            skLineSegment(sketch, "E1430", {"start": v(122.44, -3.81) * mm, "end": v(122.5, -3.97) * mm});
            skLineSegment(sketch, "E1431", {"start": v(122.5, -3.97) * mm, "end": v(122.6, -4.1) * mm});
            skLineSegment(sketch, "E1432", {"start": v(122.6, -4.1) * mm, "end": v(122.82, -4.33) * mm});
            skLineSegment(sketch, "E1433", {"start": v(122.82, -4.33) * mm, "end": v(123, -4.6) * mm});
            skLineSegment(sketch, "E1434", {"start": v(123, -4.6) * mm, "end": v(123.12, -4.92) * mm});
            skLineSegment(sketch, "E1435", {"start": v(123.12, -4.92) * mm, "end": v(123.2, -5.28) * mm});
            skLineSegment(sketch, "E1436", {"start": v(123.2, -5.28) * mm, "end": v(123.25, -5.65) * mm});
            skLineSegment(sketch, "E1437", {"start": v(123.25, -5.65) * mm, "end": v(123.27, -6.05) * mm});
            skLineSegment(sketch, "E1438", {"start": v(123.27, -6.05) * mm, "end": v(122.67, -6.45) * mm});
            skLineSegment(sketch, "E1439", {"start": v(122.67, -6.45) * mm, "end": v(122.03, -6.8) * mm});
            skLineSegment(sketch, "E1440", {"start": v(122.03, -6.8) * mm, "end": v(121.68, -6.61) * mm});
            skLineSegment(sketch, "E1441", {"start": v(121.68, -6.61) * mm, "end": v(121.37, -6.4) * mm});
            skLineSegment(sketch, "E1442", {"start": v(121.37, -6.4) * mm, "end": v(121.1, -6.17) * mm});
            skLineSegment(sketch, "E1443", {"start": v(121.1, -6.17) * mm, "end": v(120.86, -5.91) * mm});
            skLineSegment(sketch, "E1444", {"start": v(120.86, -5.91) * mm, "end": v(120.7, -5.63) * mm});
            skLineSegment(sketch, "E1445", {"start": v(120.7, -5.63) * mm, "end": v(120.6, -5.32) * mm});
            skLineSegment(sketch, "E1446", {"start": v(120.6, -5.32) * mm, "end": v(120.53, -5.18) * mm});
            skLineSegment(sketch, "E1447", {"start": v(120.53, -5.18) * mm, "end": v(120.42, -5.05) * mm});
            skLineSegment(sketch, "E1448", {"start": v(120.42, -5.05) * mm, "end": v(120.34, -5) * mm});
            skLineSegment(sketch, "E1449", {"start": v(120.34, -5) * mm, "end": v(120.15, -4.97) * mm});
            skLineSegment(sketch, "E1450", {"start": v(120.15, -4.97) * mm, "end": v(119.52, -5.1) * mm});
            skLineSegment(sketch, "E1451", {"start": v(119.52, -5.1) * mm, "end": v(118.88, -5.17) * mm});
            skLineSegment(sketch, "E1452", {"start": v(118.88, -5.17) * mm, "end": v(118.71, -5.25) * mm});
            skLineSegment(sketch, "E1453", {"start": v(118.71, -5.25) * mm, "end": v(118.65, -5.33) * mm});
            skLineSegment(sketch, "E1454", {"start": v(118.65, -5.33) * mm, "end": v(118.59, -5.49) * mm});
            skLineSegment(sketch, "E1455", {"start": v(118.59, -5.49) * mm, "end": v(118.56, -5.65) * mm});
            skLineSegment(sketch, "E1456", {"start": v(118.56, -5.65) * mm, "end": v(118.56, -5.97) * mm});
            skLineSegment(sketch, "E1457", {"start": v(118.56, -5.97) * mm, "end": v(118.5, -6.29) * mm});
            skLineSegment(sketch, "E1458", {"start": v(118.5, -6.29) * mm, "end": v(118.35, -6.6) * mm});
            skLineSegment(sketch, "E1459", {"start": v(118.35, -6.6) * mm, "end": v(118.16, -6.9) * mm});
            skLineSegment(sketch, "E1460", {"start": v(118.16, -6.9) * mm, "end": v(117.93, -7.2) * mm});
            skLineSegment(sketch, "E1461", {"start": v(117.93, -7.2) * mm, "end": v(117.66, -7.5) * mm});
            skLineSegment(sketch, "E1462", {"start": v(117.66, -7.5) * mm, "end": v(116.95, -7.36) * mm});
            skLineSegment(sketch, "E1463", {"start": v(116.95, -7.36) * mm, "end": v(116.25, -7.16) * mm});
            skLineSegment(sketch, "E1464", {"start": v(116.25, -7.16) * mm, "end": v(116.14, -6.78) * mm});
            skLineSegment(sketch, "E1465", {"start": v(116.14, -6.78) * mm, "end": v(116.07, -6.4) * mm});
            skLineSegment(sketch, "E1466", {"start": v(116.07, -6.4) * mm, "end": v(116.04, -6.05) * mm});
            skLineSegment(sketch, "E1467", {"start": v(116.04, -6.05) * mm, "end": v(116.06, -5.7) * mm});
            skLineSegment(sketch, "E1468", {"start": v(116.06, -5.7) * mm, "end": v(116.14, -5.39) * mm});
            skLineSegment(sketch, "E1469", {"start": v(116.14, -5.39) * mm, "end": v(116.29, -5.1) * mm});
            skLineSegment(sketch, "E1470", {"start": v(116.29, -5.1) * mm, "end": v(116.34, -4.95) * mm});
            skLineSegment(sketch, "E1471", {"start": v(116.34, -4.95) * mm, "end": v(116.35, -4.78) * mm});
            skLineSegment(sketch, "E1472", {"start": v(116.35, -4.78) * mm, "end": v(116.33, -4.68) * mm});
            skLineSegment(sketch, "E1473", {"start": v(116.33, -4.68) * mm, "end": v(116.22, -4.53) * mm});
            skLineSegment(sketch, "E1474", {"start": v(116.22, -4.53) * mm, "end": v(115.68, -4.18) * mm});
            skLineSegment(sketch, "E1475", {"start": v(115.68, -4.18) * mm, "end": v(115.18, -3.77) * mm});
            skLineSegment(sketch, "E1476", {"start": v(115.18, -3.77) * mm, "end": v(115, -3.71) * mm});
            skLineSegment(sketch, "E1477", {"start": v(115, -3.71) * mm, "end": v(114.9, -3.73) * mm});
            skLineSegment(sketch, "E1478", {"start": v(114.9, -3.73) * mm, "end": v(114.75, -3.8) * mm});
            skLineSegment(sketch, "E1479", {"start": v(114.75, -3.8) * mm, "end": v(114.61, -3.89) * mm});
            skLineSegment(sketch, "E1480", {"start": v(114.61, -3.89) * mm, "end": v(114.39, -4.11) * mm});
            skLineSegment(sketch, "E1481", {"start": v(114.39, -4.11) * mm, "end": v(114.12, -4.3) * mm});
            skLineSegment(sketch, "E1482", {"start": v(114.12, -4.3) * mm, "end": v(113.8, -4.41) * mm});
            skLineSegment(sketch, "E1483", {"start": v(113.8, -4.41) * mm, "end": v(113.44, -4.5) * mm});
            skLineSegment(sketch, "E1484", {"start": v(113.44, -4.5) * mm, "end": v(113.07, -4.54) * mm});
            skLineSegment(sketch, "E1485", {"start": v(113.07, -4.54) * mm, "end": v(112.67, -4.56) * mm});
            skLineSegment(sketch, "E1486", {"start": v(112.67, -4.56) * mm, "end": v(112.26, -3.96) * mm});
            skLineSegment(sketch, "E1487", {"start": v(112.26, -3.96) * mm, "end": v(111.91, -3.32) * mm});
            skLineSegment(sketch, "E1488", {"start": v(111.91, -3.32) * mm, "end": v(112.1, -2.97) * mm});
            skLineSegment(sketch, "E1489", {"start": v(112.1, -2.97) * mm, "end": v(112.32, -2.66) * mm});
            skLineSegment(sketch, "E1490", {"start": v(112.32, -2.66) * mm, "end": v(112.55, -2.39) * mm});
            skLineSegment(sketch, "E1491", {"start": v(112.55, -2.39) * mm, "end": v(112.8, -2.15) * mm});
            skLineSegment(sketch, "E1492", {"start": v(112.8, -2.15) * mm, "end": v(113.09, -2) * mm});
            skLineSegment(sketch, "E1493", {"start": v(113.09, -2) * mm, "end": v(113.4, -1.9) * mm});
            skLineSegment(sketch, "E1494", {"start": v(113.4, -1.9) * mm, "end": v(113.54, -1.82) * mm});
            skLineSegment(sketch, "E1495", {"start": v(113.54, -1.82) * mm, "end": v(113.67, -1.7) * mm});
            skLineSegment(sketch, "E1496", {"start": v(113.67, -1.7) * mm, "end": v(113.72, -1.63) * mm});
            skLineSegment(sketch, "E1497", {"start": v(113.72, -1.63) * mm, "end": v(113.75, -1.44) * mm});
            skLineSegment(sketch, "E1498", {"start": v(113.75, -1.44) * mm, "end": v(113.61, -0.81) * mm});
            skLineSegment(sketch, "E1499", {"start": v(113.61, -0.81) * mm, "end": v(113.55, -0.17) * mm});
            skLineSegment(sketch, "E1500", {"start": v(119.46, 0) * mm, "end": v(119.44, 0.2) * mm});
            skLineSegment(sketch, "E1501", {"start": v(119.44, 0.2) * mm, "end": v(119.36, 0.37) * mm});
            skLineSegment(sketch, "E1502", {"start": v(119.36, 0.37) * mm, "end": v(119.24, 0.53) * mm});
            skLineSegment(sketch, "E1503", {"start": v(119.24, 0.53) * mm, "end": v(119.09, 0.65) * mm});
            skLineSegment(sketch, "E1504", {"start": v(119.09, 0.65) * mm, "end": v(118.9, 0.72) * mm});
            skLineSegment(sketch, "E1505", {"start": v(118.9, 0.72) * mm, "end": v(118.71, 0.75) * mm});
            skLineSegment(sketch, "E1506", {"start": v(118.71, 0.75) * mm, "end": v(118.52, 0.72) * mm});
            skLineSegment(sketch, "E1507", {"start": v(118.52, 0.72) * mm, "end": v(118.34, 0.65) * mm});
            skLineSegment(sketch, "E1508", {"start": v(118.34, 0.65) * mm, "end": v(118.18, 0.53) * mm});
            skLineSegment(sketch, "E1509", {"start": v(118.18, 0.53) * mm, "end": v(118.06, 0.37) * mm});
            skLineSegment(sketch, "E1510", {"start": v(118.06, 0.37) * mm, "end": v(117.99, 0.2) * mm});
            skLineSegment(sketch, "E1511", {"start": v(117.99, 0.2) * mm, "end": v(117.96, 0) * mm});
            skLineSegment(sketch, "E1512", {"start": v(117.96, 0) * mm, "end": v(117.99, -0.2) * mm});
            skLineSegment(sketch, "E1513", {"start": v(117.99, -0.2) * mm, "end": v(118.06, -0.38) * mm});
            skLineSegment(sketch, "E1514", {"start": v(118.06, -0.38) * mm, "end": v(118.18, -0.53) * mm});
            skLineSegment(sketch, "E1515", {"start": v(118.18, -0.53) * mm, "end": v(118.34, -0.65) * mm});
            skLineSegment(sketch, "E1516", {"start": v(118.34, -0.65) * mm, "end": v(118.52, -0.73) * mm});
            skLineSegment(sketch, "E1517", {"start": v(118.52, -0.73) * mm, "end": v(118.71, -0.75) * mm});
            skLineSegment(sketch, "E1518", {"start": v(118.71, -0.75) * mm, "end": v(118.9, -0.73) * mm});
            skLineSegment(sketch, "E1519", {"start": v(118.9, -0.73) * mm, "end": v(119.09, -0.65) * mm});
            skLineSegment(sketch, "E1520", {"start": v(119.09, -0.65) * mm, "end": v(119.24, -0.53) * mm});
            skLineSegment(sketch, "E1521", {"start": v(119.24, -0.53) * mm, "end": v(119.36, -0.38) * mm});
            skLineSegment(sketch, "E1522", {"start": v(119.36, -0.38) * mm, "end": v(119.44, -0.2) * mm});
            skLineSegment(sketch, "E1523", {"start": v(119.44, -0.2) * mm, "end": v(119.46, 0) * mm});
            skSolve(sketch);
        }
        {
            var Q0;
            Q0=makeQuery(id+"F0.imprint","IMPRINT",FACE,{"disambiguationData":[TD([[makeQuery(id+"F0.imprint","IMPRINT",EDGE,{"derivedFrom":sQuery(id+"F0.wireOp",EDGE,"E0")}),-1.0]])]});
            var Q1;
            Q1=makeQuery(id+"F0.imprint","IMPRINT",FACE,{"disambiguationData":[TD([[makeQuery(id+"F0.imprint","IMPRINT",EDGE,{"derivedFrom":sQuery(id+"F0.wireOp",EDGE,"E1308")}),-1.0]])]});
            extrude(context, id + "F1", {"entities" : qUnion([Q0, Q1]), "depth" : 4 * mm, "offsetDistance" : 25 * mm});
        }
    });
